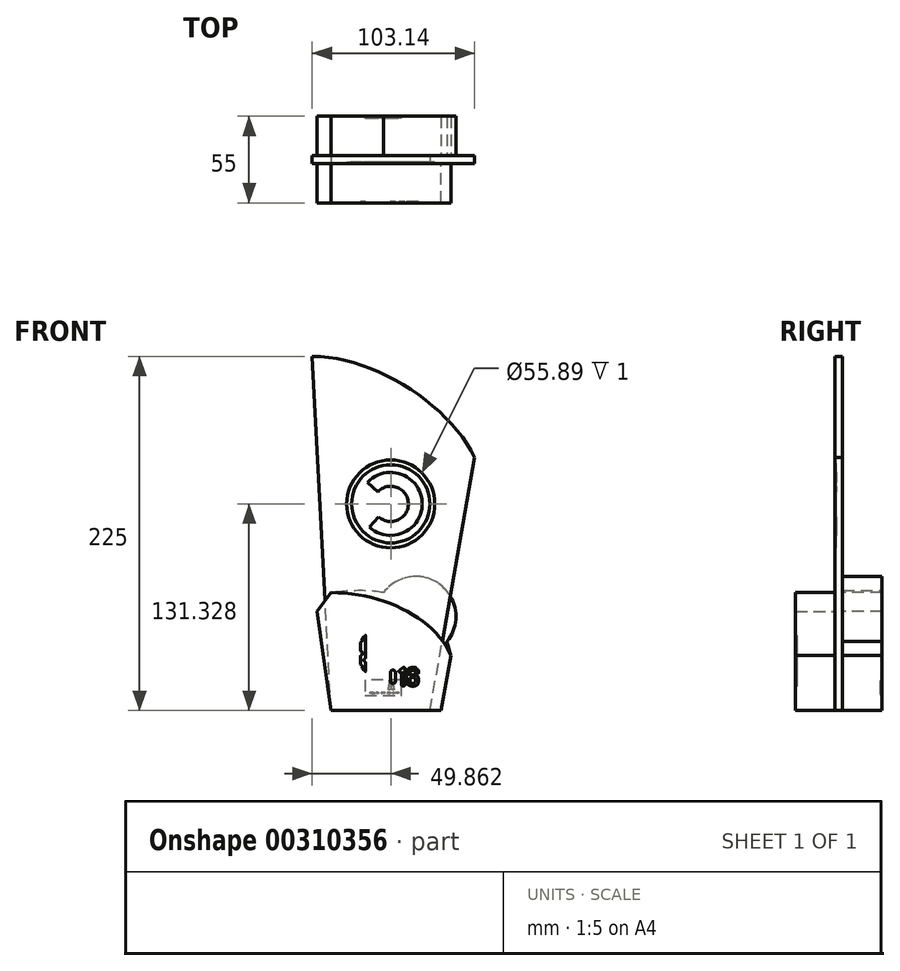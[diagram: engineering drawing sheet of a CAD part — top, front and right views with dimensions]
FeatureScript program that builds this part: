
annotation { "Feature Type Name" : "Feature", "Feature Type Description" : "" }
export const myFeature = defineFeature(function(context is Context, id is Id, definition is map)
    precondition{}
    {
        {
            var Q0;
            Q0=qCreatedBy(makeId("Front.planeOp"),FACE);
            var sketch = newSketch(context, id + "F0", { "sketchPlane" : qUnion([Q0])});
            skLineSegment(sketch, "E0", {"start": v(0, 0) * mm, "end": v(-8.85, 63) * mm});
            skLineSegment(sketch, "E1", {"start": v(-8.85, 63) * mm, "end": v(0, 75) * mm});
            skLineSegment(sketch, "E2", {"start": v(0, 0) * mm, "end": v(70, 0) * mm});
            skLineSegment(sketch, "E3", {"start": v(70, 0) * mm, "end": v(76.17, 35) * mm});
            skFitSpline(sketch, "E4", {"points": [v(0, 75) * mm, v(76.17, 35) * mm], "startDerivative": vector(102.47, -0.52) * mm, "endDerivative": vector(30.62, -70.87) * mm});
            skSolve(sketch);
        }
        {
            var Q0;
            Q0=makeQuery(id+"F0.imprint","IMPRINT",FACE,{"disambiguationData":[TD([[makeQuery(id+"F0.imprint","IMPRINT",EDGE,{"derivedFrom":sQuery(id+"F0.wireOp",EDGE,"E0")}),-1.0]])]});
            extrude(context, id + "F1", {"entities" : qUnion([Q0]), "depth" : 25 * mm});
        }
        {
            var Q0;
            Q0=makeQuery(id+"F1.opExtrude","CAP_FACE",FACE,{"disambiguationData":[OSD([sQuery(id+"F0.wireOp",EDGE,"E0"),sQuery(id+"F0.wireOp",EDGE,"E1"),sQuery(id+"F0.wireOp",EDGE,"E2"),sQuery(id+"F0.wireOp",EDGE,"E3"),sQuery(id+"F0.wireOp",EDGE,"E4")])],"isStart":true});
            var sketch = newSketch(context, id + "F2", { "sketchPlane" : qUnion([Q0])});
            skLineSegment(sketch, "E5", {"start": v(0, 0) * mm, "end": v(11.8, 225) * mm});
            skLineSegment(sketch, "E6", {"start": v(-63, 0) * mm, "end": v(-91.35, 160.77) * mm});
            skFitSpline(sketch, "E7", {"points": [v(11.8, 225) * mm, v(-91.35, 160.77) * mm], "startDerivative": vector(-117.23, 0.2) * mm, "endDerivative": vector(-48.13, -100.78) * mm});
            skLineSegment(sketch, "E8", {"start": v(0, 0) * mm, "end": v(-63, 0) * mm});
            skSolve(sketch);
        }
        {
            var Q0;
            {var subQ5=sQuery(id+"F2.wireOp",EDGE,"E7");Q0=makeQuery(id+"F2.imprint","IMPRINT",FACE,{"disambiguationData":[TD([[makeQuery(id+"F2.imprint","IMPRINT",EDGE,{"derivedFrom":subQ5}),1.0]])]});}
            var Q1;
            {var subQ0=sQuery(id+"F2.wireOp",EDGE,"E8");Q1=makeQuery(id+"F2.imprint","IMPRINT",FACE,{"disambiguationData":[TD([[makeQuery(id+"F2.imprint","IMPRINT",EDGE,{"derivedFrom":subQ0}),-1.0]])]});}
            extrude(context, id + "F3", {"entities" : qUnion([Q0, Q1]), "depth" : 5 * mm});
        }
        {
            var Q0;
            Q0=makeQuery(id+"F3.opExtrude","CAP_FACE",FACE,{"disambiguationData":[OSD([sQuery(id+"F2.wireOp",EDGE,"E5"),sQuery(id+"F2.wireOp",EDGE,"E6"),sQuery(id+"F2.wireOp",EDGE,"E7"),sQuery(id+"F2.wireOp",EDGE,"E8")])],"isStart":false});
            var sketch = newSketch(context, id + "F4", { "sketchPlane" : qUnion([Q0])});
            skFitSpline(sketch, "E9.0.0", {"points": [v(-76.17, 35) * mm, v(-65.97, 58.62) * mm, v(-34.16, 74.83) * mm, v(0, 75) * mm]});
            skLineSegment(sketch, "E9.0.1", {"start": v(0, 75) * mm, "end": v(8.85, 63) * mm});
            skLineSegment(sketch, "E9.0.2", {"start": v(8.85, 63) * mm, "end": v(0, 0) * mm});
            skLineSegment(sketch, "E9.0.3", {"start": v(0, 0) * mm, "end": v(-70, 0) * mm});
            skLineSegment(sketch, "E9.0.4", {"start": v(-70, 0) * mm, "end": v(-76.17, 35) * mm});
            skArc(sketch, "E10", {"start": v(-30.84, 70.38) * mm, "mid": v(-68.31, 80.8) * mm, "end": v(-72.31, 42.1) * mm});
            skFitSpline(sketch, "E11.trimOffspring", {"points": [v(-76.17, 35) * mm, v(-65.97, 58.62) * mm, v(-34.16, 74.83) * mm, v(0, 75) * mm]});
            skSolve(sketch);
        }
        {
            var Q0;
            Q0 = qSketchRegion(id + "F4", true);
            extrude(context, id + "F5", {"entities" : qUnion([Q0]), "depth" : 25 * mm});
        }
        {
            var Q0;
            Q0=makeQuery(id+"F1.opExtrude","CAP_FACE",FACE,{"disambiguationData":[OSD([sQuery(id+"F0.wireOp",EDGE,"E0"),sQuery(id+"F0.wireOp",EDGE,"E1"),sQuery(id+"F0.wireOp",EDGE,"E2"),sQuery(id+"F0.wireOp",EDGE,"E3"),sQuery(id+"F0.wireOp",EDGE,"E4")])],"isStart":false});
            var sketch = newSketch(context, id + "F6", { "sketchPlane" : qUnion([Q0])});
            skFitSpline(sketch, "E12", {"points": [v(15.05, 12.41) * mm, v(14.99, 12.45) * mm, v(14.9, 12.51) * mm, v(14.87, 12.56) * mm]});
            skFitSpline(sketch, "E13", {"points": [v(14.87, 12.56) * mm, v(14.79, 12.67) * mm, v(14.78, 12.9) * mm, v(14.86, 13.02) * mm]});
            skFitSpline(sketch, "E14", {"points": [v(14.86, 13.02) * mm, v(15.02, 13.26) * mm, v(16.64, 13.8) * mm, v(17.88, 14.02) * mm]});
            skFitSpline(sketch, "E15", {"points": [v(17.88, 14.02) * mm, v(18.82, 14.2) * mm, v(19.85, 14.28) * mm, v(20.87, 14.28) * mm]});
            skFitSpline(sketch, "E16", {"points": [v(20.87, 14.28) * mm, v(21.33, 14.28) * mm, v(21.37, 14.29) * mm, v(21.34, 14.34) * mm]});
            skFitSpline(sketch, "E17", {"points": [v(21.34, 14.34) * mm, v(21.1, 14.93) * mm, v(21.25, 15.6) * mm, v(21.7, 16.01) * mm]});
            skFitSpline(sketch, "E18", {"points": [v(21.71, 22.4) * mm, v(21.27, 22.8) * mm, v(21.1, 23.5) * mm, v(21.33, 24.03) * mm]});
            skLineSegment(sketch, "E19", {"start": v(21.7, 16.01) * mm, "end": v(21.88, 16.17) * mm});
            skLineSegment(sketch, "E20", {"start": v(21.88, 16.17) * mm, "end": v(21.88, 19.2) * mm});
            skLineSegment(sketch, "E21", {"start": v(21.88, 19.2) * mm, "end": v(21.88, 22.24) * mm});
            skLineSegment(sketch, "E22", {"start": v(21.88, 22.24) * mm, "end": v(21.71, 22.4) * mm});
            skFitSpline(sketch, "E23", {"points": [v(18.99, 26.4) * mm, v(18.86, 26.33) * mm, v(18.77, 26.32) * mm, v(18.43, 26.32) * mm]});
            skFitSpline(sketch, "E24", {"points": [v(18.43, 26.32) * mm, v(18.06, 26.32) * mm, v(18.02, 26.33) * mm, v(17.8, 26.43) * mm]});
            skFitSpline(sketch, "E25", {"points": [v(17.8, 26.43) * mm, v(17.5, 26.58) * mm, v(17.22, 26.85) * mm, v(17.08, 27.15) * mm]});
            skFitSpline(sketch, "E26", {"points": [v(17.08, 27.15) * mm, v(16.98, 27.37) * mm, v(16.97, 27.41) * mm, v(16.97, 27.77) * mm]});
            skFitSpline(sketch, "E27", {"points": [v(16.97, 27.77) * mm, v(16.97, 28.14) * mm, v(16.97, 28.16) * mm, v(17.1, 28.41) * mm]});
            skFitSpline(sketch, "E28", {"points": [v(17.1, 28.41) * mm, v(17.25, 28.72) * mm, v(17.5, 28.98) * mm, v(17.82, 29.12) * mm]});
            skLineSegment(sketch, "E29", {"start": v(21.33, 24.03) * mm, "end": v(21.4, 24.2) * mm});
            skLineSegment(sketch, "E30", {"start": v(21.4, 24.2) * mm, "end": v(20.28, 25.34) * mm});
            skLineSegment(sketch, "E31", {"start": v(20.28, 25.34) * mm, "end": v(19.15, 26.47) * mm});
            skLineSegment(sketch, "E32", {"start": v(19.15, 26.47) * mm, "end": v(18.99, 26.4) * mm});
            skFitSpline(sketch, "E33", {"points": [v(17.83, 34.98) * mm, v(17.62, 35.07) * mm, v(17.3, 35.34) * mm, v(17.17, 35.54) * mm]});
            skFitSpline(sketch, "E34", {"points": [v(17.17, 35.54) * mm, v(16.95, 35.9) * mm, v(16.9, 36.4) * mm, v(17.03, 36.82) * mm]});
            skLineSegment(sketch, "E35", {"start": v(17.82, 29.12) * mm, "end": v(18.02, 29.21) * mm});
            skLineSegment(sketch, "E36", {"start": v(18.02, 29.21) * mm, "end": v(18.02, 32.06) * mm});
            skLineSegment(sketch, "E37", {"start": v(18.02, 32.06) * mm, "end": v(18.02, 34.9) * mm});
            skLineSegment(sketch, "E38", {"start": v(18.02, 34.9) * mm, "end": v(17.83, 34.98) * mm});
            skFitSpline(sketch, "E39", {"points": [v(14.67, 39.23) * mm, v(14.4, 39.12) * mm, v(14.11, 39.1) * mm, v(13.84, 39.16) * mm]});
            skFitSpline(sketch, "E40", {"points": [v(13.84, 39.16) * mm, v(13.53, 39.23) * mm, v(13.36, 39.33) * mm, v(13.14, 39.54) * mm]});
            skFitSpline(sketch, "E41", {"points": [v(13.14, 39.54) * mm, v(12.81, 39.85) * mm, v(12.68, 40.16) * mm, v(12.68, 40.6) * mm]});
            skFitSpline(sketch, "E42", {"points": [v(12.68, 40.6) * mm, v(12.68, 41.2) * mm, v(12.99, 41.7) * mm, v(13.53, 41.95) * mm]});
            skLineSegment(sketch, "E43", {"start": v(17.03, 36.82) * mm, "end": v(17.11, 37.05) * mm});
            skLineSegment(sketch, "E44", {"start": v(17.11, 37.05) * mm, "end": v(15.99, 38.17) * mm});
            skLineSegment(sketch, "E45", {"start": v(15.99, 38.17) * mm, "end": v(14.86, 39.3) * mm});
            skLineSegment(sketch, "E46", {"start": v(14.86, 39.3) * mm, "end": v(14.67, 39.23) * mm});
            skFitSpline(sketch, "E47", {"points": [v(13.5, 52.12) * mm, v(12.4, 52.66) * mm, v(12.4, 54.26) * mm, v(13.54, 54.8) * mm]});
            skFitSpline(sketch, "E48", {"points": [v(13.54, 54.8) * mm, v(13.75, 54.9) * mm, v(13.8, 54.9) * mm, v(14.15, 54.9) * mm]});
            skFitSpline(sketch, "E49", {"points": [v(14.15, 54.9) * mm, v(14.5, 54.9) * mm, v(14.54, 54.9) * mm, v(14.75, 54.8) * mm]});
            skFitSpline(sketch, "E50", {"points": [v(14.75, 54.8) * mm, v(15.54, 54.43) * mm, v(15.85, 53.53) * mm, v(15.46, 52.75) * mm]});
            skFitSpline(sketch, "E51", {"points": [v(15.46, 52.75) * mm, v(15.33, 52.5) * mm, v(15.05, 52.25) * mm, v(14.8, 52.12) * mm]});
            skLineSegment(sketch, "E52", {"start": v(13.53, 41.95) * mm, "end": v(13.75, 42.05) * mm});
            skLineSegment(sketch, "E53", {"start": v(13.75, 42.05) * mm, "end": v(13.74, 47.03) * mm});
            skLineSegment(sketch, "E54", {"start": v(13.74, 47.03) * mm, "end": v(13.73, 52.01) * mm});
            skLineSegment(sketch, "E55", {"start": v(13.73, 52.01) * mm, "end": v(13.5, 52.12) * mm});
            skFitSpline(sketch, "E56", {"points": [v(14.7, 41.98) * mm, v(15, 41.87) * mm, v(15.34, 41.56) * mm, v(15.49, 41.24) * mm]});
            skFitSpline(sketch, "E57", {"points": [v(15.49, 41.24) * mm, v(15.66, 40.87) * mm, v(15.67, 40.47) * mm, v(15.52, 40.04) * mm]});
            skLineSegment(sketch, "E58", {"start": v(14.8, 52.12) * mm, "end": v(14.58, 52.02) * mm});
            skLineSegment(sketch, "E59", {"start": v(14.58, 52.02) * mm, "end": v(14.58, 47.02) * mm});
            skLineSegment(sketch, "E60", {"start": v(14.58, 47.02) * mm, "end": v(14.58, 42.02) * mm});
            skLineSegment(sketch, "E61", {"start": v(14.58, 42.02) * mm, "end": v(14.7, 41.98) * mm});
            skFitSpline(sketch, "E62", {"points": [v(17.8, 43.55) * mm, v(17.5, 43.7) * mm, v(17.23, 43.97) * mm, v(17.08, 44.27) * mm]});
            skFitSpline(sketch, "E63", {"points": [v(17.08, 44.27) * mm, v(16.98, 44.49) * mm, v(16.98, 44.53) * mm, v(16.97, 44.88) * mm]});
            skFitSpline(sketch, "E64", {"points": [v(16.97, 44.88) * mm, v(16.97, 45.24) * mm, v(16.98, 45.28) * mm, v(17.08, 45.5) * mm]});
            skFitSpline(sketch, "E65", {"points": [v(17.08, 45.5) * mm, v(17.29, 45.93) * mm, v(17.66, 46.23) * mm, v(18.12, 46.33) * mm]});
            skFitSpline(sketch, "E66", {"points": [v(18.12, 46.33) * mm, v(18.41, 46.4) * mm, v(18.62, 46.38) * mm, v(18.95, 46.27) * mm]});
            skLineSegment(sketch, "E67", {"start": v(15.52, 40.04) * mm, "end": v(15.46, 39.87) * mm});
            skLineSegment(sketch, "E68", {"start": v(15.46, 39.87) * mm, "end": v(16.58, 38.75) * mm});
            skLineSegment(sketch, "E69", {"start": v(16.58, 38.75) * mm, "end": v(17.7, 37.64) * mm});
            skLineSegment(sketch, "E70", {"start": v(17.7, 37.64) * mm, "end": v(17.86, 37.7) * mm});
            skLineSegment(sketch, "E71", {"start": v(17.86, 37.7) * mm, "end": v(18.02, 37.75) * mm});
            skLineSegment(sketch, "E72", {"start": v(18.02, 37.75) * mm, "end": v(18.02, 40.6) * mm});
            skLineSegment(sketch, "E73", {"start": v(18.02, 40.6) * mm, "end": v(18.02, 43.45) * mm});
            skLineSegment(sketch, "E74", {"start": v(18.02, 43.45) * mm, "end": v(17.8, 43.55) * mm});
            skFitSpline(sketch, "E75", {"points": [v(20.28, 47.31) * mm, v(21, 48.03) * mm, v(21.4, 48.45) * mm, v(21.39, 48.48) * mm]});
            skFitSpline(sketch, "E76", {"points": [v(21.39, 48.48) * mm, v(21.38, 48.5) * mm, v(21.34, 48.6) * mm, v(21.31, 48.69) * mm]});
            skFitSpline(sketch, "E77", {"points": [v(21.31, 48.69) * mm, v(21.18, 49.04) * mm, v(21.22, 49.5) * mm, v(21.4, 49.87) * mm]});
            skFitSpline(sketch, "E78", {"points": [v(21.4, 49.87) * mm, v(21.51, 50.08) * mm, v(21.8, 50.36) * mm, v(22, 50.47) * mm]});
            skLineSegment(sketch, "E79", {"start": v(18.95, 46.27) * mm, "end": v(19.16, 46.2) * mm});
            skLineSegment(sketch, "E80", {"start": v(19.16, 46.2) * mm, "end": v(20.28, 47.31) * mm});
            skFitSpline(sketch, "E81", {"points": [v(22.03, 56.42) * mm, v(21.42, 56.73) * mm, v(21.1, 57.43) * mm, v(21.28, 58.11) * mm]});
            skFitSpline(sketch, "E82", {"points": [v(21.28, 58.11) * mm, v(21.39, 58.52) * mm, v(21.69, 58.88) * mm, v(22.08, 59.07) * mm]});
            skFitSpline(sketch, "E83", {"points": [v(22.08, 59.07) * mm, v(22.3, 59.17) * mm, v(22.34, 59.18) * mm, v(22.71, 59.18) * mm]});
            skFitSpline(sketch, "E84", {"points": [v(22.71, 59.18) * mm, v(23.08, 59.18) * mm, v(23.12, 59.17) * mm, v(23.33, 59.07) * mm]});
            skFitSpline(sketch, "E85", {"points": [v(23.33, 59.07) * mm, v(24.45, 58.53) * mm, v(24.48, 56.96) * mm, v(23.37, 56.4) * mm]});
            skLineSegment(sketch, "E86", {"start": v(22, 50.47) * mm, "end": v(22.2, 50.56) * mm});
            skLineSegment(sketch, "E87", {"start": v(22.2, 50.56) * mm, "end": v(22.2, 53.45) * mm});
            skLineSegment(sketch, "E88", {"start": v(22.2, 53.45) * mm, "end": v(22.2, 56.33) * mm});
            skLineSegment(sketch, "E89", {"start": v(22.2, 56.33) * mm, "end": v(22.03, 56.42) * mm});
            skFitSpline(sketch, "E90", {"points": [v(23.42, 50.47) * mm, v(24.08, 50.12) * mm, v(24.38, 49.25) * mm, v(24.06, 48.57) * mm]});
            skFitSpline(sketch, "E91", {"points": [v(24.06, 48.57) * mm, v(23.93, 48.29) * mm, v(23.66, 48) * mm, v(23.42, 47.87) * mm]});
            skLineSegment(sketch, "E92", {"start": v(23.37, 56.4) * mm, "end": v(23.23, 56.33) * mm});
            skLineSegment(sketch, "E93", {"start": v(23.23, 56.33) * mm, "end": v(23.23, 53.45) * mm});
            skLineSegment(sketch, "E94", {"start": v(23.23, 53.45) * mm, "end": v(23.23, 50.56) * mm});
            skLineSegment(sketch, "E95", {"start": v(23.23, 50.56) * mm, "end": v(23.42, 50.47) * mm});
            skFitSpline(sketch, "E96", {"points": [v(25.6, 35.8) * mm, v(25.46, 36.22) * mm, v(25.48, 36.6) * mm, v(25.66, 36.98) * mm]});
            skFitSpline(sketch, "E97", {"points": [v(25.66, 36.98) * mm, v(25.78, 37.24) * mm, v(26.12, 37.56) * mm, v(26.37, 37.67) * mm]});
            skLineSegment(sketch, "E98", {"start": v(23.42, 47.87) * mm, "end": v(23.23, 47.78) * mm});
            skLineSegment(sketch, "E99", {"start": v(23.23, 47.78) * mm, "end": v(23.23, 40.6) * mm});
            skLineSegment(sketch, "E100", {"start": v(23.23, 40.6) * mm, "end": v(23.23, 33.43) * mm});
            skLineSegment(sketch, "E101", {"start": v(23.23, 33.43) * mm, "end": v(23.33, 33.4) * mm});
            skLineSegment(sketch, "E102", {"start": v(23.33, 33.4) * mm, "end": v(23.44, 33.35) * mm});
            skLineSegment(sketch, "E103", {"start": v(23.44, 33.35) * mm, "end": v(24.56, 34.47) * mm});
            skLineSegment(sketch, "E104", {"start": v(24.56, 34.47) * mm, "end": v(25.68, 35.6) * mm});
            skLineSegment(sketch, "E105", {"start": v(25.68, 35.6) * mm, "end": v(25.6, 35.8) * mm});
            skLineSegment(sketch, "E106", {"start": v(25.6, 35.8) * mm, "end": v(25.51, 36.34) * mm});
            skFitSpline(sketch, "E107", {"points": [v(26.37, 47.83) * mm, v(26.12, 47.93) * mm, v(25.79, 48.25) * mm, v(25.66, 48.52) * mm]});
            skFitSpline(sketch, "E108", {"points": [v(25.66, 48.52) * mm, v(25.14, 49.6) * mm, v(26.05, 50.83) * mm, v(27.22, 50.63) * mm]});
            skFitSpline(sketch, "E109", {"points": [v(27.22, 50.63) * mm, v(28.32, 50.44) * mm, v(28.83, 49.18) * mm, v(28.17, 48.29) * mm]});
            skFitSpline(sketch, "E110", {"points": [v(28.17, 48.29) * mm, v(28.01, 48.07) * mm, v(27.68, 47.82) * mm, v(27.5, 47.78) * mm]});
            skLineSegment(sketch, "E111", {"start": v(26.37, 37.67) * mm, "end": v(26.56, 37.75) * mm});
            skLineSegment(sketch, "E112", {"start": v(26.56, 37.75) * mm, "end": v(26.56, 42.75) * mm});
            skLineSegment(sketch, "E113", {"start": v(26.56, 42.75) * mm, "end": v(26.57, 47.75) * mm});
            skLineSegment(sketch, "E114", {"start": v(26.57, 47.75) * mm, "end": v(26.37, 47.83) * mm});
            skFitSpline(sketch, "E115", {"points": [v(27.5, 37.72) * mm, v(27.68, 37.68) * mm, v(28.01, 37.43) * mm, v(28.17, 37.21) * mm]});
            skFitSpline(sketch, "E116", {"points": [v(28.17, 37.21) * mm, v(28.44, 36.84) * mm, v(28.53, 36.32) * mm, v(28.4, 35.89) * mm]});
            skFitSpline(sketch, "E117", {"points": [v(28.4, 35.89) * mm, v(28.14, 35.08) * mm, v(27.25, 34.64) * mm, v(26.46, 34.95) * mm]});
            skLineSegment(sketch, "E118", {"start": v(27.5, 47.78) * mm, "end": v(27.4, 47.76) * mm});
            skLineSegment(sketch, "E119", {"start": v(27.4, 47.76) * mm, "end": v(27.4, 42.75) * mm});
            skLineSegment(sketch, "E120", {"start": v(27.4, 42.75) * mm, "end": v(27.4, 37.74) * mm});
            skLineSegment(sketch, "E121", {"start": v(27.4, 37.74) * mm, "end": v(27.5, 37.72) * mm});
            skFitSpline(sketch, "E122", {"points": [v(24.06, 32.65) * mm, v(24.23, 32.32) * mm, v(24.22, 31.82) * mm, v(24.05, 31.44) * mm]});
            skFitSpline(sketch, "E123", {"points": [v(24.05, 31.44) * mm, v(23.92, 31.16) * mm, v(23.61, 30.84) * mm, v(23.37, 30.73) * mm]});
            skLineSegment(sketch, "E124", {"start": v(26.46, 34.95) * mm, "end": v(26.27, 35.02) * mm});
            skLineSegment(sketch, "E125", {"start": v(26.27, 35.02) * mm, "end": v(25.14, 33.89) * mm});
            skLineSegment(sketch, "E126", {"start": v(25.14, 33.89) * mm, "end": v(24, 32.75) * mm});
            skLineSegment(sketch, "E127", {"start": v(24, 32.75) * mm, "end": v(24.06, 32.65) * mm});
            skFitSpline(sketch, "E128", {"points": [v(29.9, 31.5) * mm, v(29.68, 32) * mm, v(29.8, 32.67) * mm, v(30.21, 33.09) * mm]});
            skFitSpline(sketch, "E129", {"points": [v(30.21, 33.09) * mm, v(30.3, 33.18) * mm, v(30.48, 33.3) * mm, v(30.63, 33.38) * mm]});
            skLineSegment(sketch, "E130", {"start": v(23.37, 30.73) * mm, "end": v(23.23, 30.67) * mm});
            skLineSegment(sketch, "E131", {"start": v(23.23, 30.67) * mm, "end": v(23.23, 27.78) * mm});
            skLineSegment(sketch, "E132", {"start": v(23.23, 27.78) * mm, "end": v(23.23, 24.9) * mm});
            skLineSegment(sketch, "E133", {"start": v(23.23, 24.9) * mm, "end": v(23.32, 24.84) * mm});
            skLineSegment(sketch, "E134", {"start": v(23.32, 24.84) * mm, "end": v(23.42, 24.8) * mm});
            skLineSegment(sketch, "E135", {"start": v(23.42, 24.8) * mm, "end": v(26.7, 28.07) * mm});
            skLineSegment(sketch, "E136", {"start": v(26.7, 28.07) * mm, "end": v(29.97, 31.34) * mm});
            skLineSegment(sketch, "E137", {"start": v(29.97, 31.34) * mm, "end": v(29.9, 31.5) * mm});
            skFitSpline(sketch, "E138", {"points": [v(30.65, 43.56) * mm, v(30.04, 43.84) * mm, v(29.72, 44.45) * mm, v(29.8, 45.11) * mm]});
            skFitSpline(sketch, "E139", {"points": [v(29.8, 45.11) * mm, v(29.92, 45.9) * mm, v(30.72, 46.5) * mm, v(31.5, 46.36) * mm]});
            skFitSpline(sketch, "E140", {"points": [v(31.5, 46.36) * mm, v(32.47, 46.19) * mm, v(33.02, 45.15) * mm, v(32.6, 44.26) * mm]});
            skFitSpline(sketch, "E141", {"points": [v(32.6, 44.26) * mm, v(32.48, 44) * mm, v(32.15, 43.67) * mm, v(31.9, 43.56) * mm]});
            skLineSegment(sketch, "E142", {"start": v(30.63, 33.38) * mm, "end": v(30.87, 33.5) * mm});
            skLineSegment(sketch, "E143", {"start": v(30.87, 33.5) * mm, "end": v(30.87, 38.48) * mm});
            skLineSegment(sketch, "E144", {"start": v(30.87, 38.48) * mm, "end": v(30.87, 43.45) * mm});
            skLineSegment(sketch, "E145", {"start": v(30.87, 43.45) * mm, "end": v(30.65, 43.56) * mm});
            skFitSpline(sketch, "E146", {"points": [v(31.91, 33.38) * mm, v(32.47, 33.12) * mm, v(32.82, 32.47) * mm, v(32.73, 31.85) * mm]});
            skFitSpline(sketch, "E147", {"points": [v(32.73, 31.85) * mm, v(32.6, 30.93) * mm, v(31.67, 30.36) * mm, v(30.8, 30.66) * mm]});
            skLineSegment(sketch, "E148", {"start": v(31.9, 43.56) * mm, "end": v(31.7, 43.48) * mm});
            skLineSegment(sketch, "E149", {"start": v(31.7, 43.48) * mm, "end": v(31.7, 38.48) * mm});
            skLineSegment(sketch, "E150", {"start": v(31.7, 38.48) * mm, "end": v(31.7, 33.48) * mm});
            skLineSegment(sketch, "E151", {"start": v(31.7, 33.48) * mm, "end": v(31.91, 33.38) * mm});
            skFitSpline(sketch, "E152", {"points": [v(24.09, 24.03) * mm, v(24.3, 23.46) * mm, v(24.15, 22.81) * mm, v(23.69, 22.38) * mm]});
            skLineSegment(sketch, "E153", {"start": v(30.8, 30.66) * mm, "end": v(30.54, 30.74) * mm});
            skLineSegment(sketch, "E154", {"start": v(30.54, 30.74) * mm, "end": v(27.28, 27.48) * mm});
            skLineSegment(sketch, "E155", {"start": v(27.28, 27.48) * mm, "end": v(24.02, 24.22) * mm});
            skLineSegment(sketch, "E156", {"start": v(24.02, 24.22) * mm, "end": v(24.09, 24.03) * mm});
            skFitSpline(sketch, "E157", {"points": [v(23.7, 16.01) * mm, v(24.17, 15.58) * mm, v(24.31, 14.91) * mm, v(24.07, 14.34) * mm]});
            skFitSpline(sketch, "E158", {"points": [v(24.07, 14.34) * mm, v(24.05, 14.28) * mm, v(24.83, 14.28) * mm, v(40.2, 14.28) * mm]});
            skFitSpline(sketch, "E159", {"points": [v(40.2, 14.28) * mm, v(52.62, 14.27) * mm, v(56.38, 14.27) * mm, v(56.47, 14.23) * mm]});
            skFitSpline(sketch, "E160", {"points": [v(56.47, 14.23) * mm, v(56.62, 14.18) * mm, v(56.71, 14.05) * mm, v(56.72, 13.88) * mm]});
            skFitSpline(sketch, "E161", {"points": [v(56.72, 13.88) * mm, v(56.72, 13.7) * mm, v(56.63, 13.54) * mm, v(56.51, 13.5) * mm]});
            skFitSpline(sketch, "E162", {"points": [v(56.51, 13.5) * mm, v(56.44, 13.46) * mm, v(51.68, 13.45) * mm, v(38, 13.44) * mm]});
            skLineSegment(sketch, "E163", {"start": v(23.69, 22.38) * mm, "end": v(23.53, 22.24) * mm});
            skLineSegment(sketch, "E164", {"start": v(23.53, 22.24) * mm, "end": v(23.53, 19.2) * mm});
            skLineSegment(sketch, "E165", {"start": v(23.53, 19.2) * mm, "end": v(23.53, 16.18) * mm});
            skLineSegment(sketch, "E166", {"start": v(23.53, 16.18) * mm, "end": v(23.7, 16.01) * mm});
            skFitSpline(sketch, "E167", {"points": [v(19, 13.36) * mm, v(17.8, 13.2) * mm, v(16.68, 12.93) * mm, v(15.78, 12.58) * mm]});
            skFitSpline(sketch, "E168", {"points": [v(15.78, 12.58) * mm, v(15.18, 12.34) * mm, v(15.2, 12.34) * mm, v(15.06, 12.41) * mm]});
            skLineSegment(sketch, "E169", {"start": v(38, 13.44) * mm, "end": v(19.59, 13.43) * mm});
            skLineSegment(sketch, "E170", {"start": v(19.59, 13.43) * mm, "end": v(19, 13.36) * mm});
            skLineSegment(sketch, "E171", {"start": v(15.06, 12.41) * mm, "end": v(15.05, 12.41) * mm});
            skLineSegment(sketch, "E172", {"start": v(15.05, 12.41) * mm, "end": v(15.06, 12.41) * mm});
            skFitSpline(sketch, "E173", {"points": [v(22.01, 30.75) * mm, v(21.81, 30.84) * mm, v(21.5, 31.15) * mm, v(21.4, 31.37) * mm]});
            skFitSpline(sketch, "E174", {"points": [v(21.4, 31.37) * mm, v(21.15, 31.84) * mm, v(21.17, 32.37) * mm, v(21.44, 32.83) * mm]});
            skFitSpline(sketch, "E175", {"points": [v(21.44, 32.83) * mm, v(21.55, 33.01) * mm, v(21.81, 33.26) * mm, v(22.03, 33.37) * mm]});
            skLineSegment(sketch, "E176", {"start": v(22.18, 27.77) * mm, "end": v(22.18, 30.66) * mm});
            skLineSegment(sketch, "E177", {"start": v(22.18, 30.66) * mm, "end": v(22.01, 30.75) * mm});
            skFitSpline(sketch, "E178", {"points": [v(22.1, 47.84) * mm, v(22, 47.88) * mm, v(21.98, 47.86) * mm, v(20.86, 46.74) * mm]});
            skLineSegment(sketch, "E179", {"start": v(22.03, 33.37) * mm, "end": v(22.19, 33.45) * mm});
            skLineSegment(sketch, "E180", {"start": v(22.19, 33.45) * mm, "end": v(22.19, 40.62) * mm});
            skLineSegment(sketch, "E181", {"start": v(22.19, 40.62) * mm, "end": v(22.19, 47.8) * mm});
            skLineSegment(sketch, "E182", {"start": v(22.19, 47.8) * mm, "end": v(22.1, 47.84) * mm});
            skFitSpline(sketch, "E183", {"points": [v(19.78, 45.48) * mm, v(19.82, 45.4) * mm, v(19.86, 45.25) * mm, v(19.88, 45.12) * mm]});
            skFitSpline(sketch, "E184", {"points": [v(19.88, 45.12) * mm, v(19.99, 44.5) * mm, v(19.63, 43.84) * mm, v(19.06, 43.56) * mm]});
            skLineSegment(sketch, "E185", {"start": v(20.86, 46.74) * mm, "end": v(19.73, 45.6) * mm});
            skLineSegment(sketch, "E186", {"start": v(19.73, 45.6) * mm, "end": v(19.78, 45.48) * mm});
            skFitSpline(sketch, "E187", {"points": [v(19.04, 37.68) * mm, v(19.62, 37.42) * mm, v(19.99, 36.74) * mm, v(19.88, 36.1) * mm]});
            skFitSpline(sketch, "E188", {"points": [v(19.88, 36.1) * mm, v(19.8, 35.63) * mm, v(19.48, 35.2) * mm, v(19.06, 35) * mm]});
            skLineSegment(sketch, "E189", {"start": v(19.06, 43.56) * mm, "end": v(18.84, 43.46) * mm});
            skLineSegment(sketch, "E190", {"start": v(18.84, 43.46) * mm, "end": v(18.84, 40.61) * mm});
            skLineSegment(sketch, "E191", {"start": v(18.84, 40.61) * mm, "end": v(18.84, 37.76) * mm});
            skLineSegment(sketch, "E192", {"start": v(18.84, 37.76) * mm, "end": v(19.04, 37.68) * mm});
            skFitSpline(sketch, "E193", {"points": [v(19.07, 29.1) * mm, v(19.76, 28.76) * mm, v(20.07, 27.97) * mm, v(19.8, 27.25) * mm]});
            skLineSegment(sketch, "E194", {"start": v(19.06, 35) * mm, "end": v(18.84, 34.9) * mm});
            skLineSegment(sketch, "E195", {"start": v(18.84, 34.9) * mm, "end": v(18.84, 32.06) * mm});
            skLineSegment(sketch, "E196", {"start": v(18.84, 32.06) * mm, "end": v(18.84, 29.21) * mm});
            skLineSegment(sketch, "E197", {"start": v(18.84, 29.21) * mm, "end": v(19.07, 29.1) * mm});
            skFitSpline(sketch, "E198", {"points": [v(20.86, 25.93) * mm, v(21.97, 24.81) * mm, v(21.99, 24.8) * mm, v(22.09, 24.84) * mm]});
            skLineSegment(sketch, "E199", {"start": v(19.8, 27.25) * mm, "end": v(19.73, 27.06) * mm});
            skLineSegment(sketch, "E200", {"start": v(19.73, 27.06) * mm, "end": v(20.86, 25.93) * mm});
            skFitSpline(sketch, "E201", {"points": [v(38.84, 15.56) * mm, v(38.02, 15.65) * mm, v(37.4, 15.87) * mm, v(36.87, 16.28) * mm]});
            skFitSpline(sketch, "E202", {"points": [v(36.87, 16.28) * mm, v(36.4, 16.62) * mm, v(36.07, 17.1) * mm, v(35.88, 17.71) * mm]});
            skFitSpline(sketch, "E203", {"points": [v(35.88, 17.71) * mm, v(35.7, 18.29) * mm, v(35.7, 18.29) * mm, v(35.7, 21.47) * mm]});
            skLineSegment(sketch, "E204", {"start": v(22.09, 24.84) * mm, "end": v(22.19, 24.87) * mm});
            skLineSegment(sketch, "E205", {"start": v(22.19, 24.87) * mm, "end": v(22.19, 27.77) * mm});
            skLineSegment(sketch, "E206", {"start": v(22.19, 27.77) * mm, "end": v(22.18, 27.77) * mm});
            skLineSegment(sketch, "E207", {"start": v(22.18, 27.77) * mm, "end": v(22.09, 24.84) * mm});
            skFitSpline(sketch, "E208", {"points": [v(35.78, 24.79) * mm, v(35.98, 25.68) * mm, v(36.34, 26.25) * mm, v(37, 26.7) * mm]});
            skFitSpline(sketch, "E209", {"points": [v(37, 26.7) * mm, v(37.64, 27.13) * mm, v(38.42, 27.34) * mm, v(39.44, 27.34) * mm]});
            skFitSpline(sketch, "E210", {"points": [v(39.44, 27.34) * mm, v(40.26, 27.34) * mm, v(40.88, 27.21) * mm, v(41.46, 26.93) * mm]});
            skFitSpline(sketch, "E211", {"points": [v(41.46, 26.93) * mm, v(42.22, 26.55) * mm, v(42.72, 25.99) * mm, v(42.97, 25.23) * mm]});
            skFitSpline(sketch, "E212", {"points": [v(42.97, 25.23) * mm, v(43.17, 24.6) * mm, v(43.18, 24.59) * mm, v(43.19, 21.72) * mm]});
            skFitSpline(sketch, "E213", {"points": [v(43.19, 21.72) * mm, v(43.2, 18.89) * mm, v(43.19, 18.49) * mm, v(43.04, 17.9) * mm]});
            skFitSpline(sketch, "E214", {"points": [v(43.04, 17.9) * mm, v(42.72, 16.66) * mm, v(41.8, 15.86) * mm, v(40.4, 15.61) * mm]});
            skFitSpline(sketch, "E215", {"points": [v(40.4, 15.61) * mm, v(40, 15.55) * mm, v(39.2, 15.52) * mm, v(38.84, 15.56) * mm]});
            skLineSegment(sketch, "E216", {"start": v(35.7, 21.47) * mm, "end": v(35.7, 24.43) * mm});
            skLineSegment(sketch, "E217", {"start": v(35.7, 24.43) * mm, "end": v(35.78, 24.79) * mm});
            skFitSpline(sketch, "E218", {"points": [v(39.93, 17.39) * mm, v(40.38, 17.48) * mm, v(40.72, 17.73) * mm, v(40.9, 18.12) * mm]});
            skFitSpline(sketch, "E219", {"points": [v(40.9, 18.12) * mm, v(41.12, 18.56) * mm, v(41.13, 18.62) * mm, v(41.13, 21.43) * mm]});
            skFitSpline(sketch, "E220", {"points": [v(41.13, 21.43) * mm, v(41.13, 22.92) * mm, v(41.12, 24.03) * mm, v(41.1, 24.15) * mm]});
            skFitSpline(sketch, "E221", {"points": [v(41.1, 24.15) * mm, v(41.01, 24.66) * mm, v(40.83, 25) * mm, v(40.51, 25.24) * mm]});
            skFitSpline(sketch, "E222", {"points": [v(40.51, 25.24) * mm, v(39.94, 25.67) * mm, v(38.79, 25.64) * mm, v(38.26, 25.17) * mm]});
            skFitSpline(sketch, "E223", {"points": [v(38.26, 25.17) * mm, v(38.1, 25.03) * mm, v(37.95, 24.8) * mm, v(37.85, 24.51) * mm]});
            skLineSegment(sketch, "E224", {"start": v(38.84, 15.56) * mm, "end": v(38.84, 15.56) * mm});
            skFitSpline(sketch, "E225", {"points": [v(37.76, 21.56) * mm, v(37.76, 19.25) * mm, v(37.76, 18.8) * mm, v(37.8, 18.59) * mm]});
            skFitSpline(sketch, "E226", {"points": [v(37.8, 18.59) * mm, v(37.94, 17.95) * mm, v(38.3, 17.56) * mm, v(38.87, 17.4) * mm]});
            skFitSpline(sketch, "E227", {"points": [v(38.87, 17.4) * mm, v(39.09, 17.34) * mm, v(39.68, 17.34) * mm, v(39.93, 17.39) * mm]});
            skLineSegment(sketch, "E228", {"start": v(37.85, 24.51) * mm, "end": v(37.77, 24.29) * mm});
            skLineSegment(sketch, "E229", {"start": v(37.77, 24.29) * mm, "end": v(37.76, 21.56) * mm});
            skFitSpline(sketch, "E230", {"points": [v(39.2, 20.72) * mm, v(38.9, 20.82) * mm, v(38.72, 21.09) * mm, v(38.72, 21.44) * mm]});
            skFitSpline(sketch, "E231", {"points": [v(38.72, 21.44) * mm, v(38.72, 21.9) * mm, v(38.98, 22.15) * mm, v(39.44, 22.15) * mm]});
            skFitSpline(sketch, "E232", {"points": [v(39.44, 22.15) * mm, v(39.7, 22.15) * mm, v(39.83, 22.09) * mm, v(39.99, 21.92) * mm]});
            skFitSpline(sketch, "E233", {"points": [v(39.99, 21.92) * mm, v(40.28, 21.58) * mm, v(40.2, 21.02) * mm, v(39.84, 20.8) * mm]});
            skFitSpline(sketch, "E234", {"points": [v(39.84, 20.8) * mm, v(39.7, 20.7) * mm, v(39.36, 20.67) * mm, v(39.2, 20.72) * mm]});
            skLineSegment(sketch, "E235", {"start": v(39.93, 17.39) * mm, "end": v(39.93, 17.39) * mm});
            skFitSpline(sketch, "E236", {"points": [v(51.38, 15.56) * mm, v(50.8, 15.62) * mm, v(50.37, 15.74) * mm, v(49.93, 15.96) * mm]});
            skFitSpline(sketch, "E237", {"points": [v(49.93, 15.96) * mm, v(49.17, 16.33) * mm, v(48.63, 16.94) * mm, v(48.4, 17.72) * mm]});
            skFitSpline(sketch, "E238", {"points": [v(48.4, 17.72) * mm, v(48.22, 18.33) * mm, v(48.22, 18.36) * mm, v(48.2, 21.13) * mm]});
            skFitSpline(sketch, "E239", {"points": [v(48.2, 21.13) * mm, v(48.19, 24.27) * mm, v(48.21, 24.66) * mm, v(48.47, 25.34) * mm]});
            skFitSpline(sketch, "E240", {"points": [v(48.47, 25.34) * mm, v(48.78, 26.14) * mm, v(49.4, 26.72) * mm, v(50.25, 27.05) * mm]});
            skFitSpline(sketch, "E241", {"points": [v(50.25, 27.05) * mm, v(50.75, 27.24) * mm, v(51.16, 27.3) * mm, v(51.86, 27.33) * mm]});
            skFitSpline(sketch, "E242", {"points": [v(51.86, 27.33) * mm, v(53.26, 27.37) * mm, v(54.15, 27.08) * mm, v(54.88, 26.34) * mm]});
            skFitSpline(sketch, "E243", {"points": [v(54.88, 26.34) * mm, v(55.4, 25.82) * mm, v(55.67, 25.24) * mm, v(55.7, 24.58) * mm]});
            skFitSpline(sketch, "E244", {"points": [v(55.7, 24.58) * mm, v(55.72, 24.04) * mm, v(55.64, 23.83) * mm, v(55.35, 23.68) * mm]});
            skFitSpline(sketch, "E245", {"points": [v(55.35, 23.68) * mm, v(55.15, 23.57) * mm, v(54.53, 23.55) * mm, v(54.24, 23.64) * mm]});
            skFitSpline(sketch, "E246", {"points": [v(54.24, 23.64) * mm, v(53.85, 23.75) * mm, v(53.71, 23.92) * mm, v(53.67, 24.36) * mm]});
            skFitSpline(sketch, "E247", {"points": [v(53.67, 24.36) * mm, v(53.63, 24.73) * mm, v(53.52, 24.96) * mm, v(53.26, 25.15) * mm]});
            skFitSpline(sketch, "E248", {"points": [v(53.26, 25.15) * mm, v(52.9, 25.44) * mm, v(52.4, 25.58) * mm, v(51.85, 25.54) * mm]});
            skFitSpline(sketch, "E249", {"points": [v(51.85, 25.54) * mm, v(51.31, 25.5) * mm, v(50.97, 25.35) * mm, v(50.7, 25.07) * mm]});
            skFitSpline(sketch, "E250", {"points": [v(50.7, 25.07) * mm, v(50.5, 24.86) * mm, v(50.41, 24.68) * mm, v(50.33, 24.35) * mm]});
            skFitSpline(sketch, "E251", {"points": [v(50.33, 24.35) * mm, v(50.27, 24.12) * mm, v(50.26, 23.97) * mm, v(50.26, 23) * mm]});
            skLineSegment(sketch, "E252", {"start": v(39.2, 20.72) * mm, "end": v(39.2, 20.72) * mm});
            skFitSpline(sketch, "E253", {"points": [v(50.47, 22.11) * mm, v(50.73, 22.35) * mm, v(50.99, 22.49) * mm, v(51.38, 22.6) * mm]});
            skFitSpline(sketch, "E254", {"points": [v(51.38, 22.6) * mm, v(51.92, 22.77) * mm, v(52.93, 22.76) * mm, v(53.56, 22.6) * mm]});
            skFitSpline(sketch, "E255", {"points": [v(53.56, 22.6) * mm, v(54.49, 22.36) * mm, v(55.15, 21.8) * mm, v(55.46, 21.01) * mm]});
            skFitSpline(sketch, "E256", {"points": [v(55.46, 21.01) * mm, v(55.66, 20.5) * mm, v(55.69, 20.25) * mm, v(55.69, 19.3) * mm]});
            skFitSpline(sketch, "E257", {"points": [v(55.69, 19.3) * mm, v(55.69, 18.38) * mm, v(55.66, 18.15) * mm, v(55.48, 17.63) * mm]});
            skFitSpline(sketch, "E258", {"points": [v(55.48, 17.63) * mm, v(55.16, 16.7) * mm, v(54.43, 16.02) * mm, v(53.4, 15.72) * mm]});
            skFitSpline(sketch, "E259", {"points": [v(53.4, 15.72) * mm, v(52.88, 15.57) * mm, v(51.95, 15.5) * mm, v(51.38, 15.56) * mm]});
            skLineSegment(sketch, "E260", {"start": v(50.26, 23) * mm, "end": v(50.26, 21.93) * mm});
            skLineSegment(sketch, "E261", {"start": v(50.26, 21.93) * mm, "end": v(50.47, 22.11) * mm});
            skFitSpline(sketch, "E262", {"points": [v(52.38, 17.24) * mm, v(52.7, 17.3) * mm, v(52.94, 17.42) * mm, v(53.13, 17.59) * mm]});
            skFitSpline(sketch, "E263", {"points": [v(53.13, 17.59) * mm, v(53.5, 17.93) * mm, v(53.64, 18.34) * mm, v(53.64, 19.17) * mm]});
            skFitSpline(sketch, "E264", {"points": [v(53.64, 19.17) * mm, v(53.64, 19.96) * mm, v(53.52, 20.35) * mm, v(53.2, 20.68) * mm]});
            skFitSpline(sketch, "E265", {"points": [v(53.2, 20.68) * mm, v(52.9, 20.98) * mm, v(52.54, 21.1) * mm, v(51.97, 21.11) * mm]});
            skFitSpline(sketch, "E266", {"points": [v(51.97, 21.11) * mm, v(51.03, 21.12) * mm, v(50.5, 20.76) * mm, v(50.31, 20) * mm]});
            skFitSpline(sketch, "E267", {"points": [v(50.31, 20) * mm, v(50.25, 19.7) * mm, v(50.24, 18.76) * mm, v(50.3, 18.45) * mm]});
            skFitSpline(sketch, "E268", {"points": [v(50.3, 18.45) * mm, v(50.48, 17.64) * mm, v(51.03, 17.22) * mm, v(51.93, 17.21) * mm]});
            skFitSpline(sketch, "E269", {"points": [v(51.93, 17.21) * mm, v(52.09, 17.21) * mm, v(52.3, 17.22) * mm, v(52.38, 17.24) * mm]});
            skLineSegment(sketch, "E270", {"start": v(51.38, 15.56) * mm, "end": v(51.38, 15.56) * mm});
            skFitSpline(sketch, "E271", {"points": [v(28.35, 15.68) * mm, v(28.15, 15.75) * mm, v(27.95, 15.9) * mm, v(27.85, 16.02) * mm]});
            skFitSpline(sketch, "E272", {"points": [v(27.85, 16.02) * mm, v(27.78, 16.1) * mm, v(27.78, 16.16) * mm, v(27.77, 17.04) * mm]});
            skFitSpline(sketch, "E273", {"points": [v(27.77, 17.04) * mm, v(27.76, 18.08) * mm, v(27.79, 18.3) * mm, v(27.98, 18.7) * mm]});
            skFitSpline(sketch, "E274", {"points": [v(27.98, 18.7) * mm, v(28.2, 19.16) * mm, v(28.75, 19.8) * mm, v(29.32, 20.27) * mm]});
            skFitSpline(sketch, "E275", {"points": [v(29.32, 20.27) * mm, v(29.46, 20.38) * mm, v(29.94, 20.73) * mm, v(30.38, 21.05) * mm]});
            skFitSpline(sketch, "E276", {"points": [v(30.38, 21.05) * mm, v(31.36, 21.75) * mm, v(31.62, 21.96) * mm, v(32.02, 22.36) * mm]});
            skFitSpline(sketch, "E277", {"points": [v(32.02, 22.36) * mm, v(32.72, 23.06) * mm, v(32.95, 23.52) * mm, v(32.92, 24.14) * mm]});
            skFitSpline(sketch, "E278", {"points": [v(32.92, 24.14) * mm, v(32.91, 24.39) * mm, v(32.89, 24.47) * mm, v(32.8, 24.66) * mm]});
            skFitSpline(sketch, "E279", {"points": [v(32.8, 24.66) * mm, v(32.51, 25.25) * mm, v(32.01, 25.52) * mm, v(31.3, 25.47) * mm]});
            skFitSpline(sketch, "E280", {"points": [v(31.3, 25.47) * mm, v(30.82, 25.44) * mm, v(30.41, 25.23) * mm, v(30.2, 24.9) * mm]});
            skFitSpline(sketch, "E281", {"points": [v(30.2, 24.9) * mm, v(30.08, 24.7) * mm, v(30.04, 24.57) * mm, v(30, 24.2) * mm]});
            skFitSpline(sketch, "E282", {"points": [v(30, 24.2) * mm, v(29.95, 23.72) * mm, v(29.77, 23.48) * mm, v(29.36, 23.36) * mm]});
            skFitSpline(sketch, "E283", {"points": [v(29.36, 23.36) * mm, v(29.16, 23.3) * mm, v(28.73, 23.3) * mm, v(28.54, 23.35) * mm]});
            skFitSpline(sketch, "E284", {"points": [v(28.54, 23.35) * mm, v(28.35, 23.4) * mm, v(28.13, 23.63) * mm, v(28.05, 23.86) * mm]});
            skFitSpline(sketch, "E285", {"points": [v(28.05, 23.86) * mm, v(27.96, 24.13) * mm, v(27.97, 24.77) * mm, v(28.07, 25.14) * mm]});
            skFitSpline(sketch, "E286", {"points": [v(28.07, 25.14) * mm, v(28.2, 25.66) * mm, v(28.5, 26.11) * mm, v(28.95, 26.48) * mm]});
            skFitSpline(sketch, "E287", {"points": [v(28.95, 26.48) * mm, v(29.63, 27.05) * mm, v(30.45, 27.34) * mm, v(31.42, 27.34) * mm]});
            skFitSpline(sketch, "E288", {"points": [v(31.42, 27.34) * mm, v(32.56, 27.34) * mm, v(33.47, 26.96) * mm, v(34.23, 26.16) * mm]});
            skFitSpline(sketch, "E289", {"points": [v(34.23, 26.16) * mm, v(34.54, 25.82) * mm, v(34.74, 25.48) * mm, v(34.88, 25.01) * mm]});
            skFitSpline(sketch, "E290", {"points": [v(34.88, 25.01) * mm, v(34.97, 24.73) * mm, v(34.97, 24.65) * mm, v(34.98, 24.14) * mm]});
            skFitSpline(sketch, "E291", {"points": [v(34.98, 24.14) * mm, v(34.98, 23.46) * mm, v(34.92, 23.18) * mm, v(34.65, 22.64) * mm]});
            skFitSpline(sketch, "E292", {"points": [v(34.65, 22.64) * mm, v(34.18, 21.67) * mm, v(33.57, 21.07) * mm, v(31.86, 19.9) * mm]});
            skFitSpline(sketch, "E293", {"points": [v(31.86, 19.9) * mm, v(30.8, 19.17) * mm, v(30.23, 18.67) * mm, v(30.03, 18.28) * mm]});
            skFitSpline(sketch, "E294", {"points": [v(30.03, 18.28) * mm, v(29.93, 18.08) * mm, v(29.92, 18.02) * mm, v(29.92, 17.74) * mm]});
            skLineSegment(sketch, "E295", {"start": v(52.38, 17.24) * mm, "end": v(52.38, 17.24) * mm});
            skFitSpline(sketch, "E296", {"points": [v(32.24, 17.42) * mm, v(34.86, 17.4) * mm, v(34.65, 17.42) * mm, v(34.85, 17.12) * mm]});
            skFitSpline(sketch, "E297", {"points": [v(34.85, 17.12) * mm, v(35, 16.9) * mm, v(35.04, 16.73) * mm, v(35.02, 16.46) * mm]});
            skFitSpline(sketch, "E298", {"points": [v(35.02, 16.46) * mm, v(35, 16.21) * mm, v(34.91, 15.99) * mm, v(34.76, 15.82) * mm]});
            skFitSpline(sketch, "E299", {"points": [v(34.76, 15.82) * mm, v(34.57, 15.62) * mm, v(34.75, 15.63) * mm, v(31.5, 15.63) * mm]});
            skFitSpline(sketch, "E300", {"points": [v(31.5, 15.63) * mm, v(28.87, 15.63) * mm, v(28.48, 15.64) * mm, v(28.35, 15.69) * mm]});
            skLineSegment(sketch, "E301", {"start": v(29.92, 17.74) * mm, "end": v(29.91, 17.43) * mm});
            skLineSegment(sketch, "E302", {"start": v(29.91, 17.43) * mm, "end": v(32.24, 17.42) * mm});
            skFitSpline(sketch, "E303", {"points": [v(45.65, 15.68) * mm, v(45.4, 15.74) * mm, v(45.17, 15.9) * mm, v(45.09, 16.04) * mm]});
            skFitSpline(sketch, "E304", {"points": [v(45.09, 16.04) * mm, v(45.02, 16.16) * mm, v(45.02, 16.34) * mm, v(45.02, 20.52) * mm]});
            skLineSegment(sketch, "E305", {"start": v(28.35, 15.69) * mm, "end": v(28.35, 15.68) * mm});
            skLineSegment(sketch, "E306", {"start": v(28.35, 15.68) * mm, "end": v(28.35, 15.69) * mm});
            skFitSpline(sketch, "E307", {"points": [v(44.72, 24.58) * mm, v(44.28, 24.15) * mm, v(44.04, 24.1) * mm, v(43.74, 24.37) * mm]});
            skFitSpline(sketch, "E308", {"points": [v(43.74, 24.37) * mm, v(43.4, 24.67) * mm, v(43.35, 25.25) * mm, v(43.63, 25.58) * mm]});
            skFitSpline(sketch, "E309", {"points": [v(43.63, 25.58) * mm, v(43.74, 25.7) * mm, v(45.82, 27.3) * mm, v(45.94, 27.34) * mm]});
            skFitSpline(sketch, "E310", {"points": [v(45.94, 27.34) * mm, v(46.28, 27.47) * mm, v(46.87, 27.26) * mm, v(47.02, 26.94) * mm]});
            skFitSpline(sketch, "E311", {"points": [v(47.02, 26.94) * mm, v(47.09, 26.8) * mm, v(47.1, 26.71) * mm, v(47.1, 21.5) * mm]});
            skFitSpline(sketch, "E312", {"points": [v(47.1, 21.5) * mm, v(47.1, 17.1) * mm, v(47.09, 16.2) * mm, v(47.04, 16.1) * mm]});
            skFitSpline(sketch, "E313", {"points": [v(47.04, 16.1) * mm, v(46.99, 15.95) * mm, v(46.78, 15.78) * mm, v(46.58, 15.71) * mm]});
            skFitSpline(sketch, "E314", {"points": [v(46.58, 15.71) * mm, v(46.36, 15.64) * mm, v(45.88, 15.62) * mm, v(45.65, 15.68) * mm]});
            skLineSegment(sketch, "E315", {"start": v(45.02, 20.52) * mm, "end": v(45.02, 24.87) * mm});
            skLineSegment(sketch, "E316", {"start": v(45.02, 24.87) * mm, "end": v(44.72, 24.58) * mm});
            skLineSegment(sketch, "E317", {"start": v(45.65, 15.68) * mm, "end": v(45.65, 15.68) * mm});
            skSolve(sketch);
        }
        {
            var Q0;
            Q0 = qSketchRegion(id + "F6", true);
            var Q1;
            Q1=makeQuery(id+"F6.imprint","IMPRINT",FACE,{"disambiguationData":[TD([[makeQuery(id+"F6.imprint","IMPRINT",EDGE,{"derivedFrom":sQuery(id+"F6.wireOp",EDGE,"E230")}),-1.0]])]});
            extrude(context, id + "F7", {"entities" : qUnion([Q0, Q1]), "operationType" : NewBodyOperationType.REMOVE, "oppositeDirection" : true, "depth" : 1 * mm});
        }
        {
            var Q0;
            Q0=makeQuery(id+"F3.opExtrude","CAP_FACE",FACE,{"disambiguationData":[OSD([sQuery(id+"F2.wireOp",EDGE,"E5"),sQuery(id+"F2.wireOp",EDGE,"E6"),sQuery(id+"F2.wireOp",EDGE,"E7"),sQuery(id+"F2.wireOp",EDGE,"E8")])],"isStart":true});
            var sketch = newSketch(context, id + "F8", { "sketchPlane" : qUnion([Q0])});
            skCircle(sketch, "E318", {"center": v(38.07, 131.33) * mm, "radius": 27.94 * mm});
            skCircle(sketch, "E319", {"center": v(38.07, 131.33) * mm, "radius": 24.83 * mm});
            skArc(sketch, "E320", {"start": v(24.44, 116.7) * mm, "mid": v(58.05, 132.03) * mm, "end": v(23.44, 144.96) * mm});
            skArc(sketch, "E321", {"start": v(30.45, 123.15) * mm, "mid": v(49.25, 131.72) * mm, "end": v(29.9, 138.95) * mm});
            skLineSegment(sketch, "E322", {"start": v(29.9, 138.95) * mm, "end": v(23.44, 144.96) * mm});
            skLineSegment(sketch, "E323", {"start": v(30.45, 123.15) * mm, "end": v(24.44, 116.7) * mm});
            skSolve(sketch);
        }
        {
            var Q0;
            Q0=makeQuery(id+"F8.imprint","IMPRINT",FACE,{"disambiguationData":[TD([[makeQuery(id+"F8.imprint","IMPRINT",EDGE,{"derivedFrom":sQuery(id+"F8.wireOp",EDGE,"E318")}),1.0]])]});
            var Q1;
            Q1=makeQuery(id+"F8.imprint","IMPRINT",FACE,{"disambiguationData":[TD([[makeQuery(id+"F8.imprint","IMPRINT",EDGE,{"derivedFrom":sQuery(id+"F8.wireOp",EDGE,"E320")}),1.0]])]});
            extrude(context, id + "F9", {"entities" : qUnion([Q0, Q1]), "operationType" : NewBodyOperationType.REMOVE, "oppositeDirection" : true, "depth" : 1 * mm});
        }
        {
            var Q0;
            Q0=makeQuery(id+"F5.opExtrude","CAP_FACE",FACE,{"disambiguationData":[OSD([sQuery(id+"F4.wireOp",EDGE,"E9.0.0"),sQuery(id+"F4.wireOp",EDGE,"E9.0.1"),sQuery(id+"F4.wireOp",EDGE,"E9.0.2"),sQuery(id+"F4.wireOp",EDGE,"E9.0.3"),sQuery(id+"F4.wireOp",EDGE,"E9.0.4"),sQuery(id+"F4.wireOp",EDGE,"E10"),sQuery(id+"F4.wireOp",EDGE,"E11.trimOffspring")])],"isStart":false});
            var sketch = newSketch(context, id + "F10", { "sketchPlane" : qUnion([Q0])});
            skFitSpline(sketch, "E324", {"points": [v(-32.63, 11.88) * mm, v(-32.57, 11.81) * mm, v(-32.5, 11.76) * mm, v(-32.46, 11.7) * mm]});
            skFitSpline(sketch, "E325", {"points": [v(-32.46, 11.7) * mm, v(-32.42, 11.65) * mm, v(-32.37, 11.65) * mm, v(-32.3, 11.67) * mm]});
            skFitSpline(sketch, "E326", {"points": [v(-32.3, 11.67) * mm, v(-32.34, 11.7) * mm, v(-32.37, 11.75) * mm, v(-32.4, 11.78) * mm]});
            skFitSpline(sketch, "E327", {"points": [v(-32.4, 11.78) * mm, v(-32.47, 11.89) * mm, v(-32.47, 11.89) * mm, v(-32.6, 11.88) * mm]});
            skFitSpline(sketch, "E328", {"points": [v(-32.6, 11.88) * mm, v(-32.61, 11.88) * mm, v(-32.61, 11.88) * mm, v(-32.63, 11.88) * mm]});
            skFitSpline(sketch, "E329", {"points": [v(-25.03, 11.84) * mm, v(-25.05, 11.84) * mm, v(-25.07, 11.84) * mm, v(-25.1, 11.84) * mm]});
            skFitSpline(sketch, "E330", {"points": [v(-25.1, 11.84) * mm, v(-25.12, 11.84) * mm, v(-25.13, 11.83) * mm, v(-25.13, 11.8) * mm]});
            skFitSpline(sketch, "E331", {"points": [v(-25.13, 11.8) * mm, v(-25.13, 11.77) * mm, v(-25.13, 11.73) * mm, v(-25.13, 11.7) * mm]});
            skFitSpline(sketch, "E332", {"points": [v(-25.13, 11.7) * mm, v(-25.13, 11.67) * mm, v(-25.12, 11.66) * mm, v(-25.1, 11.66) * mm]});
            skFitSpline(sketch, "E333", {"points": [v(-25.1, 11.66) * mm, v(-25.06, 11.66) * mm, v(-25.02, 11.66) * mm, v(-24.99, 11.66) * mm]});
            skFitSpline(sketch, "E334", {"points": [v(-24.99, 11.66) * mm, v(-24.9, 11.66) * mm, v(-24.92, 11.66) * mm, v(-24.92, 11.73) * mm]});
            skFitSpline(sketch, "E335", {"points": [v(-24.92, 11.73) * mm, v(-24.92, 11.84) * mm, v(-24.92, 11.84) * mm, v(-25.03, 11.84) * mm]});
            skFitSpline(sketch, "E336", {"points": [v(-24.92, 11.24) * mm, v(-24.92, 11.34) * mm, v(-24.92, 11.43) * mm, v(-24.92, 11.53) * mm]});
            skFitSpline(sketch, "E337", {"points": [v(-24.92, 11.53) * mm, v(-24.92, 11.58) * mm, v(-24.92, 11.58) * mm, v(-24.97, 11.58) * mm]});
            skFitSpline(sketch, "E338", {"points": [v(-24.97, 11.58) * mm, v(-25, 11.58) * mm, v(-25.05, 11.58) * mm, v(-25.09, 11.58) * mm]});
            skFitSpline(sketch, "E339", {"points": [v(-25.09, 11.58) * mm, v(-25.12, 11.58) * mm, v(-25.13, 11.57) * mm, v(-25.13, 11.54) * mm]});
            skFitSpline(sketch, "E340", {"points": [v(-25.13, 11.54) * mm, v(-25.13, 11.34) * mm, v(-25.13, 11.14) * mm, v(-25.13, 10.95) * mm]});
            skFitSpline(sketch, "E341", {"points": [v(-25.13, 10.95) * mm, v(-25.13, 10.92) * mm, v(-25.12, 10.91) * mm, v(-25.1, 10.91) * mm]});
            skFitSpline(sketch, "E342", {"points": [v(-25.1, 10.91) * mm, v(-25.05, 10.91) * mm, v(-25, 10.91) * mm, v(-24.96, 10.91) * mm]});
            skFitSpline(sketch, "E343", {"points": [v(-24.96, 10.91) * mm, v(-24.93, 10.9) * mm, v(-24.92, 10.92) * mm, v(-24.92, 10.96) * mm]});
            skFitSpline(sketch, "E344", {"points": [v(-24.92, 10.96) * mm, v(-24.92, 11.05) * mm, v(-24.92, 11.15) * mm, v(-24.92, 11.24) * mm]});
            skFitSpline(sketch, "E345", {"points": [v(-25.81, 11.5) * mm, v(-25.81, 11.6) * mm, v(-25.81, 11.7) * mm, v(-25.81, 11.8) * mm]});
            skFitSpline(sketch, "E346", {"points": [v(-25.81, 11.8) * mm, v(-25.81, 11.83) * mm, v(-25.82, 11.84) * mm, v(-25.86, 11.84) * mm]});
            skFitSpline(sketch, "E347", {"points": [v(-25.86, 11.84) * mm, v(-25.9, 11.84) * mm, v(-25.95, 11.84) * mm, v(-26, 11.84) * mm]});
            skFitSpline(sketch, "E348", {"points": [v(-26, 11.84) * mm, v(-26.02, 11.84) * mm, v(-26.03, 11.83) * mm, v(-26.02, 11.8) * mm]});
            skFitSpline(sketch, "E349", {"points": [v(-26.02, 11.8) * mm, v(-26.02, 11.8) * mm, v(-26.02, 11.78) * mm, v(-26.02, 11.77) * mm]});
            skLineSegment(sketch, "E350", {"start": v(-25.81, 11.37) * mm, "end": v(-25.81, 11.5) * mm});
            skFitSpline(sketch, "E351", {"points": [v(-26.02, 10.98) * mm, v(-26.02, 10.97) * mm, v(-26.02, 10.96) * mm, v(-26.02, 10.94) * mm]});
            skFitSpline(sketch, "E352", {"points": [v(-26.02, 10.94) * mm, v(-26.03, 10.92) * mm, v(-26.02, 10.91) * mm, v(-26, 10.91) * mm]});
            skFitSpline(sketch, "E353", {"points": [v(-26, 10.91) * mm, v(-25.95, 10.91) * mm, v(-25.9, 10.91) * mm, v(-25.86, 10.91) * mm]});
            skFitSpline(sketch, "E354", {"points": [v(-25.86, 10.91) * mm, v(-25.82, 10.91) * mm, v(-25.81, 10.91) * mm, v(-25.81, 10.96) * mm]});
            skFitSpline(sketch, "E355", {"points": [v(-25.81, 10.96) * mm, v(-25.81, 11.1) * mm, v(-25.81, 11.23) * mm, v(-25.81, 11.37) * mm]});
            skFitSpline(sketch, "E356", {"points": [v(-23.33, 11.4) * mm, v(-23.33, 11.46) * mm, v(-23.33, 11.5) * mm, v(-23.33, 11.56) * mm]});
            skFitSpline(sketch, "E357", {"points": [v(-23.33, 11.56) * mm, v(-23.33, 11.58) * mm, v(-23.34, 11.6) * mm, v(-23.37, 11.6) * mm]});
            skFitSpline(sketch, "E358", {"points": [v(-23.37, 11.6) * mm, v(-23.45, 11.6) * mm, v(-23.52, 11.58) * mm, v(-23.58, 11.52) * mm]});
            skFitSpline(sketch, "E359", {"points": [v(-23.58, 11.52) * mm, v(-23.59, 11.5) * mm, v(-23.6, 11.49) * mm, v(-23.62, 11.5) * mm]});
            skFitSpline(sketch, "E360", {"points": [v(-23.62, 11.5) * mm, v(-23.62, 11.5) * mm, v(-23.62, 11.52) * mm, v(-23.62, 11.53) * mm]});
            skFitSpline(sketch, "E361", {"points": [v(-23.62, 11.53) * mm, v(-23.62, 11.58) * mm, v(-23.62, 11.58) * mm, v(-23.67, 11.58) * mm]});
            skFitSpline(sketch, "E362", {"points": [v(-23.67, 11.58) * mm, v(-23.7, 11.58) * mm, v(-23.74, 11.58) * mm, v(-23.78, 11.58) * mm]});
            skFitSpline(sketch, "E363", {"points": [v(-23.78, 11.58) * mm, v(-23.83, 11.58) * mm, v(-23.83, 11.58) * mm, v(-23.83, 11.52) * mm]});
            skFitSpline(sketch, "E364", {"points": [v(-23.83, 11.52) * mm, v(-23.83, 11.36) * mm, v(-23.83, 11.2) * mm, v(-23.83, 11.05) * mm]});
            skFitSpline(sketch, "E365", {"points": [v(-23.83, 11.05) * mm, v(-23.83, 11) * mm, v(-23.85, 10.95) * mm, v(-23.82, 10.92) * mm]});
            skFitSpline(sketch, "E366", {"points": [v(-23.82, 10.92) * mm, v(-23.8, 10.9) * mm, v(-23.74, 10.91) * mm, v(-23.7, 10.91) * mm]});
            skFitSpline(sketch, "E367", {"points": [v(-23.7, 10.91) * mm, v(-23.6, 10.9) * mm, v(-23.62, 10.9) * mm, v(-23.62, 10.99) * mm]});
            skFitSpline(sketch, "E368", {"points": [v(-23.62, 10.99) * mm, v(-23.62, 11.08) * mm, v(-23.62, 11.17) * mm, v(-23.61, 11.26) * mm]});
            skFitSpline(sketch, "E369", {"points": [v(-23.61, 11.26) * mm, v(-23.6, 11.38) * mm, v(-23.52, 11.44) * mm, v(-23.4, 11.42) * mm]});
            skFitSpline(sketch, "E370", {"points": [v(-23.4, 11.42) * mm, v(-23.38, 11.41) * mm, v(-23.36, 11.4) * mm, v(-23.33, 11.4) * mm]});
            skLineSegment(sketch, "E371", {"start": v(-26.02, 11.77) * mm, "end": v(-26.02, 10.98) * mm});
            skFitSpline(sketch, "E372", {"points": [v(-25.58, 11.3) * mm, v(-25.58, 11.19) * mm, v(-25.58, 11.07) * mm, v(-25.58, 10.95) * mm]});
            skFitSpline(sketch, "E373", {"points": [v(-25.58, 10.95) * mm, v(-25.58, 10.92) * mm, v(-25.57, 10.9) * mm, v(-25.54, 10.91) * mm]});
            skFitSpline(sketch, "E374", {"points": [v(-25.54, 10.91) * mm, v(-25.5, 10.91) * mm, v(-25.46, 10.91) * mm, v(-25.43, 10.91) * mm]});
            skFitSpline(sketch, "E375", {"points": [v(-25.43, 10.91) * mm, v(-25.36, 10.91) * mm, v(-25.36, 10.91) * mm, v(-25.36, 10.97) * mm]});
            skFitSpline(sketch, "E376", {"points": [v(-25.36, 10.97) * mm, v(-25.36, 11.23) * mm, v(-25.36, 11.49) * mm, v(-25.36, 11.74) * mm]});
            skFitSpline(sketch, "E377", {"points": [v(-25.36, 11.74) * mm, v(-25.36, 11.76) * mm, v(-25.36, 11.78) * mm, v(-25.36, 11.8) * mm]});
            skFitSpline(sketch, "E378", {"points": [v(-25.36, 11.8) * mm, v(-25.36, 11.83) * mm, v(-25.37, 11.84) * mm, v(-25.4, 11.84) * mm]});
            skFitSpline(sketch, "E379", {"points": [v(-25.4, 11.84) * mm, v(-25.44, 11.84) * mm, v(-25.49, 11.84) * mm, v(-25.53, 11.84) * mm]});
            skFitSpline(sketch, "E380", {"points": [v(-25.53, 11.84) * mm, v(-25.58, 11.84) * mm, v(-25.58, 11.84) * mm, v(-25.58, 11.79) * mm]});
            skFitSpline(sketch, "E381", {"points": [v(-25.58, 11.79) * mm, v(-25.58, 11.65) * mm, v(-25.58, 11.51) * mm, v(-25.58, 11.38) * mm]});
            skFitSpline(sketch, "E382", {"points": [v(-41.7, 10.91) * mm, v(-41.7, 10.93) * mm, v(-41.69, 10.94) * mm, v(-41.69, 10.95) * mm]});
            skFitSpline(sketch, "E383", {"points": [v(-41.69, 10.95) * mm, v(-41.69, 11.22) * mm, v(-41.69, 11.48) * mm, v(-41.69, 11.75) * mm]});
            skFitSpline(sketch, "E384", {"points": [v(-41.69, 11.75) * mm, v(-41.69, 11.76) * mm, v(-41.69, 11.77) * mm, v(-41.69, 11.78) * mm]});
            skFitSpline(sketch, "E385", {"points": [v(-41.69, 11.78) * mm, v(-41.69, 11.8) * mm, v(-41.7, 11.8) * mm, v(-41.7, 11.8) * mm]});
            skLineSegment(sketch, "E386", {"start": v(-25.58, 11.38) * mm, "end": v(-25.58, 11.3) * mm});
            skFitSpline(sketch, "E387", {"points": [v(-41.92, 10.97) * mm, v(-41.92, 10.96) * mm, v(-41.92, 10.95) * mm, v(-41.92, 10.94) * mm]});
            skFitSpline(sketch, "E388", {"points": [v(-41.92, 10.94) * mm, v(-41.92, 10.92) * mm, v(-41.9, 10.91) * mm, v(-41.89, 10.91) * mm]});
            skFitSpline(sketch, "E389", {"points": [v(-41.89, 10.91) * mm, v(-41.82, 10.91) * mm, v(-41.76, 10.91) * mm, v(-41.7, 10.91) * mm]});
            skLineSegment(sketch, "E390", {"start": v(-41.7, 11.8) * mm, "end": v(-41.92, 11.8) * mm});
            skLineSegment(sketch, "E391", {"start": v(-41.92, 11.8) * mm, "end": v(-41.92, 11.75) * mm});
            skLineSegment(sketch, "E392", {"start": v(-41.92, 11.75) * mm, "end": v(-41.92, 10.97) * mm});
            skFitSpline(sketch, "E393", {"points": [v(-28.37, 11.23) * mm, v(-28.37, 11.18) * mm, v(-28.37, 11.13) * mm, v(-28.37, 11.08) * mm]});
            skFitSpline(sketch, "E394", {"points": [v(-28.37, 11.08) * mm, v(-28.36, 10.98) * mm, v(-28.3, 10.92) * mm, v(-28.2, 10.91) * mm]});
            skFitSpline(sketch, "E395", {"points": [v(-28.2, 10.91) * mm, v(-28.16, 10.91) * mm, v(-28.1, 10.91) * mm, v(-28.06, 10.91) * mm]});
            skFitSpline(sketch, "E396", {"points": [v(-28.06, 10.91) * mm, v(-27.94, 10.91) * mm, v(-27.96, 10.89) * mm, v(-27.96, 11.02) * mm]});
            skFitSpline(sketch, "E397", {"points": [v(-27.96, 11.02) * mm, v(-27.96, 11.02) * mm, v(-27.96, 11.03) * mm, v(-27.96, 11.03) * mm]});
            skFitSpline(sketch, "E398", {"points": [v(-27.96, 11.03) * mm, v(-27.96, 11.05) * mm, v(-27.97, 11.06) * mm, v(-27.99, 11.06) * mm]});
            skFitSpline(sketch, "E399", {"points": [v(-27.99, 11.06) * mm, v(-28.02, 11.06) * mm, v(-28.06, 11.06) * mm, v(-28.1, 11.06) * mm]});
            skFitSpline(sketch, "E400", {"points": [v(-28.1, 11.06) * mm, v(-28.14, 11.07) * mm, v(-28.16, 11.08) * mm, v(-28.16, 11.13) * mm]});
            skFitSpline(sketch, "E401", {"points": [v(-28.16, 11.13) * mm, v(-28.16, 11.22) * mm, v(-28.16, 11.3) * mm, v(-28.16, 11.4) * mm]});
            skFitSpline(sketch, "E402", {"points": [v(-28.16, 11.4) * mm, v(-28.16, 11.41) * mm, v(-28.15, 11.42) * mm, v(-28.13, 11.42) * mm]});
            skFitSpline(sketch, "E403", {"points": [v(-28.13, 11.42) * mm, v(-28.1, 11.42) * mm, v(-28.07, 11.42) * mm, v(-28.05, 11.42) * mm]});
            skFitSpline(sketch, "E404", {"points": [v(-28.05, 11.42) * mm, v(-27.94, 11.42) * mm, v(-27.94, 11.42) * mm, v(-27.94, 11.53) * mm]});
            skFitSpline(sketch, "E405", {"points": [v(-27.94, 11.53) * mm, v(-27.94, 11.58) * mm, v(-27.94, 11.58) * mm, v(-27.99, 11.58) * mm]});
            skFitSpline(sketch, "E406", {"points": [v(-27.99, 11.58) * mm, v(-28.03, 11.58) * mm, v(-28.08, 11.58) * mm, v(-28.13, 11.58) * mm]});
            skFitSpline(sketch, "E407", {"points": [v(-28.13, 11.58) * mm, v(-28.15, 11.58) * mm, v(-28.16, 11.59) * mm, v(-28.16, 11.6) * mm]});
            skFitSpline(sketch, "E408", {"points": [v(-28.16, 11.6) * mm, v(-28.16, 11.65) * mm, v(-28.16, 11.69) * mm, v(-28.16, 11.73) * mm]});
            skFitSpline(sketch, "E409", {"points": [v(-28.16, 11.73) * mm, v(-28.16, 11.75) * mm, v(-28.17, 11.76) * mm, v(-28.2, 11.76) * mm]});
            skFitSpline(sketch, "E410", {"points": [v(-28.2, 11.76) * mm, v(-28.24, 11.76) * mm, v(-28.29, 11.76) * mm, v(-28.33, 11.76) * mm]});
            skFitSpline(sketch, "E411", {"points": [v(-28.33, 11.76) * mm, v(-28.36, 11.76) * mm, v(-28.37, 11.76) * mm, v(-28.37, 11.73) * mm]});
            skFitSpline(sketch, "E412", {"points": [v(-28.37, 11.73) * mm, v(-28.37, 11.7) * mm, v(-28.37, 11.66) * mm, v(-28.37, 11.62) * mm]});
            skFitSpline(sketch, "E413", {"points": [v(-28.37, 11.62) * mm, v(-28.37, 11.6) * mm, v(-28.38, 11.57) * mm, v(-28.41, 11.58) * mm]});
            skFitSpline(sketch, "E414", {"points": [v(-28.41, 11.58) * mm, v(-28.42, 11.58) * mm, v(-28.43, 11.58) * mm, v(-28.44, 11.58) * mm]});
            skFitSpline(sketch, "E415", {"points": [v(-28.44, 11.58) * mm, v(-28.47, 11.58) * mm, v(-28.48, 11.57) * mm, v(-28.48, 11.54) * mm]});
            skFitSpline(sketch, "E416", {"points": [v(-28.48, 11.54) * mm, v(-28.48, 11.51) * mm, v(-28.48, 11.48) * mm, v(-28.48, 11.46) * mm]});
            skFitSpline(sketch, "E417", {"points": [v(-28.48, 11.46) * mm, v(-28.48, 11.43) * mm, v(-28.47, 11.42) * mm, v(-28.45, 11.42) * mm]});
            skFitSpline(sketch, "E418", {"points": [v(-28.45, 11.42) * mm, v(-28.43, 11.42) * mm, v(-28.42, 11.42) * mm, v(-28.41, 11.42) * mm]});
            skFitSpline(sketch, "E419", {"points": [v(-28.41, 11.42) * mm, v(-28.38, 11.43) * mm, v(-28.37, 11.42) * mm, v(-28.37, 11.38) * mm]});
            skFitSpline(sketch, "E420", {"points": [v(-28.37, 11.38) * mm, v(-28.37, 11.33) * mm, v(-28.37, 11.28) * mm, v(-28.37, 11.23) * mm]});
            skFitSpline(sketch, "E421", {"points": [v(-35.88, 11.36) * mm, v(-35.88, 11.23) * mm, v(-35.88, 11.1) * mm, v(-35.88, 10.97) * mm]});
            skFitSpline(sketch, "E422", {"points": [v(-35.88, 10.97) * mm, v(-35.88, 10.9) * mm, v(-35.89, 10.91) * mm, v(-35.82, 10.91) * mm]});
            skFitSpline(sketch, "E423", {"points": [v(-35.82, 10.91) * mm, v(-35.67, 10.91) * mm, v(-35.51, 10.91) * mm, v(-35.36, 10.91) * mm]});
            skFitSpline(sketch, "E424", {"points": [v(-35.36, 10.91) * mm, v(-35.33, 10.91) * mm, v(-35.28, 10.9) * mm, v(-35.26, 10.92) * mm]});
            skFitSpline(sketch, "E425", {"points": [v(-35.26, 10.92) * mm, v(-35.23, 10.94) * mm, v(-35.25, 11) * mm, v(-35.25, 11.03) * mm]});
            skFitSpline(sketch, "E426", {"points": [v(-35.25, 11.03) * mm, v(-35.24, 11.08) * mm, v(-35.25, 11.08) * mm, v(-35.3, 11.08) * mm]});
            skFitSpline(sketch, "E427", {"points": [v(-35.3, 11.08) * mm, v(-35.4, 11.08) * mm, v(-35.5, 11.08) * mm, v(-35.6, 11.08) * mm]});
            skFitSpline(sketch, "E428", {"points": [v(-35.6, 11.08) * mm, v(-35.66, 11.08) * mm, v(-35.65, 11.08) * mm, v(-35.65, 11.14) * mm]});
            skFitSpline(sketch, "E429", {"points": [v(-35.65, 11.14) * mm, v(-35.65, 11.16) * mm, v(-35.65, 11.17) * mm, v(-35.65, 11.18) * mm]});
            skFitSpline(sketch, "E430", {"points": [v(-35.65, 11.18) * mm, v(-35.65, 11.37) * mm, v(-35.65, 11.57) * mm, v(-35.65, 11.76) * mm]});
            skFitSpline(sketch, "E431", {"points": [v(-35.65, 11.76) * mm, v(-35.65, 11.79) * mm, v(-35.66, 11.8) * mm, v(-35.7, 11.8) * mm]});
            skFitSpline(sketch, "E432", {"points": [v(-35.7, 11.8) * mm, v(-35.73, 11.8) * mm, v(-35.77, 11.8) * mm, v(-35.81, 11.8) * mm]});
            skFitSpline(sketch, "E433", {"points": [v(-35.81, 11.8) * mm, v(-35.89, 11.8) * mm, v(-35.88, 11.8) * mm, v(-35.88, 11.74) * mm]});
            skFitSpline(sketch, "E434", {"points": [v(-35.88, 11.74) * mm, v(-35.88, 11.61) * mm, v(-35.88, 11.48) * mm, v(-35.88, 11.36) * mm]});
            skFitSpline(sketch, "E435", {"points": [v(-41.1, 11.49) * mm, v(-41.12, 11.5) * mm, v(-41.13, 11.53) * mm, v(-41.14, 11.54) * mm]});
            skFitSpline(sketch, "E436", {"points": [v(-41.14, 11.54) * mm, v(-41.2, 11.62) * mm, v(-41.24, 11.7) * mm, v(-41.29, 11.77) * mm]});
            skFitSpline(sketch, "E437", {"points": [v(-41.29, 11.77) * mm, v(-41.3, 11.78) * mm, v(-41.3, 11.8) * mm, v(-41.33, 11.8) * mm]});
            skFitSpline(sketch, "E438", {"points": [v(-41.33, 11.8) * mm, v(-41.4, 11.8) * mm, v(-41.48, 11.8) * mm, v(-41.55, 11.8) * mm]});
            skFitSpline(sketch, "E439", {"points": [v(-41.55, 11.8) * mm, v(-41.55, 11.78) * mm, v(-41.54, 11.78) * mm, v(-41.54, 11.77) * mm]});
            skFitSpline(sketch, "E440", {"points": [v(-41.54, 11.77) * mm, v(-41.44, 11.62) * mm, v(-41.34, 11.47) * mm, v(-41.25, 11.33) * mm]});
            skFitSpline(sketch, "E441", {"points": [v(-41.25, 11.33) * mm, v(-41.23, 11.3) * mm, v(-41.22, 11.27) * mm, v(-41.22, 11.24) * mm]});
            skFitSpline(sketch, "E442", {"points": [v(-41.22, 11.24) * mm, v(-41.22, 11.14) * mm, v(-41.22, 11.04) * mm, v(-41.22, 10.95) * mm]});
            skFitSpline(sketch, "E443", {"points": [v(-41.22, 10.95) * mm, v(-41.22, 10.92) * mm, v(-41.2, 10.91) * mm, v(-41.18, 10.91) * mm]});
            skFitSpline(sketch, "E444", {"points": [v(-41.18, 10.91) * mm, v(-41.13, 10.91) * mm, v(-41.08, 10.91) * mm, v(-41.03, 10.91) * mm]});
            skFitSpline(sketch, "E445", {"points": [v(-41.03, 10.91) * mm, v(-41, 10.9) * mm, v(-40.99, 10.92) * mm, v(-40.99, 10.96) * mm]});
            skFitSpline(sketch, "E446", {"points": [v(-40.99, 10.96) * mm, v(-41, 11.05) * mm, v(-40.99, 11.14) * mm, v(-41, 11.24) * mm]});
            skFitSpline(sketch, "E447", {"points": [v(-41, 11.24) * mm, v(-41, 11.27) * mm, v(-40.98, 11.3) * mm, v(-40.96, 11.33) * mm]});
            skFitSpline(sketch, "E448", {"points": [v(-40.96, 11.33) * mm, v(-40.87, 11.46) * mm, v(-40.78, 11.6) * mm, v(-40.7, 11.74) * mm]});
            skFitSpline(sketch, "E449", {"points": [v(-40.7, 11.74) * mm, v(-40.68, 11.76) * mm, v(-40.66, 11.77) * mm, v(-40.66, 11.8) * mm]});
            skFitSpline(sketch, "E450", {"points": [v(-40.66, 11.8) * mm, v(-40.74, 11.8) * mm, v(-40.8, 11.8) * mm, v(-40.88, 11.8) * mm]});
            skFitSpline(sketch, "E451", {"points": [v(-40.88, 11.8) * mm, v(-40.9, 11.8) * mm, v(-40.9, 11.79) * mm, v(-40.92, 11.78) * mm]});
            skFitSpline(sketch, "E452", {"points": [v(-40.92, 11.78) * mm, v(-40.95, 11.73) * mm, v(-40.98, 11.68) * mm, v(-41, 11.63) * mm]});
            skFitSpline(sketch, "E453", {"points": [v(-41, 11.63) * mm, v(-41.04, 11.59) * mm, v(-41.07, 11.53) * mm, v(-41.1, 11.49) * mm]});
            skFitSpline(sketch, "E454", {"points": [v(-38.22, 11.8) * mm, v(-38.3, 11.8) * mm, v(-38.4, 11.8) * mm, v(-38.48, 11.8) * mm]});
            skFitSpline(sketch, "E455", {"points": [v(-38.48, 11.8) * mm, v(-38.51, 11.8) * mm, v(-38.53, 11.8) * mm, v(-38.53, 11.76) * mm]});
            skFitSpline(sketch, "E456", {"points": [v(-38.53, 11.76) * mm, v(-38.52, 11.5) * mm, v(-38.52, 11.22) * mm, v(-38.53, 10.95) * mm]});
            skFitSpline(sketch, "E457", {"points": [v(-38.53, 10.95) * mm, v(-38.53, 10.92) * mm, v(-38.52, 10.91) * mm, v(-38.49, 10.91) * mm]});
            skFitSpline(sketch, "E458", {"points": [v(-38.49, 10.91) * mm, v(-38.44, 10.91) * mm, v(-38.39, 10.92) * mm, v(-38.34, 10.91) * mm]});
            skFitSpline(sketch, "E459", {"points": [v(-38.34, 10.91) * mm, v(-38.3, 10.9) * mm, v(-38.3, 10.93) * mm, v(-38.3, 10.96) * mm]});
            skFitSpline(sketch, "E460", {"points": [v(-38.3, 10.96) * mm, v(-38.3, 11.05) * mm, v(-38.3, 11.15) * mm, v(-38.3, 11.24) * mm]});
            skFitSpline(sketch, "E461", {"points": [v(-38.3, 11.24) * mm, v(-38.3, 11.29) * mm, v(-38.3, 11.29) * mm, v(-38.25, 11.29) * mm]});
            skFitSpline(sketch, "E462", {"points": [v(-38.25, 11.29) * mm, v(-38.19, 11.3) * mm, v(-38.12, 11.29) * mm, v(-38.06, 11.3) * mm]});
            skFitSpline(sketch, "E463", {"points": [v(-38.06, 11.3) * mm, v(-38.02, 11.3) * mm, v(-37.97, 11.27) * mm, v(-37.94, 11.3) * mm]});
            skFitSpline(sketch, "E464", {"points": [v(-37.94, 11.3) * mm, v(-37.91, 11.32) * mm, v(-37.93, 11.38) * mm, v(-37.93, 11.42) * mm]});
            skFitSpline(sketch, "E465", {"points": [v(-37.93, 11.42) * mm, v(-37.93, 11.46) * mm, v(-37.93, 11.46) * mm, v(-37.98, 11.46) * mm]});
            skFitSpline(sketch, "E466", {"points": [v(-37.98, 11.46) * mm, v(-38.06, 11.46) * mm, v(-38.15, 11.46) * mm, v(-38.23, 11.46) * mm]});
            skFitSpline(sketch, "E467", {"points": [v(-38.23, 11.46) * mm, v(-38.31, 11.46) * mm, v(-38.3, 11.45) * mm, v(-38.3, 11.54) * mm]});
            skFitSpline(sketch, "E468", {"points": [v(-38.3, 11.54) * mm, v(-38.3, 11.64) * mm, v(-38.31, 11.63) * mm, v(-38.2, 11.63) * mm]});
            skFitSpline(sketch, "E469", {"points": [v(-38.2, 11.63) * mm, v(-38.12, 11.63) * mm, v(-38.03, 11.63) * mm, v(-37.95, 11.63) * mm]});
            skFitSpline(sketch, "E470", {"points": [v(-37.95, 11.63) * mm, v(-37.92, 11.63) * mm, v(-37.9, 11.64) * mm, v(-37.9, 11.67) * mm]});
            skFitSpline(sketch, "E471", {"points": [v(-37.9, 11.67) * mm, v(-37.91, 11.7) * mm, v(-37.91, 11.73) * mm, v(-37.9, 11.76) * mm]});
            skFitSpline(sketch, "E472", {"points": [v(-37.9, 11.76) * mm, v(-37.9, 11.8) * mm, v(-37.92, 11.8) * mm, v(-37.95, 11.8) * mm]});
            skFitSpline(sketch, "E473", {"points": [v(-37.95, 11.8) * mm, v(-38.04, 11.8) * mm, v(-38.13, 11.8) * mm, v(-38.22, 11.8) * mm]});
            skFitSpline(sketch, "E474", {"points": [v(-29.07, 11.49) * mm, v(-29.07, 11.51) * mm, v(-29.08, 11.52) * mm, v(-29.08, 11.53) * mm]});
            skFitSpline(sketch, "E475", {"points": [v(-29.08, 11.53) * mm, v(-29.08, 11.58) * mm, v(-29.08, 11.58) * mm, v(-29.12, 11.58) * mm]});
            skFitSpline(sketch, "E476", {"points": [v(-29.12, 11.58) * mm, v(-29.16, 11.58) * mm, v(-29.2, 11.58) * mm, v(-29.23, 11.58) * mm]});
            skFitSpline(sketch, "E477", {"points": [v(-29.23, 11.58) * mm, v(-29.29, 11.58) * mm, v(-29.29, 11.58) * mm, v(-29.3, 11.52) * mm]});
            skFitSpline(sketch, "E478", {"points": [v(-29.3, 11.52) * mm, v(-29.3, 11.34) * mm, v(-29.3, 11.15) * mm, v(-29.3, 10.97) * mm]});
            skFitSpline(sketch, "E479", {"points": [v(-29.3, 10.97) * mm, v(-29.3, 10.96) * mm, v(-29.29, 10.95) * mm, v(-29.3, 10.94) * mm]});
            skFitSpline(sketch, "E480", {"points": [v(-29.3, 10.94) * mm, v(-29.3, 10.92) * mm, v(-29.28, 10.91) * mm, v(-29.26, 10.91) * mm]});
            skFitSpline(sketch, "E481", {"points": [v(-29.26, 10.91) * mm, v(-29.21, 10.91) * mm, v(-29.16, 10.91) * mm, v(-29.1, 10.91) * mm]});
            skFitSpline(sketch, "E482", {"points": [v(-29.1, 10.91) * mm, v(-29.09, 10.91) * mm, v(-29.08, 10.92) * mm, v(-29.08, 10.94) * mm]});
            skFitSpline(sketch, "E483", {"points": [v(-29.08, 10.94) * mm, v(-29.08, 10.96) * mm, v(-29.08, 10.98) * mm, v(-29.08, 11) * mm]});
            skFitSpline(sketch, "E484", {"points": [v(-29.08, 11) * mm, v(-29.08, 11.09) * mm, v(-29.08, 11.17) * mm, v(-29.08, 11.25) * mm]});
            skFitSpline(sketch, "E485", {"points": [v(-29.08, 11.25) * mm, v(-29.08, 11.3) * mm, v(-29.07, 11.34) * mm, v(-29.04, 11.38) * mm]});
            skFitSpline(sketch, "E486", {"points": [v(-29.04, 11.38) * mm, v(-29.01, 11.42) * mm, v(-28.96, 11.44) * mm, v(-28.91, 11.43) * mm]});
            skFitSpline(sketch, "E487", {"points": [v(-28.91, 11.43) * mm, v(-28.86, 11.42) * mm, v(-28.84, 11.39) * mm, v(-28.84, 11.32) * mm]});
            skFitSpline(sketch, "E488", {"points": [v(-28.84, 11.32) * mm, v(-28.83, 11.3) * mm, v(-28.83, 11.27) * mm, v(-28.83, 11.24) * mm]});
            skFitSpline(sketch, "E489", {"points": [v(-28.83, 11.24) * mm, v(-28.83, 11.14) * mm, v(-28.83, 11.05) * mm, v(-28.83, 10.96) * mm]});
            skFitSpline(sketch, "E490", {"points": [v(-28.83, 10.96) * mm, v(-28.83, 10.91) * mm, v(-28.83, 10.91) * mm, v(-28.79, 10.91) * mm]});
            skFitSpline(sketch, "E491", {"points": [v(-28.79, 10.91) * mm, v(-28.75, 10.9) * mm, v(-28.7, 10.91) * mm, v(-28.66, 10.91) * mm]});
            skFitSpline(sketch, "E492", {"points": [v(-28.66, 10.91) * mm, v(-28.63, 10.9) * mm, v(-28.62, 10.92) * mm, v(-28.62, 10.96) * mm]});
            skFitSpline(sketch, "E493", {"points": [v(-28.62, 10.96) * mm, v(-28.62, 11.08) * mm, v(-28.62, 11.21) * mm, v(-28.62, 11.34) * mm]});
            skFitSpline(sketch, "E494", {"points": [v(-28.62, 11.34) * mm, v(-28.62, 11.37) * mm, v(-28.62, 11.4) * mm, v(-28.63, 11.42) * mm]});
            skFitSpline(sketch, "E495", {"points": [v(-28.63, 11.42) * mm, v(-28.65, 11.5) * mm, v(-28.69, 11.55) * mm, v(-28.76, 11.58) * mm]});
            skFitSpline(sketch, "E496", {"points": [v(-28.76, 11.58) * mm, v(-28.85, 11.6) * mm, v(-28.94, 11.6) * mm, v(-29.02, 11.53) * mm]});
            skFitSpline(sketch, "E497", {"points": [v(-29.02, 11.53) * mm, v(-29.04, 11.52) * mm, v(-29.05, 11.5) * mm, v(-29.07, 11.49) * mm]});
            skFitSpline(sketch, "E498", {"points": [v(-29.84, 11.6) * mm, v(-29.85, 11.6) * mm, v(-29.87, 11.6) * mm, v(-29.88, 11.6) * mm]});
            skFitSpline(sketch, "E499", {"points": [v(-29.88, 11.6) * mm, v(-30.06, 11.58) * mm, v(-30.17, 11.48) * mm, v(-30.2, 11.32) * mm]});
            skFitSpline(sketch, "E500", {"points": [v(-30.2, 11.32) * mm, v(-30.21, 11.26) * mm, v(-30.2, 11.19) * mm, v(-30.2, 11.13) * mm]});
            skFitSpline(sketch, "E501", {"points": [v(-30.2, 11.13) * mm, v(-30.16, 11.03) * mm, v(-30.1, 10.96) * mm, v(-30, 10.92) * mm]});
            skFitSpline(sketch, "E502", {"points": [v(-30, 10.92) * mm, v(-29.94, 10.9) * mm, v(-29.88, 10.89) * mm, v(-29.8, 10.9) * mm]});
            skFitSpline(sketch, "E503", {"points": [v(-29.8, 10.9) * mm, v(-29.62, 10.9) * mm, v(-29.5, 11) * mm, v(-29.48, 11.16) * mm]});
            skFitSpline(sketch, "E504", {"points": [v(-29.48, 11.16) * mm, v(-29.47, 11.22) * mm, v(-29.47, 11.29) * mm, v(-29.49, 11.35) * mm]});
            skFitSpline(sketch, "E505", {"points": [v(-29.49, 11.35) * mm, v(-29.52, 11.47) * mm, v(-29.6, 11.54) * mm, v(-29.71, 11.58) * mm]});
            skFitSpline(sketch, "E506", {"points": [v(-29.71, 11.58) * mm, v(-29.75, 11.59) * mm, v(-29.8, 11.6) * mm, v(-29.84, 11.6) * mm]});
            skFitSpline(sketch, "E507", {"points": [v(-26.24, 11.11) * mm, v(-26.28, 11.1) * mm, v(-26.3, 11.09) * mm, v(-26.32, 11.08) * mm]});
            skFitSpline(sketch, "E508", {"points": [v(-26.32, 11.08) * mm, v(-26.4, 11.05) * mm, v(-26.47, 11.03) * mm, v(-26.55, 11.03) * mm]});
            skFitSpline(sketch, "E509", {"points": [v(-26.55, 11.03) * mm, v(-26.6, 11.04) * mm, v(-26.65, 11.06) * mm, v(-26.69, 11.1) * mm]});
            skFitSpline(sketch, "E510", {"points": [v(-26.69, 11.1) * mm, v(-26.7, 11.13) * mm, v(-26.72, 11.15) * mm, v(-26.7, 11.18) * mm]});
            skFitSpline(sketch, "E511", {"points": [v(-26.7, 11.18) * mm, v(-26.7, 11.2) * mm, v(-26.67, 11.18) * mm, v(-26.65, 11.19) * mm]});
            skFitSpline(sketch, "E512", {"points": [v(-26.65, 11.19) * mm, v(-26.63, 11.19) * mm, v(-26.61, 11.19) * mm, v(-26.6, 11.19) * mm]});
            skLineSegment(sketch, "E513", {"start": v(-28.37, 11.23) * mm, "end": v(-28.37, 11.23) * mm});
            skFitSpline(sketch, "E514", {"points": [v(-26.26, 11.19) * mm, v(-26.24, 11.19) * mm, v(-26.22, 11.18) * mm, v(-26.22, 11.21) * mm]});
            skFitSpline(sketch, "E515", {"points": [v(-26.22, 11.21) * mm, v(-26.21, 11.33) * mm, v(-26.23, 11.43) * mm, v(-26.33, 11.51) * mm]});
            skFitSpline(sketch, "E516", {"points": [v(-26.33, 11.51) * mm, v(-26.47, 11.64) * mm, v(-26.74, 11.61) * mm, v(-26.86, 11.47) * mm]});
            skFitSpline(sketch, "E517", {"points": [v(-26.86, 11.47) * mm, v(-26.9, 11.4) * mm, v(-26.93, 11.34) * mm, v(-26.93, 11.26) * mm]});
            skFitSpline(sketch, "E518", {"points": [v(-26.93, 11.26) * mm, v(-26.94, 11.05) * mm, v(-26.83, 10.93) * mm, v(-26.64, 10.9) * mm]});
            skFitSpline(sketch, "E519", {"points": [v(-26.64, 10.9) * mm, v(-26.54, 10.88) * mm, v(-26.44, 10.9) * mm, v(-26.35, 10.92) * mm]});
            skFitSpline(sketch, "E520", {"points": [v(-26.35, 10.92) * mm, v(-26.24, 10.94) * mm, v(-26.24, 10.94) * mm, v(-26.24, 11.04) * mm]});
            skFitSpline(sketch, "E521", {"points": [v(-26.24, 11.04) * mm, v(-26.24, 11.06) * mm, v(-26.24, 11.08) * mm, v(-26.24, 11.11) * mm]});
            skFitSpline(sketch, "E522", {"points": [v(-32.3, 11) * mm, v(-32.3, 10.98) * mm, v(-32.3, 10.97) * mm, v(-32.3, 10.96) * mm]});
            skFitSpline(sketch, "E523", {"points": [v(-32.3, 10.96) * mm, v(-32.29, 10.91) * mm, v(-32.29, 10.91) * mm, v(-32.24, 10.91) * mm]});
            skFitSpline(sketch, "E524", {"points": [v(-32.24, 10.91) * mm, v(-32.2, 10.91) * mm, v(-32.15, 10.91) * mm, v(-32.1, 10.91) * mm]});
            skFitSpline(sketch, "E525", {"points": [v(-32.1, 10.91) * mm, v(-32.09, 10.91) * mm, v(-32.08, 10.92) * mm, v(-32.08, 10.94) * mm]});
            skFitSpline(sketch, "E526", {"points": [v(-32.08, 10.94) * mm, v(-32.08, 11.08) * mm, v(-32.07, 11.21) * mm, v(-32.08, 11.35) * mm]});
            skFitSpline(sketch, "E527", {"points": [v(-32.08, 11.35) * mm, v(-32.09, 11.48) * mm, v(-32.16, 11.55) * mm, v(-32.27, 11.58) * mm]});
            skFitSpline(sketch, "E528", {"points": [v(-32.27, 11.58) * mm, v(-32.4, 11.6) * mm, v(-32.54, 11.59) * mm, v(-32.67, 11.57) * mm]});
            skFitSpline(sketch, "E529", {"points": [v(-32.67, 11.57) * mm, v(-32.68, 11.56) * mm, v(-32.7, 11.55) * mm, v(-32.7, 11.53) * mm]});
            skFitSpline(sketch, "E530", {"points": [v(-32.7, 11.53) * mm, v(-32.7, 11.5) * mm, v(-32.7, 11.45) * mm, v(-32.7, 11.4) * mm]});
            skFitSpline(sketch, "E531", {"points": [v(-32.7, 11.4) * mm, v(-32.66, 11.4) * mm, v(-32.65, 11.42) * mm, v(-32.63, 11.42) * mm]});
            skFitSpline(sketch, "E532", {"points": [v(-32.63, 11.42) * mm, v(-32.56, 11.45) * mm, v(-32.48, 11.45) * mm, v(-32.4, 11.45) * mm]});
            skFitSpline(sketch, "E533", {"points": [v(-32.4, 11.45) * mm, v(-32.36, 11.44) * mm, v(-32.32, 11.43) * mm, v(-32.3, 11.39) * mm]});
            skFitSpline(sketch, "E534", {"points": [v(-32.3, 11.39) * mm, v(-32.29, 11.35) * mm, v(-32.3, 11.34) * mm, v(-32.34, 11.33) * mm]});
            skFitSpline(sketch, "E535", {"points": [v(-32.34, 11.33) * mm, v(-32.39, 11.33) * mm, v(-32.43, 11.33) * mm, v(-32.48, 11.33) * mm]});
            skFitSpline(sketch, "E536", {"points": [v(-32.48, 11.33) * mm, v(-32.53, 11.33) * mm, v(-32.58, 11.32) * mm, v(-32.62, 11.3) * mm]});
            skFitSpline(sketch, "E537", {"points": [v(-32.62, 11.3) * mm, v(-32.7, 11.27) * mm, v(-32.75, 11.2) * mm, v(-32.75, 11.1) * mm]});
            skFitSpline(sketch, "E538", {"points": [v(-32.75, 11.1) * mm, v(-32.75, 11.01) * mm, v(-32.7, 10.93) * mm, v(-32.6, 10.9) * mm]});
            skFitSpline(sketch, "E539", {"points": [v(-32.6, 10.9) * mm, v(-32.56, 10.9) * mm, v(-32.52, 10.89) * mm, v(-32.47, 10.9) * mm]});
            skFitSpline(sketch, "E540", {"points": [v(-32.47, 10.9) * mm, v(-32.4, 10.9) * mm, v(-32.35, 10.94) * mm, v(-32.3, 11) * mm]});
            skFitSpline(sketch, "E541", {"points": [v(-24.05, 11.1) * mm, v(-24.08, 11.1) * mm, v(-24.1, 11.09) * mm, v(-24.12, 11.08) * mm]});
            skFitSpline(sketch, "E542", {"points": [v(-24.12, 11.08) * mm, v(-24.2, 11.05) * mm, v(-24.28, 11.03) * mm, v(-24.36, 11.03) * mm]});
            skFitSpline(sketch, "E543", {"points": [v(-24.36, 11.03) * mm, v(-24.42, 11.04) * mm, v(-24.47, 11.06) * mm, v(-24.5, 11.13) * mm]});
            skFitSpline(sketch, "E544", {"points": [v(-24.5, 11.13) * mm, v(-24.52, 11.18) * mm, v(-24.52, 11.19) * mm, v(-24.46, 11.19) * mm]});
            skFitSpline(sketch, "E545", {"points": [v(-24.46, 11.19) * mm, v(-24.34, 11.19) * mm, v(-24.23, 11.19) * mm, v(-24.1, 11.19) * mm]});
            skFitSpline(sketch, "E546", {"points": [v(-24.1, 11.19) * mm, v(-24.01, 11.19) * mm, v(-24.01, 11.19) * mm, v(-24.02, 11.28) * mm]});
            skFitSpline(sketch, "E547", {"points": [v(-24.02, 11.28) * mm, v(-24.03, 11.44) * mm, v(-24.13, 11.55) * mm, v(-24.28, 11.58) * mm]});
            skFitSpline(sketch, "E548", {"points": [v(-24.28, 11.58) * mm, v(-24.36, 11.6) * mm, v(-24.44, 11.6) * mm, v(-24.5, 11.57) * mm]});
            skFitSpline(sketch, "E549", {"points": [v(-24.5, 11.57) * mm, v(-24.63, 11.53) * mm, v(-24.7, 11.45) * mm, v(-24.73, 11.33) * mm]});
            skFitSpline(sketch, "E550", {"points": [v(-24.73, 11.33) * mm, v(-24.73, 11.28) * mm, v(-24.74, 11.24) * mm, v(-24.73, 11.2) * mm]});
            skFitSpline(sketch, "E551", {"points": [v(-24.73, 11.2) * mm, v(-24.72, 11.04) * mm, v(-24.63, 10.94) * mm, v(-24.49, 10.9) * mm]});
            skFitSpline(sketch, "E552", {"points": [v(-24.49, 10.9) * mm, v(-24.35, 10.87) * mm, v(-24.21, 10.9) * mm, v(-24.08, 10.94) * mm]});
            skFitSpline(sketch, "E553", {"points": [v(-24.08, 10.94) * mm, v(-24.06, 10.95) * mm, v(-24.05, 10.96) * mm, v(-24.05, 10.98) * mm]});
            skFitSpline(sketch, "E554", {"points": [v(-24.05, 10.98) * mm, v(-24.05, 11.02) * mm, v(-24.05, 11.06) * mm, v(-24.05, 11.1) * mm]});
            skFitSpline(sketch, "E555", {"points": [v(-27.56, 11.5) * mm, v(-27.57, 11.51) * mm, v(-27.57, 11.52) * mm, v(-27.57, 11.53) * mm]});
            skFitSpline(sketch, "E556", {"points": [v(-27.57, 11.53) * mm, v(-27.57, 11.57) * mm, v(-27.58, 11.58) * mm, v(-27.61, 11.58) * mm]});
            skFitSpline(sketch, "E557", {"points": [v(-27.61, 11.58) * mm, v(-27.66, 11.58) * mm, v(-27.7, 11.58) * mm, v(-27.75, 11.58) * mm]});
            skFitSpline(sketch, "E558", {"points": [v(-27.75, 11.58) * mm, v(-27.77, 11.58) * mm, v(-27.78, 11.57) * mm, v(-27.78, 11.55) * mm]});
            skFitSpline(sketch, "E559", {"points": [v(-27.78, 11.55) * mm, v(-27.78, 11.53) * mm, v(-27.78, 11.52) * mm, v(-27.78, 11.5) * mm]});
            skFitSpline(sketch, "E560", {"points": [v(-27.78, 11.5) * mm, v(-27.78, 11.26) * mm, v(-27.78, 11.02) * mm, v(-27.78, 10.78) * mm]});
            skFitSpline(sketch, "E561", {"points": [v(-27.78, 10.78) * mm, v(-27.78, 10.74) * mm, v(-27.8, 10.7) * mm, v(-27.77, 10.67) * mm]});
            skFitSpline(sketch, "E562", {"points": [v(-27.77, 10.67) * mm, v(-27.75, 10.64) * mm, v(-27.7, 10.66) * mm, v(-27.66, 10.66) * mm]});
            skFitSpline(sketch, "E563", {"points": [v(-27.66, 10.66) * mm, v(-27.57, 10.65) * mm, v(-27.57, 10.66) * mm, v(-27.57, 10.74) * mm]});
            skLineSegment(sketch, "E564", {"start": v(-26.6, 11.19) * mm, "end": v(-26.26, 11.19) * mm});
            skFitSpline(sketch, "E565", {"points": [v(-27.57, 10.99) * mm, v(-27.55, 10.99) * mm, v(-27.54, 10.97) * mm, v(-27.53, 10.97) * mm]});
            skFitSpline(sketch, "E566", {"points": [v(-27.53, 10.97) * mm, v(-27.43, 10.86) * mm, v(-27.21, 10.86) * mm, v(-27.12, 11.03) * mm]});
            skFitSpline(sketch, "E567", {"points": [v(-27.12, 11.03) * mm, v(-27.04, 11.18) * mm, v(-27.04, 11.33) * mm, v(-27.13, 11.47) * mm]});
            skFitSpline(sketch, "E568", {"points": [v(-27.13, 11.47) * mm, v(-27.2, 11.58) * mm, v(-27.33, 11.62) * mm, v(-27.44, 11.58) * mm]});
            skFitSpline(sketch, "E569", {"points": [v(-27.44, 11.58) * mm, v(-27.49, 11.56) * mm, v(-27.52, 11.53) * mm, v(-27.56, 11.5) * mm]});
            skFitSpline(sketch, "E570", {"points": [v(-35.18, 10.91) * mm, v(-35.1, 10.91) * mm, v(-35.04, 10.91) * mm, v(-34.98, 10.91) * mm]});
            skFitSpline(sketch, "E571", {"points": [v(-34.98, 10.91) * mm, v(-34.96, 10.91) * mm, v(-34.95, 10.92) * mm, v(-34.94, 10.94) * mm]});
            skFitSpline(sketch, "E572", {"points": [v(-34.94, 10.94) * mm, v(-34.93, 10.97) * mm, v(-34.91, 11) * mm, v(-34.9, 11.04) * mm]});
            skFitSpline(sketch, "E573", {"points": [v(-34.9, 11.04) * mm, v(-34.9, 11.06) * mm, v(-34.89, 11.07) * mm, v(-34.86, 11.07) * mm]});
            skFitSpline(sketch, "E574", {"points": [v(-34.86, 11.07) * mm, v(-34.76, 11.07) * mm, v(-34.66, 11.07) * mm, v(-34.56, 11.07) * mm]});
            skFitSpline(sketch, "E575", {"points": [v(-34.56, 11.07) * mm, v(-34.54, 11.07) * mm, v(-34.53, 11.07) * mm, v(-34.52, 11.05) * mm]});
            skFitSpline(sketch, "E576", {"points": [v(-34.52, 11.05) * mm, v(-34.51, 11.01) * mm, v(-34.5, 10.98) * mm, v(-34.49, 10.94) * mm]});
            skFitSpline(sketch, "E577", {"points": [v(-34.49, 10.94) * mm, v(-34.48, 10.93) * mm, v(-34.48, 10.91) * mm, v(-34.46, 10.91) * mm]});
            skFitSpline(sketch, "E578", {"points": [v(-34.46, 10.91) * mm, v(-34.4, 10.91) * mm, v(-34.32, 10.9) * mm, v(-34.25, 10.92) * mm]});
            skFitSpline(sketch, "E579", {"points": [v(-34.25, 10.92) * mm, v(-34.27, 10.97) * mm, v(-34.29, 11.02) * mm, v(-34.3, 11.06) * mm]});
            skFitSpline(sketch, "E580", {"points": [v(-34.3, 11.06) * mm, v(-34.39, 11.3) * mm, v(-34.47, 11.52) * mm, v(-34.56, 11.75) * mm]});
            skFitSpline(sketch, "E581", {"points": [v(-34.56, 11.75) * mm, v(-34.58, 11.81) * mm, v(-34.57, 11.8) * mm, v(-34.63, 11.8) * mm]});
            skFitSpline(sketch, "E582", {"points": [v(-34.63, 11.8) * mm, v(-34.69, 11.8) * mm, v(-34.74, 11.8) * mm, v(-34.8, 11.8) * mm]});
            skFitSpline(sketch, "E583", {"points": [v(-34.8, 11.8) * mm, v(-34.84, 11.8) * mm, v(-34.85, 11.8) * mm, v(-34.87, 11.76) * mm]});
            skFitSpline(sketch, "E584", {"points": [v(-34.87, 11.76) * mm, v(-34.94, 11.56) * mm, v(-35, 11.37) * mm, v(-35.08, 11.17) * mm]});
            skFitSpline(sketch, "E585", {"points": [v(-35.08, 11.17) * mm, v(-35.11, 11.09) * mm, v(-35.14, 11) * mm, v(-35.18, 10.91) * mm]});
            skFitSpline(sketch, "E586", {"points": [v(-37.91, 10.91) * mm, v(-37.87, 10.91) * mm, v(-37.84, 10.91) * mm, v(-37.8, 10.91) * mm]});
            skFitSpline(sketch, "E587", {"points": [v(-37.8, 10.91) * mm, v(-37.77, 10.91) * mm, v(-37.72, 10.9) * mm, v(-37.69, 10.92) * mm]});
            skFitSpline(sketch, "E588", {"points": [v(-37.69, 10.92) * mm, v(-37.65, 10.94) * mm, v(-37.66, 11) * mm, v(-37.64, 11.03) * mm]});
            skFitSpline(sketch, "E589", {"points": [v(-37.64, 11.03) * mm, v(-37.64, 11.03) * mm, v(-37.64, 11.04) * mm, v(-37.64, 11.04) * mm]});
            skFitSpline(sketch, "E590", {"points": [v(-37.64, 11.04) * mm, v(-37.63, 11.07) * mm, v(-37.61, 11.07) * mm, v(-37.59, 11.07) * mm]});
            skFitSpline(sketch, "E591", {"points": [v(-37.59, 11.07) * mm, v(-37.5, 11.07) * mm, v(-37.4, 11.07) * mm, v(-37.3, 11.07) * mm]});
            skFitSpline(sketch, "E592", {"points": [v(-37.3, 11.07) * mm, v(-37.27, 11.07) * mm, v(-37.26, 11.07) * mm, v(-37.26, 11.04) * mm]});
            skFitSpline(sketch, "E593", {"points": [v(-37.26, 11.04) * mm, v(-37.25, 11) * mm, v(-37.23, 10.97) * mm, v(-37.22, 10.94) * mm]});
            skFitSpline(sketch, "E594", {"points": [v(-37.22, 10.94) * mm, v(-37.21, 10.92) * mm, v(-37.2, 10.91) * mm, v(-37.19, 10.91) * mm]});
            skFitSpline(sketch, "E595", {"points": [v(-37.19, 10.91) * mm, v(-37.12, 10.91) * mm, v(-37.06, 10.91) * mm, v(-36.98, 10.91) * mm]});
            skFitSpline(sketch, "E596", {"points": [v(-36.98, 10.91) * mm, v(-37.02, 11.02) * mm, v(-37.06, 11.11) * mm, v(-37.1, 11.2) * mm]});
            skFitSpline(sketch, "E597", {"points": [v(-37.1, 11.2) * mm, v(-37.16, 11.39) * mm, v(-37.23, 11.57) * mm, v(-37.3, 11.76) * mm]});
            skFitSpline(sketch, "E598", {"points": [v(-37.3, 11.76) * mm, v(-37.3, 11.8) * mm, v(-37.32, 11.8) * mm, v(-37.35, 11.8) * mm]});
            skFitSpline(sketch, "E599", {"points": [v(-37.35, 11.8) * mm, v(-37.41, 11.8) * mm, v(-37.48, 11.8) * mm, v(-37.54, 11.8) * mm]});
            skFitSpline(sketch, "E600", {"points": [v(-37.54, 11.8) * mm, v(-37.58, 11.8) * mm, v(-37.59, 11.79) * mm, v(-37.6, 11.75) * mm]});
            skFitSpline(sketch, "E601", {"points": [v(-37.6, 11.75) * mm, v(-37.66, 11.58) * mm, v(-37.72, 11.41) * mm, v(-37.79, 11.24) * mm]});
            skFitSpline(sketch, "E602", {"points": [v(-37.79, 11.24) * mm, v(-37.83, 11.14) * mm, v(-37.87, 11.03) * mm, v(-37.91, 10.91) * mm]});
            skFitSpline(sketch, "E603", {"points": [v(-39.93, 11.47) * mm, v(-39.96, 11.45) * mm, v(-40, 11.43) * mm, v(-40.02, 11.4) * mm]});
            skFitSpline(sketch, "E604", {"points": [v(-40.02, 11.4) * mm, v(-40.18, 11.24) * mm, v(-40.12, 10.99) * mm, v(-39.9, 10.92) * mm]});
            skFitSpline(sketch, "E605", {"points": [v(-39.9, 10.92) * mm, v(-39.77, 10.87) * mm, v(-39.64, 10.89) * mm, v(-39.52, 10.95) * mm]});
            skFitSpline(sketch, "E606", {"points": [v(-39.52, 10.95) * mm, v(-39.5, 10.97) * mm, v(-39.47, 10.97) * mm, v(-39.45, 10.94) * mm]});
            skFitSpline(sketch, "E607", {"points": [v(-39.45, 10.94) * mm, v(-39.44, 10.91) * mm, v(-39.4, 10.91) * mm, v(-39.38, 10.91) * mm]});
            skFitSpline(sketch, "E608", {"points": [v(-39.38, 10.91) * mm, v(-39.33, 10.91) * mm, v(-39.28, 10.91) * mm, v(-39.23, 10.91) * mm]});
            skFitSpline(sketch, "E609", {"points": [v(-39.23, 10.91) * mm, v(-39.21, 10.91) * mm, v(-39.2, 10.9) * mm, v(-39.18, 10.92) * mm]});
            skFitSpline(sketch, "E610", {"points": [v(-39.18, 10.92) * mm, v(-39.23, 10.97) * mm, v(-39.27, 11.01) * mm, v(-39.3, 11.06) * mm]});
            skFitSpline(sketch, "E611", {"points": [v(-39.3, 11.06) * mm, v(-39.34, 11.1) * mm, v(-39.34, 11.1) * mm, v(-39.31, 11.14) * mm]});
            skFitSpline(sketch, "E612", {"points": [v(-39.31, 11.14) * mm, v(-39.25, 11.23) * mm, v(-39.22, 11.33) * mm, v(-39.21, 11.44) * mm]});
            skFitSpline(sketch, "E613", {"points": [v(-39.21, 11.44) * mm, v(-39.26, 11.44) * mm, v(-39.3, 11.44) * mm, v(-39.35, 11.44) * mm]});
            skFitSpline(sketch, "E614", {"points": [v(-39.35, 11.44) * mm, v(-39.38, 11.44) * mm, v(-39.4, 11.44) * mm, v(-39.4, 11.4) * mm]});
            skFitSpline(sketch, "E615", {"points": [v(-39.4, 11.4) * mm, v(-39.4, 11.35) * mm, v(-39.42, 11.29) * mm, v(-39.47, 11.23) * mm]});
            skFitSpline(sketch, "E616", {"points": [v(-39.47, 11.23) * mm, v(-39.56, 11.34) * mm, v(-39.65, 11.44) * mm, v(-39.74, 11.54) * mm]});
            skFitSpline(sketch, "E617", {"points": [v(-39.74, 11.54) * mm, v(-39.74, 11.55) * mm, v(-39.75, 11.55) * mm, v(-39.75, 11.56) * mm]});
            skFitSpline(sketch, "E618", {"points": [v(-39.75, 11.56) * mm, v(-39.78, 11.62) * mm, v(-39.76, 11.66) * mm, v(-39.7, 11.67) * mm]});
            skFitSpline(sketch, "E619", {"points": [v(-39.7, 11.67) * mm, v(-39.66, 11.67) * mm, v(-39.63, 11.67) * mm, v(-39.6, 11.66) * mm]});
            skFitSpline(sketch, "E620", {"points": [v(-39.6, 11.66) * mm, v(-39.55, 11.65) * mm, v(-39.51, 11.64) * mm, v(-39.46, 11.62) * mm]});
            skFitSpline(sketch, "E621", {"points": [v(-39.46, 11.62) * mm, v(-39.46, 11.67) * mm, v(-39.46, 11.7) * mm, v(-39.46, 11.75) * mm]});
            skFitSpline(sketch, "E622", {"points": [v(-39.46, 11.75) * mm, v(-39.46, 11.78) * mm, v(-39.47, 11.79) * mm, v(-39.5, 11.79) * mm]});
            skFitSpline(sketch, "E623", {"points": [v(-39.5, 11.79) * mm, v(-39.54, 11.8) * mm, v(-39.58, 11.8) * mm, v(-39.63, 11.81) * mm]});
            skFitSpline(sketch, "E624", {"points": [v(-39.63, 11.81) * mm, v(-39.7, 11.82) * mm, v(-39.78, 11.82) * mm, v(-39.85, 11.79) * mm]});
            skFitSpline(sketch, "E625", {"points": [v(-39.85, 11.79) * mm, v(-39.95, 11.74) * mm, v(-40, 11.65) * mm, v(-39.97, 11.55) * mm]});
            skFitSpline(sketch, "E626", {"points": [v(-39.97, 11.55) * mm, v(-39.96, 11.52) * mm, v(-39.94, 11.5) * mm, v(-39.93, 11.47) * mm]});
            skFitSpline(sketch, "E627", {"points": [v(-42.96, 11.35) * mm, v(-42.96, 11.25) * mm, v(-42.96, 11.14) * mm, v(-42.96, 11.04) * mm]});
            skFitSpline(sketch, "E628", {"points": [v(-42.96, 11.04) * mm, v(-42.96, 11) * mm, v(-42.97, 10.95) * mm, v(-42.95, 10.92) * mm]});
            skFitSpline(sketch, "E629", {"points": [v(-42.95, 10.92) * mm, v(-42.92, 10.9) * mm, v(-42.87, 10.91) * mm, v(-42.83, 10.91) * mm]});
            skFitSpline(sketch, "E630", {"points": [v(-42.83, 10.91) * mm, v(-42.71, 10.91) * mm, v(-42.6, 10.9) * mm, v(-42.48, 10.93) * mm]});
            skFitSpline(sketch, "E631", {"points": [v(-42.48, 10.93) * mm, v(-42.27, 10.96) * mm, v(-42.14, 11.1) * mm, v(-42.12, 11.3) * mm]});
            skFitSpline(sketch, "E632", {"points": [v(-42.12, 11.3) * mm, v(-42.1, 11.57) * mm, v(-42.25, 11.76) * mm, v(-42.5, 11.79) * mm]});
            skFitSpline(sketch, "E633", {"points": [v(-42.5, 11.79) * mm, v(-42.64, 11.8) * mm, v(-42.78, 11.8) * mm, v(-42.91, 11.8) * mm]});
            skFitSpline(sketch, "E634", {"points": [v(-42.91, 11.8) * mm, v(-42.95, 11.8) * mm, v(-42.96, 11.8) * mm, v(-42.96, 11.76) * mm]});
            skFitSpline(sketch, "E635", {"points": [v(-42.96, 11.76) * mm, v(-42.95, 11.62) * mm, v(-42.96, 11.49) * mm, v(-42.96, 11.35) * mm]});
            skFitSpline(sketch, "E636", {"points": [v(-36.25, 11.39) * mm, v(-36.15, 11.44) * mm, v(-36.13, 11.52) * mm, v(-36.15, 11.61) * mm]});
            skFitSpline(sketch, "E637", {"points": [v(-36.15, 11.61) * mm, v(-36.16, 11.7) * mm, v(-36.22, 11.75) * mm, v(-36.3, 11.77) * mm]});
            skFitSpline(sketch, "E638", {"points": [v(-36.3, 11.77) * mm, v(-36.35, 11.79) * mm, v(-36.4, 11.8) * mm, v(-36.46, 11.8) * mm]});
            skFitSpline(sketch, "E639", {"points": [v(-36.46, 11.8) * mm, v(-36.57, 11.8) * mm, v(-36.68, 11.8) * mm, v(-36.8, 11.8) * mm]});
            skFitSpline(sketch, "E640", {"points": [v(-36.8, 11.8) * mm, v(-36.83, 11.8) * mm, v(-36.84, 11.79) * mm, v(-36.84, 11.76) * mm]});
            skFitSpline(sketch, "E641", {"points": [v(-36.84, 11.76) * mm, v(-36.83, 11.61) * mm, v(-36.84, 11.47) * mm, v(-36.84, 11.33) * mm]});
            skFitSpline(sketch, "E642", {"points": [v(-36.84, 11.33) * mm, v(-36.84, 11.2) * mm, v(-36.83, 11.08) * mm, v(-36.84, 10.95) * mm]});
            skFitSpline(sketch, "E643", {"points": [v(-36.84, 10.95) * mm, v(-36.84, 10.92) * mm, v(-36.83, 10.9) * mm, v(-36.8, 10.9) * mm]});
            skFitSpline(sketch, "E644", {"points": [v(-36.8, 10.9) * mm, v(-36.66, 10.91) * mm, v(-36.52, 10.91) * mm, v(-36.39, 10.91) * mm]});
            skFitSpline(sketch, "E645", {"points": [v(-36.39, 10.91) * mm, v(-36.34, 10.91) * mm, v(-36.29, 10.92) * mm, v(-36.24, 10.94) * mm]});
            skFitSpline(sketch, "E646", {"points": [v(-36.24, 10.94) * mm, v(-36.19, 10.96) * mm, v(-36.15, 11) * mm, v(-36.12, 11.06) * mm]});
            skFitSpline(sketch, "E647", {"points": [v(-36.12, 11.06) * mm, v(-36.07, 11.18) * mm, v(-36.12, 11.34) * mm, v(-36.23, 11.37) * mm]});
            skFitSpline(sketch, "E648", {"points": [v(-36.23, 11.37) * mm, v(-36.24, 11.38) * mm, v(-36.24, 11.38) * mm, v(-36.25, 11.39) * mm]});
            skFitSpline(sketch, "E649", {"points": [v(-34.1, 11.8) * mm, v(-34.1, 11.51) * mm, v(-34.1, 11.23) * mm, v(-34.1, 10.95) * mm]});
            skFitSpline(sketch, "E650", {"points": [v(-34.1, 10.95) * mm, v(-34.1, 10.92) * mm, v(-34.1, 10.91) * mm, v(-34.06, 10.91) * mm]});
            skFitSpline(sketch, "E651", {"points": [v(-34.06, 10.91) * mm, v(-33.92, 10.91) * mm, v(-33.78, 10.91) * mm, v(-33.64, 10.91) * mm]});
            skFitSpline(sketch, "E652", {"points": [v(-33.64, 10.91) * mm, v(-33.6, 10.91) * mm, v(-33.56, 10.93) * mm, v(-33.52, 10.94) * mm]});
            skFitSpline(sketch, "E653", {"points": [v(-33.52, 10.94) * mm, v(-33.43, 10.97) * mm, v(-33.38, 11.04) * mm, v(-33.37, 11.14) * mm]});
            skFitSpline(sketch, "E654", {"points": [v(-33.37, 11.14) * mm, v(-33.36, 11.24) * mm, v(-33.4, 11.32) * mm, v(-33.49, 11.37) * mm]});
            skFitSpline(sketch, "E655", {"points": [v(-33.49, 11.37) * mm, v(-33.5, 11.38) * mm, v(-33.5, 11.38) * mm, v(-33.5, 11.4) * mm]});
            skFitSpline(sketch, "E656", {"points": [v(-33.5, 11.4) * mm, v(-33.44, 11.43) * mm, v(-33.4, 11.48) * mm, v(-33.4, 11.55) * mm]});
            skFitSpline(sketch, "E657", {"points": [v(-33.4, 11.55) * mm, v(-33.4, 11.69) * mm, v(-33.47, 11.77) * mm, v(-33.61, 11.79) * mm]});
            skFitSpline(sketch, "E658", {"points": [v(-33.61, 11.79) * mm, v(-33.77, 11.81) * mm, v(-33.93, 11.8) * mm, v(-34.1, 11.8) * mm]});
            skFitSpline(sketch, "E659", {"points": [v(-30.9, 11.34) * mm, v(-30.91, 11.36) * mm, v(-30.92, 11.4) * mm, v(-30.94, 11.42) * mm]});
            skFitSpline(sketch, "E660", {"points": [v(-30.94, 11.42) * mm, v(-30.99, 11.53) * mm, v(-31.03, 11.65) * mm, v(-31.08, 11.76) * mm]});
            skFitSpline(sketch, "E661", {"points": [v(-31.08, 11.76) * mm, v(-31.1, 11.78) * mm, v(-31.1, 11.8) * mm, v(-31.12, 11.8) * mm]});
            skFitSpline(sketch, "E662", {"points": [v(-31.12, 11.8) * mm, v(-31.2, 11.8) * mm, v(-31.28, 11.8) * mm, v(-31.36, 11.8) * mm]});
            skFitSpline(sketch, "E663", {"points": [v(-31.36, 11.8) * mm, v(-31.38, 11.8) * mm, v(-31.4, 11.79) * mm, v(-31.39, 11.77) * mm]});
            skFitSpline(sketch, "E664", {"points": [v(-31.39, 11.77) * mm, v(-31.39, 11.76) * mm, v(-31.39, 11.75) * mm, v(-31.39, 11.74) * mm]});
            skFitSpline(sketch, "E665", {"points": [v(-31.39, 11.74) * mm, v(-31.39, 11.48) * mm, v(-31.39, 11.23) * mm, v(-31.39, 10.97) * mm]});
            skFitSpline(sketch, "E666", {"points": [v(-31.39, 10.97) * mm, v(-31.39, 10.95) * mm, v(-31.4, 10.93) * mm, v(-31.38, 10.92) * mm]});
            skFitSpline(sketch, "E667", {"points": [v(-31.38, 10.92) * mm, v(-31.34, 10.9) * mm, v(-31.3, 10.91) * mm, v(-31.25, 10.91) * mm]});
            skFitSpline(sketch, "E668", {"points": [v(-31.25, 10.91) * mm, v(-31.17, 10.9) * mm, v(-31.17, 10.9) * mm, v(-31.17, 10.98) * mm]});
            skFitSpline(sketch, "E669", {"points": [v(-31.17, 10.98) * mm, v(-31.17, 11.15) * mm, v(-31.17, 11.31) * mm, v(-31.17, 11.48) * mm]});
            skFitSpline(sketch, "E670", {"points": [v(-31.17, 11.48) * mm, v(-31.17, 11.5) * mm, v(-31.18, 11.5) * mm, v(-31.16, 11.53) * mm]});
            skFitSpline(sketch, "E671", {"points": [v(-31.16, 11.53) * mm, v(-31.1, 11.4) * mm, v(-31.06, 11.29) * mm, v(-31, 11.17) * mm]});
            skFitSpline(sketch, "E672", {"points": [v(-31, 11.17) * mm, v(-30.97, 11.08) * mm, v(-30.97, 11.08) * mm, v(-30.87, 11.08) * mm]});
            skFitSpline(sketch, "E673", {"points": [v(-30.87, 11.08) * mm, v(-30.83, 11.08) * mm, v(-30.82, 11.1) * mm, v(-30.8, 11.12) * mm]});
            skFitSpline(sketch, "E674", {"points": [v(-30.8, 11.12) * mm, v(-30.77, 11.2) * mm, v(-30.73, 11.29) * mm, v(-30.7, 11.37) * mm]});
            skFitSpline(sketch, "E675", {"points": [v(-30.7, 11.37) * mm, v(-30.67, 11.43) * mm, v(-30.65, 11.48) * mm, v(-30.63, 11.53) * mm]});
            skFitSpline(sketch, "E676", {"points": [v(-30.63, 11.53) * mm, v(-30.61, 11.52) * mm, v(-30.62, 11.5) * mm, v(-30.62, 11.5) * mm]});
            skFitSpline(sketch, "E677", {"points": [v(-30.62, 11.5) * mm, v(-30.62, 11.33) * mm, v(-30.62, 11.16) * mm, v(-30.62, 11) * mm]});
            skFitSpline(sketch, "E678", {"points": [v(-30.62, 11) * mm, v(-30.62, 10.9) * mm, v(-30.63, 10.9) * mm, v(-30.54, 10.91) * mm]});
            skFitSpline(sketch, "E679", {"points": [v(-30.54, 10.91) * mm, v(-30.5, 10.91) * mm, v(-30.44, 10.9) * mm, v(-30.41, 10.92) * mm]});
            skFitSpline(sketch, "E680", {"points": [v(-30.41, 10.92) * mm, v(-30.38, 10.95) * mm, v(-30.4, 11) * mm, v(-30.4, 11.05) * mm]});
            skFitSpline(sketch, "E681", {"points": [v(-30.4, 11.05) * mm, v(-30.4, 11.28) * mm, v(-30.4, 11.51) * mm, v(-30.4, 11.75) * mm]});
            skFitSpline(sketch, "E682", {"points": [v(-30.4, 11.75) * mm, v(-30.4, 11.8) * mm, v(-30.4, 11.8) * mm, v(-30.45, 11.8) * mm]});
            skFitSpline(sketch, "E683", {"points": [v(-30.45, 11.8) * mm, v(-30.52, 11.8) * mm, v(-30.58, 11.8) * mm, v(-30.64, 11.8) * mm]});
            skFitSpline(sketch, "E684", {"points": [v(-30.64, 11.8) * mm, v(-30.68, 11.8) * mm, v(-30.7, 11.79) * mm, v(-30.71, 11.76) * mm]});
            skFitSpline(sketch, "E685", {"points": [v(-30.71, 11.76) * mm, v(-30.76, 11.63) * mm, v(-30.81, 11.5) * mm, v(-30.87, 11.39) * mm]});
            skFitSpline(sketch, "E686", {"points": [v(-30.87, 11.39) * mm, v(-30.88, 11.37) * mm, v(-30.88, 11.35) * mm, v(-30.9, 11.34) * mm]});
            skLineSegment(sketch, "E687", {"start": v(-27.57, 10.74) * mm, "end": v(-27.57, 10.99) * mm});
            skFitSpline(sketch, "E688", {"points": [v(-41.8, 18.46) * mm, v(-41.8, 18.48) * mm, v(-41.8, 18.5) * mm, v(-41.8, 18.51) * mm]});
            skFitSpline(sketch, "E689", {"points": [v(-41.8, 18.51) * mm, v(-41.8, 18.53) * mm, v(-41.8, 18.55) * mm, v(-41.83, 18.54) * mm]});
            skFitSpline(sketch, "E690", {"points": [v(-41.83, 18.54) * mm, v(-41.84, 18.54) * mm, v(-41.86, 18.54) * mm, v(-41.87, 18.54) * mm]});
            skFitSpline(sketch, "E691", {"points": [v(-41.87, 18.54) * mm, v(-42.2, 18.54) * mm, v(-42.54, 18.54) * mm, v(-42.87, 18.54) * mm]});
            skFitSpline(sketch, "E692", {"points": [v(-42.87, 18.54) * mm, v(-42.97, 18.54) * mm, v(-42.96, 18.56) * mm, v(-42.96, 18.46) * mm]});
            skFitSpline(sketch, "E693", {"points": [v(-42.96, 18.46) * mm, v(-42.96, 17.4) * mm, v(-42.96, 16.33) * mm, v(-42.96, 15.26) * mm]});
            skFitSpline(sketch, "E694", {"points": [v(-42.96, 15.26) * mm, v(-42.96, 14.58) * mm, v(-42.96, 13.9) * mm, v(-42.96, 13.2) * mm]});
            skFitSpline(sketch, "E695", {"points": [v(-42.96, 13.2) * mm, v(-42.96, 13.13) * mm, v(-42.97, 13.14) * mm, v(-42.89, 13.14) * mm]});
            skFitSpline(sketch, "E696", {"points": [v(-42.89, 13.14) * mm, v(-42.6, 13.14) * mm, v(-42.32, 13.14) * mm, v(-42.03, 13.14) * mm]});
            skLineSegment(sketch, "E697", {"start": v(-41.8, 14.12) * mm, "end": v(-41.8, 14.2) * mm});
            skLineSegment(sketch, "E698", {"start": v(-41.8, 14.2) * mm, "end": v(-41.8, 18.46) * mm});
            skFitSpline(sketch, "E699", {"points": [v(-40.3, 13.14) * mm, v(-40.22, 13.14) * mm, v(-40.22, 13.14) * mm, v(-40.22, 13.21) * mm]});
            skLineSegment(sketch, "E700", {"start": v(-42.03, 13.14) * mm, "end": v(-40.3, 13.14) * mm});
            skFitSpline(sketch, "E701", {"points": [v(-40.22, 14.05) * mm, v(-40.22, 14.06) * mm, v(-40.22, 14.08) * mm, v(-40.22, 14.09) * mm]});
            skFitSpline(sketch, "E702", {"points": [v(-40.22, 14.09) * mm, v(-40.21, 14.11) * mm, v(-40.23, 14.12) * mm, v(-40.25, 14.12) * mm]});
            skFitSpline(sketch, "E703", {"points": [v(-40.25, 14.12) * mm, v(-40.26, 14.12) * mm, v(-40.28, 14.12) * mm, v(-40.3, 14.12) * mm]});
            skLineSegment(sketch, "E704", {"start": v(-40.22, 13.21) * mm, "end": v(-40.22, 14.05) * mm});
            skLineSegment(sketch, "E705", {"start": v(-40.3, 14.12) * mm, "end": v(-41.73, 14.12) * mm});
            skLineSegment(sketch, "E706", {"start": v(-41.73, 14.12) * mm, "end": v(-41.8, 14.12) * mm});
            skLineSegment(sketch, "E707", {"start": v(-41.8, 14.12) * mm, "end": v(-41.8, 14.12) * mm});
            skFitSpline(sketch, "E708", {"points": [v(-30.2, 17.54) * mm, v(-30.12, 17.54) * mm, v(-30.13, 17.54) * mm, v(-30.13, 17.6) * mm]});
            skFitSpline(sketch, "E709", {"points": [v(-30.13, 17.6) * mm, v(-30.13, 17.8) * mm, v(-30.13, 18.01) * mm, v(-30.13, 18.22) * mm]});
            skFitSpline(sketch, "E710", {"points": [v(-30.13, 18.22) * mm, v(-30.13, 18.31) * mm, v(-30.13, 18.4) * mm, v(-30.12, 18.5) * mm]});
            skFitSpline(sketch, "E711", {"points": [v(-30.12, 18.5) * mm, v(-30.12, 18.53) * mm, v(-30.13, 18.55) * mm, v(-30.17, 18.54) * mm]});
            skFitSpline(sketch, "E712", {"points": [v(-30.17, 18.54) * mm, v(-30.17, 18.54) * mm, v(-30.18, 18.54) * mm, v(-30.2, 18.54) * mm]});
            skFitSpline(sketch, "E713", {"points": [v(-30.2, 18.54) * mm, v(-30.76, 18.55) * mm, v(-31.32, 18.55) * mm, v(-31.9, 18.55) * mm]});
            skFitSpline(sketch, "E714", {"points": [v(-31.9, 18.55) * mm, v(-31.98, 18.55) * mm, v(-32.06, 18.53) * mm, v(-32.15, 18.5) * mm]});
            skFitSpline(sketch, "E715", {"points": [v(-32.15, 18.5) * mm, v(-32.4, 18.38) * mm, v(-32.55, 18.19) * mm, v(-32.65, 17.94) * mm]});
            skFitSpline(sketch, "E716", {"points": [v(-32.65, 17.94) * mm, v(-32.75, 17.67) * mm, v(-32.76, 17.4) * mm, v(-32.68, 17.12) * mm]});
            skFitSpline(sketch, "E717", {"points": [v(-32.68, 17.12) * mm, v(-32.63, 16.93) * mm, v(-32.54, 16.75) * mm, v(-32.45, 16.57) * mm]});
            skFitSpline(sketch, "E718", {"points": [v(-32.45, 16.57) * mm, v(-32.3, 16.3) * mm, v(-32.16, 16.05) * mm, v(-32.02, 15.79) * mm]});
            skFitSpline(sketch, "E719", {"points": [v(-32.02, 15.79) * mm, v(-31.71, 15.24) * mm, v(-31.4, 14.7) * mm, v(-31.1, 14.16) * mm]});
            skFitSpline(sketch, "E720", {"points": [v(-31.1, 14.16) * mm, v(-31.1, 14.14) * mm, v(-31.07, 14.12) * mm, v(-31.08, 14.1) * mm]});
            skLineSegment(sketch, "E721", {"start": v(-31.62, 17.54) * mm, "end": v(-31.54, 17.54) * mm});
            skLineSegment(sketch, "E722", {"start": v(-31.54, 17.54) * mm, "end": v(-30.2, 17.54) * mm});
            skFitSpline(sketch, "E723", {"points": [v(-31.45, 14.1) * mm, v(-31.83, 14.1) * mm, v(-32.2, 14.1) * mm, v(-32.6, 14.1) * mm]});
            skFitSpline(sketch, "E724", {"points": [v(-32.6, 14.1) * mm, v(-32.65, 14.1) * mm, v(-32.65, 14.1) * mm, v(-32.65, 14.03) * mm]});
            skFitSpline(sketch, "E725", {"points": [v(-32.65, 14.03) * mm, v(-32.65, 13.75) * mm, v(-32.65, 13.48) * mm, v(-32.65, 13.2) * mm]});
            skFitSpline(sketch, "E726", {"points": [v(-32.65, 13.2) * mm, v(-32.65, 13.15) * mm, v(-32.65, 13.15) * mm, v(-32.6, 13.15) * mm]});
            skFitSpline(sketch, "E727", {"points": [v(-32.6, 13.15) * mm, v(-32.59, 13.15) * mm, v(-32.57, 13.15) * mm, v(-32.56, 13.15) * mm]});
            skLineSegment(sketch, "E728", {"start": v(-31.08, 14.1) * mm, "end": v(-31.45, 14.1) * mm});
            skFitSpline(sketch, "E729", {"points": [v(-30.96, 13.15) * mm, v(-30.85, 13.15) * mm, v(-30.74, 13.15) * mm, v(-30.64, 13.15) * mm]});
            skFitSpline(sketch, "E730", {"points": [v(-30.64, 13.15) * mm, v(-30.61, 13.15) * mm, v(-30.59, 13.14) * mm, v(-30.57, 13.16) * mm]});
            skFitSpline(sketch, "E731", {"points": [v(-30.57, 13.16) * mm, v(-30.43, 13.26) * mm, v(-30.3, 13.36) * mm, v(-30.22, 13.5) * mm]});
            skFitSpline(sketch, "E732", {"points": [v(-30.22, 13.5) * mm, v(-30.07, 13.78) * mm, v(-29.99, 14.07) * mm, v(-30.04, 14.38) * mm]});
            skFitSpline(sketch, "E733", {"points": [v(-30.04, 14.38) * mm, v(-30.05, 14.5) * mm, v(-30.06, 14.6) * mm, v(-30.1, 14.71) * mm]});
            skFitSpline(sketch, "E734", {"points": [v(-30.1, 14.71) * mm, v(-30.16, 14.85) * mm, v(-30.22, 15) * mm, v(-30.29, 15.13) * mm]});
            skFitSpline(sketch, "E735", {"points": [v(-30.29, 15.13) * mm, v(-30.72, 15.9) * mm, v(-31.15, 16.68) * mm, v(-31.58, 17.45) * mm]});
            skFitSpline(sketch, "E736", {"points": [v(-31.58, 17.45) * mm, v(-31.6, 17.48) * mm, v(-31.6, 17.5) * mm, v(-31.62, 17.54) * mm]});
            skFitSpline(sketch, "E737", {"points": [v(-27.72, 13.45) * mm, v(-27.7, 13.37) * mm, v(-27.67, 13.3) * mm, v(-27.64, 13.22) * mm]});
            skFitSpline(sketch, "E738", {"points": [v(-27.64, 13.22) * mm, v(-27.61, 13.16) * mm, v(-27.63, 13.16) * mm, v(-27.55, 13.16) * mm]});
            skFitSpline(sketch, "E739", {"points": [v(-27.55, 13.16) * mm, v(-27.3, 13.16) * mm, v(-27.06, 13.16) * mm, v(-26.81, 13.16) * mm]});
            skFitSpline(sketch, "E740", {"points": [v(-26.81, 13.16) * mm, v(-26.73, 13.16) * mm, v(-26.74, 13.15) * mm, v(-26.74, 13.23) * mm]});
            skFitSpline(sketch, "E741", {"points": [v(-26.74, 13.23) * mm, v(-26.74, 14.5) * mm, v(-26.74, 15.77) * mm, v(-26.74, 17.04) * mm]});
            skFitSpline(sketch, "E742", {"points": [v(-26.74, 17.04) * mm, v(-26.74, 17.06) * mm, v(-26.74, 17.07) * mm, v(-26.74, 17.09) * mm]});
            skFitSpline(sketch, "E743", {"points": [v(-26.74, 17.09) * mm, v(-26.74, 17.1) * mm, v(-26.75, 17.12) * mm, v(-26.77, 17.12) * mm]});
            skFitSpline(sketch, "E744", {"points": [v(-26.77, 17.12) * mm, v(-26.79, 17.12) * mm, v(-26.8, 17.12) * mm, v(-26.82, 17.12) * mm]});
            skLineSegment(sketch, "E745", {"start": v(-32.56, 13.15) * mm, "end": v(-30.96, 13.15) * mm});
            skFitSpline(sketch, "E746", {"points": [v(-27.78, 17.12) * mm, v(-27.86, 17.12) * mm, v(-27.86, 17.12) * mm, v(-27.86, 17.04) * mm]});
            skFitSpline(sketch, "E747", {"points": [v(-27.86, 17.04) * mm, v(-27.86, 16.08) * mm, v(-27.86, 15.13) * mm, v(-27.86, 14.17) * mm]});
            skFitSpline(sketch, "E748", {"points": [v(-27.86, 14.17) * mm, v(-27.86, 14.14) * mm, v(-27.86, 14.1) * mm, v(-27.86, 14.08) * mm]});
            skFitSpline(sketch, "E749", {"points": [v(-27.86, 14.08) * mm, v(-27.86, 14.03) * mm, v(-27.86, 14.03) * mm, v(-27.9, 14.03) * mm]});
            skFitSpline(sketch, "E750", {"points": [v(-27.9, 14.03) * mm, v(-28.08, 14.03) * mm, v(-28.25, 14.03) * mm, v(-28.41, 14.03) * mm]});
            skFitSpline(sketch, "E751", {"points": [v(-28.41, 14.03) * mm, v(-28.46, 14.02) * mm, v(-28.48, 14.04) * mm, v(-28.5, 14.07) * mm]});
            skFitSpline(sketch, "E752", {"points": [v(-28.5, 14.07) * mm, v(-28.64, 14.28) * mm, v(-28.72, 14.5) * mm, v(-28.72, 14.75) * mm]});
            skFitSpline(sketch, "E753", {"points": [v(-28.72, 14.75) * mm, v(-28.72, 15.5) * mm, v(-28.72, 16.27) * mm, v(-28.72, 17.03) * mm]});
            skFitSpline(sketch, "E754", {"points": [v(-28.72, 17.03) * mm, v(-28.72, 17.05) * mm, v(-28.72, 17.07) * mm, v(-28.72, 17.08) * mm]});
            skFitSpline(sketch, "E755", {"points": [v(-28.72, 17.08) * mm, v(-28.72, 17.1) * mm, v(-28.73, 17.12) * mm, v(-28.75, 17.12) * mm]});
            skFitSpline(sketch, "E756", {"points": [v(-28.75, 17.12) * mm, v(-28.77, 17.12) * mm, v(-28.78, 17.12) * mm, v(-28.79, 17.12) * mm]});
            skFitSpline(sketch, "E757", {"points": [v(-28.79, 17.12) * mm, v(-29.11, 17.12) * mm, v(-29.44, 17.12) * mm, v(-29.77, 17.12) * mm]});
            skFitSpline(sketch, "E758", {"points": [v(-29.77, 17.12) * mm, v(-29.85, 17.12) * mm, v(-29.84, 17.12) * mm, v(-29.84, 17.05) * mm]});
            skFitSpline(sketch, "E759", {"points": [v(-29.84, 17.05) * mm, v(-29.84, 16.58) * mm, v(-29.84, 16.1) * mm, v(-29.84, 15.64) * mm]});
            skFitSpline(sketch, "E760", {"points": [v(-29.84, 15.64) * mm, v(-29.83, 15.29) * mm, v(-29.85, 14.93) * mm, v(-29.81, 14.57) * mm]});
            skFitSpline(sketch, "E761", {"points": [v(-29.81, 14.57) * mm, v(-29.8, 14.44) * mm, v(-29.8, 14.3) * mm, v(-29.76, 14.16) * mm]});
            skFitSpline(sketch, "E762", {"points": [v(-29.76, 14.16) * mm, v(-29.71, 13.95) * mm, v(-29.65, 13.74) * mm, v(-29.52, 13.55) * mm]});
            skFitSpline(sketch, "E763", {"points": [v(-29.52, 13.55) * mm, v(-29.44, 13.43) * mm, v(-29.36, 13.31) * mm, v(-29.27, 13.2) * mm]});
            skFitSpline(sketch, "E764", {"points": [v(-29.27, 13.2) * mm, v(-29.25, 13.17) * mm, v(-29.23, 13.15) * mm, v(-29.2, 13.15) * mm]});
            skFitSpline(sketch, "E765", {"points": [v(-29.2, 13.15) * mm, v(-28.9, 13.16) * mm, v(-28.6, 13.16) * mm, v(-28.32, 13.16) * mm]});
            skFitSpline(sketch, "E766", {"points": [v(-28.32, 13.16) * mm, v(-28.1, 13.17) * mm, v(-27.93, 13.23) * mm, v(-27.8, 13.39) * mm]});
            skFitSpline(sketch, "E767", {"points": [v(-27.8, 13.39) * mm, v(-27.79, 13.4) * mm, v(-27.79, 13.4) * mm, v(-27.78, 13.4) * mm]});
            skFitSpline(sketch, "E768", {"points": [v(-27.78, 13.4) * mm, v(-27.76, 13.42) * mm, v(-27.75, 13.44) * mm, v(-27.72, 13.45) * mm]});
            skFitSpline(sketch, "E769", {"points": [v(-24.19, 13.46) * mm, v(-24.15, 13.37) * mm, v(-24.11, 13.3) * mm, v(-24.08, 13.21) * mm]});
            skFitSpline(sketch, "E770", {"points": [v(-24.08, 13.21) * mm, v(-24.07, 13.17) * mm, v(-24.04, 13.15) * mm, v(-24, 13.15) * mm]});
            skFitSpline(sketch, "E771", {"points": [v(-24, 13.15) * mm, v(-23.76, 13.16) * mm, v(-23.52, 13.15) * mm, v(-23.28, 13.15) * mm]});
            skFitSpline(sketch, "E772", {"points": [v(-23.28, 13.15) * mm, v(-23.2, 13.16) * mm, v(-23.2, 13.14) * mm, v(-23.2, 13.23) * mm]});
            skFitSpline(sketch, "E773", {"points": [v(-23.2, 13.23) * mm, v(-23.2, 14.98) * mm, v(-23.2, 16.73) * mm, v(-23.2, 18.49) * mm]});
            skFitSpline(sketch, "E774", {"points": [v(-23.2, 18.49) * mm, v(-23.2, 18.5) * mm, v(-23.2, 18.52) * mm, v(-23.2, 18.53) * mm]});
            skFitSpline(sketch, "E775", {"points": [v(-23.2, 18.53) * mm, v(-23.2, 18.55) * mm, v(-23.21, 18.56) * mm, v(-23.23, 18.56) * mm]});
            skFitSpline(sketch, "E776", {"points": [v(-23.23, 18.56) * mm, v(-23.25, 18.56) * mm, v(-23.26, 18.56) * mm, v(-23.27, 18.56) * mm]});
            skFitSpline(sketch, "E777", {"points": [v(-23.27, 18.56) * mm, v(-23.52, 18.56) * mm, v(-23.76, 18.56) * mm, v(-24, 18.56) * mm]});
            skFitSpline(sketch, "E778", {"points": [v(-24, 18.56) * mm, v(-24.1, 18.56) * mm, v(-24.2, 18.56) * mm, v(-24.28, 18.55) * mm]});
            skFitSpline(sketch, "E779", {"points": [v(-24.28, 18.55) * mm, v(-24.33, 18.55) * mm, v(-24.33, 18.55) * mm, v(-24.33, 18.5) * mm]});
            skFitSpline(sketch, "E780", {"points": [v(-24.33, 18.5) * mm, v(-24.33, 18.5) * mm, v(-24.33, 18.47) * mm, v(-24.33, 18.46) * mm]});
            skFitSpline(sketch, "E781", {"points": [v(-24.33, 18.46) * mm, v(-24.33, 17.98) * mm, v(-24.33, 17.5) * mm, v(-24.33, 17.03) * mm]});
            skFitSpline(sketch, "E782", {"points": [v(-24.33, 17.03) * mm, v(-24.33, 17.02) * mm, v(-24.33, 17) * mm, v(-24.33, 16.98) * mm]});
            skFitSpline(sketch, "E783", {"points": [v(-24.33, 16.98) * mm, v(-24.33, 16.96) * mm, v(-24.34, 16.95) * mm, v(-24.36, 16.95) * mm]});
            skFitSpline(sketch, "E784", {"points": [v(-24.36, 16.95) * mm, v(-24.38, 16.95) * mm, v(-24.4, 16.95) * mm, v(-24.41, 16.98) * mm]});
            skFitSpline(sketch, "E785", {"points": [v(-24.41, 16.98) * mm, v(-24.42, 17) * mm, v(-24.45, 17.02) * mm, v(-24.47, 17.04) * mm]});
            skFitSpline(sketch, "E786", {"points": [v(-24.47, 17.04) * mm, v(-24.56, 17.1) * mm, v(-24.66, 17.12) * mm, v(-24.77, 17.12) * mm]});
            skFitSpline(sketch, "E787", {"points": [v(-24.77, 17.12) * mm, v(-25, 17.12) * mm, v(-25.23, 17.12) * mm, v(-25.46, 17.12) * mm]});
            skFitSpline(sketch, "E788", {"points": [v(-25.46, 17.12) * mm, v(-25.62, 17.12) * mm, v(-25.57, 17.14) * mm, v(-25.68, 17.03) * mm]});
            skFitSpline(sketch, "E789", {"points": [v(-25.68, 17.03) * mm, v(-25.7, 17.01) * mm, v(-25.72, 17) * mm, v(-25.73, 16.98) * mm]});
            skFitSpline(sketch, "E790", {"points": [v(-25.73, 16.98) * mm, v(-25.93, 16.76) * mm, v(-26.07, 16.51) * mm, v(-26.2, 16.25) * mm]});
            skFitSpline(sketch, "E791", {"points": [v(-26.2, 16.25) * mm, v(-26.23, 16.18) * mm, v(-26.25, 16.1) * mm, v(-26.27, 16.02) * mm]});
            skFitSpline(sketch, "E792", {"points": [v(-26.27, 16.02) * mm, v(-26.32, 15.83) * mm, v(-26.35, 15.64) * mm, v(-26.35, 15.45) * mm]});
            skFitSpline(sketch, "E793", {"points": [v(-26.35, 15.45) * mm, v(-26.36, 15.12) * mm, v(-26.37, 14.8) * mm, v(-26.31, 14.47) * mm]});
            skFitSpline(sketch, "E794", {"points": [v(-26.31, 14.47) * mm, v(-26.26, 14.2) * mm, v(-26.17, 13.92) * mm, v(-26.03, 13.68) * mm]});
            skFitSpline(sketch, "E795", {"points": [v(-26.03, 13.68) * mm, v(-25.92, 13.5) * mm, v(-25.8, 13.34) * mm, v(-25.64, 13.2) * mm]});
            skFitSpline(sketch, "E796", {"points": [v(-25.64, 13.2) * mm, v(-25.62, 13.17) * mm, v(-25.6, 13.16) * mm, v(-25.57, 13.16) * mm]});
            skFitSpline(sketch, "E797", {"points": [v(-25.57, 13.16) * mm, v(-25.25, 13.16) * mm, v(-24.93, 13.14) * mm, v(-24.62, 13.17) * mm]});
            skFitSpline(sketch, "E798", {"points": [v(-24.62, 13.17) * mm, v(-24.5, 13.18) * mm, v(-24.38, 13.21) * mm, v(-24.3, 13.3) * mm]});
            skFitSpline(sketch, "E799", {"points": [v(-24.3, 13.3) * mm, v(-24.25, 13.35) * mm, v(-24.22, 13.4) * mm, v(-24.19, 13.46) * mm]});
            skFitSpline(sketch, "E800", {"points": [v(-40.16, 13.15) * mm, v(-40.15, 13.14) * mm, v(-40.14, 13.14) * mm, v(-40.13, 13.14) * mm]});
            skFitSpline(sketch, "E801", {"points": [v(-40.13, 13.14) * mm, v(-39.77, 13.14) * mm, v(-39.42, 13.14) * mm, v(-39.06, 13.14) * mm]});
            skFitSpline(sketch, "E802", {"points": [v(-39.06, 13.14) * mm, v(-39.01, 13.14) * mm, v(-39.01, 13.16) * mm, v(-39, 13.19) * mm]});
            skFitSpline(sketch, "E803", {"points": [v(-39, 13.19) * mm, v(-38.98, 13.35) * mm, v(-38.95, 13.5) * mm, v(-38.93, 13.67) * mm]});
            skFitSpline(sketch, "E804", {"points": [v(-38.93, 13.67) * mm, v(-38.9, 13.77) * mm, v(-38.9, 13.87) * mm, v(-38.87, 13.98) * mm]});
            skFitSpline(sketch, "E805", {"points": [v(-38.87, 13.98) * mm, v(-38.76, 13.98) * mm, v(-38.65, 13.98) * mm, v(-38.54, 13.98) * mm]});
            skFitSpline(sketch, "E806", {"points": [v(-38.54, 13.98) * mm, v(-38.3, 13.98) * mm, v(-38.07, 13.98) * mm, v(-37.83, 13.98) * mm]});
            skFitSpline(sketch, "E807", {"points": [v(-37.83, 13.98) * mm, v(-37.78, 13.98) * mm, v(-37.78, 13.98) * mm, v(-37.77, 13.93) * mm]});
            skFitSpline(sketch, "E808", {"points": [v(-37.77, 13.93) * mm, v(-37.76, 13.85) * mm, v(-37.74, 13.78) * mm, v(-37.73, 13.7) * mm]});
            skFitSpline(sketch, "E809", {"points": [v(-37.73, 13.7) * mm, v(-37.7, 13.53) * mm, v(-37.67, 13.35) * mm, v(-37.64, 13.18) * mm]});
            skFitSpline(sketch, "E810", {"points": [v(-37.64, 13.18) * mm, v(-37.63, 13.15) * mm, v(-37.62, 13.14) * mm, v(-37.6, 13.14) * mm]});
            skFitSpline(sketch, "E811", {"points": [v(-37.6, 13.14) * mm, v(-37.59, 13.14) * mm, v(-37.58, 13.14) * mm, v(-37.57, 13.14) * mm]});
            skFitSpline(sketch, "E812", {"points": [v(-37.57, 13.14) * mm, v(-37.24, 13.14) * mm, v(-36.9, 13.14) * mm, v(-36.57, 13.14) * mm]});
            skFitSpline(sketch, "E813", {"points": [v(-36.57, 13.14) * mm, v(-36.55, 13.14) * mm, v(-36.53, 13.14) * mm, v(-36.51, 13.15) * mm]});
            skFitSpline(sketch, "E814", {"points": [v(-36.51, 13.15) * mm, v(-36.51, 13.15) * mm, v(-36.5, 13.15) * mm, v(-36.5, 13.15) * mm]});
            skFitSpline(sketch, "E815", {"points": [v(-36.5, 13.15) * mm, v(-36.56, 13.45) * mm, v(-36.61, 13.74) * mm, v(-36.67, 14.04) * mm]});
            skFitSpline(sketch, "E816", {"points": [v(-36.67, 14.04) * mm, v(-36.74, 14.41) * mm, v(-36.8, 14.79) * mm, v(-36.87, 15.16) * mm]});
            skFitSpline(sketch, "E817", {"points": [v(-36.87, 15.16) * mm, v(-36.93, 15.51) * mm, v(-37, 15.87) * mm, v(-37.06, 16.22) * mm]});
            skFitSpline(sketch, "E818", {"points": [v(-37.06, 16.22) * mm, v(-37.13, 16.6) * mm, v(-37.2, 16.96) * mm, v(-37.26, 17.33) * mm]});
            skFitSpline(sketch, "E819", {"points": [v(-37.26, 17.33) * mm, v(-37.33, 17.72) * mm, v(-37.4, 18.1) * mm, v(-37.47, 18.5) * mm]});
            skFitSpline(sketch, "E820", {"points": [v(-37.47, 18.5) * mm, v(-37.47, 18.53) * mm, v(-37.49, 18.54) * mm, v(-37.52, 18.54) * mm]});
            skFitSpline(sketch, "E821", {"points": [v(-37.52, 18.54) * mm, v(-37.63, 18.54) * mm, v(-37.74, 18.54) * mm, v(-37.85, 18.54) * mm]});
            skFitSpline(sketch, "E822", {"points": [v(-37.85, 18.54) * mm, v(-38.27, 18.54) * mm, v(-38.68, 18.54) * mm, v(-39.1, 18.55) * mm]});
            skFitSpline(sketch, "E823", {"points": [v(-39.1, 18.55) * mm, v(-39.14, 18.55) * mm, v(-39.14, 18.54) * mm, v(-39.15, 18.5) * mm]});
            skFitSpline(sketch, "E824", {"points": [v(-39.15, 18.5) * mm, v(-39.17, 18.4) * mm, v(-39.19, 18.3) * mm, v(-39.2, 18.2) * mm]});
            skFitSpline(sketch, "E825", {"points": [v(-39.2, 18.2) * mm, v(-39.28, 17.82) * mm, v(-39.35, 17.44) * mm, v(-39.42, 17.06) * mm]});
            skFitSpline(sketch, "E826", {"points": [v(-39.42, 17.06) * mm, v(-39.5, 16.68) * mm, v(-39.56, 16.3) * mm, v(-39.64, 15.92) * mm]});
            skFitSpline(sketch, "E827", {"points": [v(-39.64, 15.92) * mm, v(-39.7, 15.54) * mm, v(-39.78, 15.16) * mm, v(-39.85, 14.77) * mm]});
            skFitSpline(sketch, "E828", {"points": [v(-39.85, 14.77) * mm, v(-39.92, 14.4) * mm, v(-40, 14.02) * mm, v(-40.07, 13.64) * mm]});
            skFitSpline(sketch, "E829", {"points": [v(-40.07, 13.64) * mm, v(-40.1, 13.48) * mm, v(-40.13, 13.31) * mm, v(-40.16, 13.15) * mm]});
            skFitSpline(sketch, "E830", {"points": [v(-33.54, 15.97) * mm, v(-33.46, 16.04) * mm, v(-33.39, 16.1) * mm, v(-33.32, 16.16) * mm]});
            skFitSpline(sketch, "E831", {"points": [v(-33.32, 16.16) * mm, v(-33.24, 16.23) * mm, v(-33.17, 16.31) * mm, v(-33.12, 16.4) * mm]});
            skFitSpline(sketch, "E832", {"points": [v(-33.12, 16.4) * mm, v(-33.05, 16.57) * mm, v(-33.01, 16.74) * mm, v(-33, 16.9) * mm]});
            skFitSpline(sketch, "E833", {"points": [v(-33, 16.9) * mm, v(-32.97, 17.06) * mm, v(-32.98, 17.2) * mm, v(-33, 17.36) * mm]});
            skFitSpline(sketch, "E834", {"points": [v(-33, 17.36) * mm, v(-33.01, 17.62) * mm, v(-33.1, 17.85) * mm, v(-33.27, 18.05) * mm]});
            skFitSpline(sketch, "E835", {"points": [v(-33.27, 18.05) * mm, v(-33.4, 18.2) * mm, v(-33.55, 18.32) * mm, v(-33.72, 18.42) * mm]});
            skFitSpline(sketch, "E836", {"points": [v(-33.72, 18.42) * mm, v(-33.85, 18.5) * mm, v(-33.98, 18.56) * mm, v(-34.14, 18.54) * mm]});
            skFitSpline(sketch, "E837", {"points": [v(-34.14, 18.54) * mm, v(-34.16, 18.53) * mm, v(-34.18, 18.53) * mm, v(-34.2, 18.53) * mm]});
            skFitSpline(sketch, "E838", {"points": [v(-34.2, 18.53) * mm, v(-34.85, 18.54) * mm, v(-35.5, 18.53) * mm, v(-36.16, 18.54) * mm]});
            skFitSpline(sketch, "E839", {"points": [v(-36.16, 18.54) * mm, v(-36.24, 18.54) * mm, v(-36.23, 18.54) * mm, v(-36.23, 18.47) * mm]});
            skFitSpline(sketch, "E840", {"points": [v(-36.23, 18.47) * mm, v(-36.23, 17.01) * mm, v(-36.23, 15.55) * mm, v(-36.23, 14.1) * mm]});
            skFitSpline(sketch, "E841", {"points": [v(-36.23, 14.1) * mm, v(-36.23, 13.8) * mm, v(-36.23, 13.5) * mm, v(-36.22, 13.2) * mm]});
            skFitSpline(sketch, "E842", {"points": [v(-36.22, 13.2) * mm, v(-36.22, 13.18) * mm, v(-36.23, 13.16) * mm, v(-36.22, 13.14) * mm]});
            skFitSpline(sketch, "E843", {"points": [v(-36.22, 13.14) * mm, v(-36.2, 13.14) * mm, v(-36.2, 13.14) * mm, v(-36.2, 13.14) * mm]});
            skFitSpline(sketch, "E844", {"points": [v(-36.2, 13.14) * mm, v(-35.43, 13.14) * mm, v(-34.67, 13.14) * mm, v(-33.9, 13.14) * mm]});
            skFitSpline(sketch, "E845", {"points": [v(-33.9, 13.14) * mm, v(-33.87, 13.14) * mm, v(-33.85, 13.15) * mm, v(-33.82, 13.16) * mm]});
            skFitSpline(sketch, "E846", {"points": [v(-33.82, 13.16) * mm, v(-33.69, 13.22) * mm, v(-33.57, 13.31) * mm, v(-33.46, 13.41) * mm]});
            skFitSpline(sketch, "E847", {"points": [v(-33.46, 13.41) * mm, v(-33.23, 13.63) * mm, v(-33.05, 13.87) * mm, v(-32.94, 14.17) * mm]});
            skFitSpline(sketch, "E848", {"points": [v(-32.94, 14.17) * mm, v(-32.82, 14.5) * mm, v(-32.79, 14.84) * mm, v(-32.89, 15.19) * mm]});
            skFitSpline(sketch, "E849", {"points": [v(-32.89, 15.19) * mm, v(-32.96, 15.44) * mm, v(-33.08, 15.67) * mm, v(-33.3, 15.83) * mm]});
            skFitSpline(sketch, "E850", {"points": [v(-33.3, 15.83) * mm, v(-33.37, 15.88) * mm, v(-33.45, 15.93) * mm, v(-33.54, 15.97) * mm]});
            skLineSegment(sketch, "E851", {"start": v(-26.82, 17.12) * mm, "end": v(-27.78, 17.12) * mm});
            skFitSpline(sketch, "E852", {"points": [v(-44.74, 9.6) * mm, v(-44.74, 9.63) * mm, v(-44.74, 9.65) * mm, v(-44.74, 9.68) * mm]});
            skFitSpline(sketch, "E853", {"points": [v(-44.74, 9.68) * mm, v(-44.74, 10.24) * mm, v(-44.74, 10.8) * mm, v(-44.74, 11.37) * mm]});
            skFitSpline(sketch, "E854", {"points": [v(-35.07, 14.76) * mm, v(-35.07, 14.95) * mm, v(-35.07, 15.15) * mm, v(-35.07, 15.34) * mm]});
            skFitSpline(sketch, "E855", {"points": [v(-35.07, 15.34) * mm, v(-35.07, 15.4) * mm, v(-35.06, 15.4) * mm, v(-35.01, 15.4) * mm]});
            skFitSpline(sketch, "E856", {"points": [v(-35.01, 15.4) * mm, v(-34.8, 15.4) * mm, v(-34.6, 15.4) * mm, v(-34.38, 15.4) * mm]});
            skFitSpline(sketch, "E857", {"points": [v(-34.38, 15.4) * mm, v(-34.35, 15.4) * mm, v(-34.33, 15.38) * mm, v(-34.3, 15.36) * mm]});
            skFitSpline(sketch, "E858", {"points": [v(-34.3, 15.36) * mm, v(-34.3, 15.34) * mm, v(-34.27, 15.32) * mm, v(-34.25, 15.3) * mm]});
            skFitSpline(sketch, "E859", {"points": [v(-34.25, 15.3) * mm, v(-34.14, 15.18) * mm, v(-34.09, 15.04) * mm, v(-34.08, 14.88) * mm]});
            skFitSpline(sketch, "E860", {"points": [v(-34.08, 14.88) * mm, v(-34.06, 14.6) * mm, v(-34.14, 14.35) * mm, v(-34.35, 14.15) * mm]});
            skFitSpline(sketch, "E861", {"points": [v(-34.35, 14.15) * mm, v(-34.37, 14.13) * mm, v(-34.4, 14.12) * mm, v(-34.42, 14.12) * mm]});
            skFitSpline(sketch, "E862", {"points": [v(-34.42, 14.12) * mm, v(-34.62, 14.12) * mm, v(-34.81, 14.12) * mm, v(-35, 14.12) * mm]});
            skFitSpline(sketch, "E863", {"points": [v(-35, 14.12) * mm, v(-35.07, 14.12) * mm, v(-35.07, 14.11) * mm, v(-35.07, 14.17) * mm]});
            skFitSpline(sketch, "E864", {"points": [v(-35.07, 14.17) * mm, v(-35.07, 14.37) * mm, v(-35.07, 14.56) * mm, v(-35.07, 14.76) * mm]});
            skFitSpline(sketch, "E865", {"points": [v(-35.06, 16.38) * mm, v(-35.06, 16.75) * mm, v(-35.06, 17.12) * mm, v(-35.06, 17.5) * mm]});
            skFitSpline(sketch, "E866", {"points": [v(-35.06, 17.5) * mm, v(-35.06, 17.53) * mm, v(-35.05, 17.54) * mm, v(-35.02, 17.54) * mm]});
            skFitSpline(sketch, "E867", {"points": [v(-35.02, 17.54) * mm, v(-34.81, 17.53) * mm, v(-34.6, 17.53) * mm, v(-34.4, 17.53) * mm]});
            skFitSpline(sketch, "E868", {"points": [v(-34.4, 17.53) * mm, v(-34.37, 17.53) * mm, v(-34.35, 17.52) * mm, v(-34.33, 17.5) * mm]});
            skFitSpline(sketch, "E869", {"points": [v(-34.33, 17.5) * mm, v(-34.22, 17.36) * mm, v(-34.16, 17.2) * mm, v(-34.13, 17.03) * mm]});
            skFitSpline(sketch, "E870", {"points": [v(-34.13, 17.03) * mm, v(-34.1, 16.88) * mm, v(-34.13, 16.73) * mm, v(-34.2, 16.6) * mm]});
            skFitSpline(sketch, "E871", {"points": [v(-34.2, 16.6) * mm, v(-34.24, 16.52) * mm, v(-34.3, 16.45) * mm, v(-34.34, 16.39) * mm]});
            skFitSpline(sketch, "E872", {"points": [v(-34.34, 16.39) * mm, v(-34.36, 16.36) * mm, v(-34.38, 16.37) * mm, v(-34.4, 16.37) * mm]});
            skFitSpline(sketch, "E873", {"points": [v(-34.4, 16.37) * mm, v(-34.61, 16.37) * mm, v(-34.82, 16.37) * mm, v(-35.02, 16.37) * mm]});
            skFitSpline(sketch, "E874", {"points": [v(-35.02, 16.37) * mm, v(-35.04, 16.37) * mm, v(-35.05, 16.37) * mm, v(-35.06, 16.38) * mm]});
            skLineSegment(sketch, "E875", {"start": v(-44.75, 19.6) * mm, "end": v(-21.65, 19.6) * mm});
            skLineSegment(sketch, "E876", {"start": v(-21.65, 19.6) * mm, "end": v(-21.65, 9.6) * mm});
            skLineSegment(sketch, "E877", {"start": v(-21.65, 9.6) * mm, "end": v(-44.74, 9.6) * mm});
            skFitSpline(sketch, "E878", {"points": [v(-38.05, 14.9) * mm, v(-38.25, 14.9) * mm, v(-38.46, 14.9) * mm, v(-38.67, 14.9) * mm]});
            skFitSpline(sketch, "E879", {"points": [v(-38.67, 14.9) * mm, v(-38.73, 14.9) * mm, v(-38.73, 14.9) * mm, v(-38.72, 14.95) * mm]});
            skFitSpline(sketch, "E880", {"points": [v(-38.72, 14.95) * mm, v(-38.68, 15.16) * mm, v(-38.64, 15.37) * mm, v(-38.6, 15.57) * mm]});
            skFitSpline(sketch, "E881", {"points": [v(-38.6, 15.57) * mm, v(-38.55, 15.89) * mm, v(-38.5, 16.2) * mm, v(-38.45, 16.52) * mm]});
            skFitSpline(sketch, "E882", {"points": [v(-38.45, 16.52) * mm, v(-38.42, 16.67) * mm, v(-38.4, 16.83) * mm, v(-38.36, 16.99) * mm]});
            skFitSpline(sketch, "E883", {"points": [v(-38.36, 16.99) * mm, v(-38.36, 17) * mm, v(-38.36, 17) * mm, v(-38.36, 17.01) * mm]});
            skFitSpline(sketch, "E884", {"points": [v(-38.36, 17.01) * mm, v(-38.35, 17.03) * mm, v(-38.36, 17.06) * mm, v(-38.34, 17.06) * mm]});
            skFitSpline(sketch, "E885", {"points": [v(-38.34, 17.06) * mm, v(-38.31, 17.06) * mm, v(-38.32, 17.03) * mm, v(-38.32, 17.02) * mm]});
            skFitSpline(sketch, "E886", {"points": [v(-38.32, 17.02) * mm, v(-38.3, 16.98) * mm, v(-38.3, 16.94) * mm, v(-38.3, 16.9) * mm]});
            skFitSpline(sketch, "E887", {"points": [v(-38.3, 16.9) * mm, v(-38.21, 16.43) * mm, v(-38.13, 15.97) * mm, v(-38.05, 15.5) * mm]});
            skFitSpline(sketch, "E888", {"points": [v(-38.05, 15.5) * mm, v(-38.01, 15.3) * mm, v(-37.98, 15.1) * mm, v(-37.94, 14.9) * mm]});
            skFitSpline(sketch, "E889", {"points": [v(-24.32, 15.13) * mm, v(-24.32, 14.96) * mm, v(-24.32, 14.78) * mm, v(-24.32, 14.6) * mm]});
            skFitSpline(sketch, "E890", {"points": [v(-24.32, 14.6) * mm, v(-24.32, 14.43) * mm, v(-24.32, 14.25) * mm, v(-24.32, 14.08) * mm]});
            skFitSpline(sketch, "E891", {"points": [v(-24.32, 14.08) * mm, v(-24.33, 14.03) * mm, v(-24.33, 14.03) * mm, v(-24.38, 14.03) * mm]});
            skFitSpline(sketch, "E892", {"points": [v(-24.38, 14.03) * mm, v(-24.56, 14.03) * mm, v(-24.74, 14.03) * mm, v(-24.92, 14.03) * mm]});
            skFitSpline(sketch, "E893", {"points": [v(-24.92, 14.03) * mm, v(-24.95, 14.03) * mm, v(-24.97, 14.03) * mm, v(-24.98, 14.06) * mm]});
            skFitSpline(sketch, "E894", {"points": [v(-24.98, 14.06) * mm, v(-25.07, 14.25) * mm, v(-25.15, 14.44) * mm, v(-25.19, 14.66) * mm]});
            skFitSpline(sketch, "E895", {"points": [v(-25.19, 14.66) * mm, v(-25.22, 14.85) * mm, v(-25.22, 15.05) * mm, v(-25.22, 15.25) * mm]});
            skFitSpline(sketch, "E896", {"points": [v(-25.22, 15.25) * mm, v(-25.2, 15.59) * mm, v(-25.13, 15.9) * mm, v(-24.99, 16.21) * mm]});
            skFitSpline(sketch, "E897", {"points": [v(-24.99, 16.21) * mm, v(-24.97, 16.24) * mm, v(-24.96, 16.25) * mm, v(-24.93, 16.25) * mm]});
            skFitSpline(sketch, "E898", {"points": [v(-24.93, 16.25) * mm, v(-24.74, 16.25) * mm, v(-24.55, 16.25) * mm, v(-24.36, 16.25) * mm]});
            skFitSpline(sketch, "E899", {"points": [v(-24.36, 16.25) * mm, v(-24.32, 16.24) * mm, v(-24.32, 16.24) * mm, v(-24.32, 16.2) * mm]});
            skFitSpline(sketch, "E900", {"points": [v(-24.32, 16.2) * mm, v(-24.32, 15.95) * mm, v(-24.32, 15.7) * mm, v(-24.32, 15.46) * mm]});
            skFitSpline(sketch, "E901", {"points": [v(-24.32, 15.46) * mm, v(-24.32, 15.35) * mm, v(-24.32, 15.24) * mm, v(-24.32, 15.14) * mm]});
            skLineSegment(sketch, "E902", {"start": v(-37.94, 14.9) * mm, "end": v(-38.05, 14.9) * mm});
            skFitSpline(sketch, "E903", {"points": [v(-33.88, 11.19) * mm, v(-33.87, 11.22) * mm, v(-33.9, 11.26) * mm, v(-33.87, 11.29) * mm]});
            skFitSpline(sketch, "E904", {"points": [v(-33.87, 11.29) * mm, v(-33.84, 11.31) * mm, v(-33.8, 11.3) * mm, v(-33.76, 11.3) * mm]});
            skFitSpline(sketch, "E905", {"points": [v(-33.76, 11.3) * mm, v(-33.74, 11.3) * mm, v(-33.72, 11.3) * mm, v(-33.7, 11.3) * mm]});
            skFitSpline(sketch, "E906", {"points": [v(-33.7, 11.3) * mm, v(-33.61, 11.28) * mm, v(-33.57, 11.2) * mm, v(-33.61, 11.12) * mm]});
            skFitSpline(sketch, "E907", {"points": [v(-33.61, 11.12) * mm, v(-33.63, 11.1) * mm, v(-33.66, 11.08) * mm, v(-33.7, 11.07) * mm]});
            skFitSpline(sketch, "E908", {"points": [v(-33.7, 11.07) * mm, v(-33.74, 11.06) * mm, v(-33.8, 11.07) * mm, v(-33.85, 11.06) * mm]});
            skFitSpline(sketch, "E909", {"points": [v(-33.85, 11.06) * mm, v(-33.87, 11.06) * mm, v(-33.88, 11.07) * mm, v(-33.88, 11.1) * mm]});
            skFitSpline(sketch, "E910", {"points": [v(-33.88, 11.1) * mm, v(-33.87, 11.12) * mm, v(-33.88, 11.15) * mm, v(-33.88, 11.19) * mm]});
            skFitSpline(sketch, "E911", {"points": [v(-33.79, 11.64) * mm, v(-33.76, 11.64) * mm, v(-33.74, 11.64) * mm, v(-33.72, 11.64) * mm]});
            skFitSpline(sketch, "E912", {"points": [v(-33.72, 11.64) * mm, v(-33.67, 11.63) * mm, v(-33.64, 11.6) * mm, v(-33.64, 11.55) * mm]});
            skFitSpline(sketch, "E913", {"points": [v(-33.64, 11.55) * mm, v(-33.63, 11.5) * mm, v(-33.66, 11.47) * mm, v(-33.71, 11.46) * mm]});
            skFitSpline(sketch, "E914", {"points": [v(-33.71, 11.46) * mm, v(-33.76, 11.45) * mm, v(-33.8, 11.45) * mm, v(-33.85, 11.45) * mm]});
            skFitSpline(sketch, "E915", {"points": [v(-33.85, 11.45) * mm, v(-33.87, 11.45) * mm, v(-33.88, 11.46) * mm, v(-33.88, 11.48) * mm]});
            skFitSpline(sketch, "E916", {"points": [v(-33.88, 11.48) * mm, v(-33.88, 11.52) * mm, v(-33.88, 11.57) * mm, v(-33.88, 11.62) * mm]});
            skFitSpline(sketch, "E917", {"points": [v(-33.88, 11.62) * mm, v(-33.88, 11.64) * mm, v(-33.87, 11.64) * mm, v(-33.85, 11.64) * mm]});
            skFitSpline(sketch, "E918", {"points": [v(-33.85, 11.64) * mm, v(-33.83, 11.64) * mm, v(-33.8, 11.64) * mm, v(-33.79, 11.64) * mm]});
            skLineSegment(sketch, "E919", {"start": v(-24.32, 15.14) * mm, "end": v(-24.32, 15.14) * mm});
            skLineSegment(sketch, "E920", {"start": v(-24.32, 15.14) * mm, "end": v(-24.32, 15.13) * mm});
            skLineSegment(sketch, "E921", {"start": v(-24.32, 15.13) * mm, "end": v(-24.32, 15.14) * mm});
            skFitSpline(sketch, "E922", {"points": [v(-36.51, 11.3) * mm, v(-36.48, 11.3) * mm, v(-36.45, 11.3) * mm, v(-36.42, 11.3) * mm]});
            skFitSpline(sketch, "E923", {"points": [v(-36.42, 11.3) * mm, v(-36.36, 11.28) * mm, v(-36.33, 11.25) * mm, v(-36.33, 11.19) * mm]});
            skFitSpline(sketch, "E924", {"points": [v(-36.33, 11.19) * mm, v(-36.33, 11.13) * mm, v(-36.36, 11.08) * mm, v(-36.41, 11.07) * mm]});
            skFitSpline(sketch, "E925", {"points": [v(-36.41, 11.07) * mm, v(-36.47, 11.06) * mm, v(-36.53, 11.06) * mm, v(-36.58, 11.06) * mm]});
            skFitSpline(sketch, "E926", {"points": [v(-36.58, 11.06) * mm, v(-36.6, 11.06) * mm, v(-36.6, 11.08) * mm, v(-36.6, 11.1) * mm]});
            skFitSpline(sketch, "E927", {"points": [v(-36.6, 11.1) * mm, v(-36.6, 11.15) * mm, v(-36.6, 11.2) * mm, v(-36.6, 11.26) * mm]});
            skFitSpline(sketch, "E928", {"points": [v(-36.6, 11.26) * mm, v(-36.6, 11.29) * mm, v(-36.6, 11.3) * mm, v(-36.58, 11.3) * mm]});
            skFitSpline(sketch, "E929", {"points": [v(-36.58, 11.3) * mm, v(-36.55, 11.3) * mm, v(-36.53, 11.3) * mm, v(-36.51, 11.3) * mm]});
            skFitSpline(sketch, "E930", {"points": [v(-36.51, 11.3) * mm, v(-36.51, 11.3) * mm, v(-36.51, 11.3) * mm, v(-36.51, 11.3) * mm]});
            skFitSpline(sketch, "E931", {"points": [v(-36.6, 11.55) * mm, v(-36.6, 11.64) * mm, v(-36.6, 11.64) * mm, v(-36.51, 11.64) * mm]});
            skFitSpline(sketch, "E932", {"points": [v(-36.51, 11.64) * mm, v(-36.49, 11.64) * mm, v(-36.46, 11.65) * mm, v(-36.44, 11.64) * mm]});
            skFitSpline(sketch, "E933", {"points": [v(-36.44, 11.64) * mm, v(-36.4, 11.63) * mm, v(-36.37, 11.6) * mm, v(-36.37, 11.55) * mm]});
            skFitSpline(sketch, "E934", {"points": [v(-36.37, 11.55) * mm, v(-36.37, 11.5) * mm, v(-36.39, 11.47) * mm, v(-36.44, 11.46) * mm]});
            skFitSpline(sketch, "E935", {"points": [v(-36.44, 11.46) * mm, v(-36.49, 11.45) * mm, v(-36.54, 11.45) * mm, v(-36.58, 11.45) * mm]});
            skFitSpline(sketch, "E936", {"points": [v(-36.58, 11.45) * mm, v(-36.6, 11.45) * mm, v(-36.6, 11.46) * mm, v(-36.6, 11.48) * mm]});
            skFitSpline(sketch, "E937", {"points": [v(-36.6, 11.48) * mm, v(-36.6, 11.5) * mm, v(-36.6, 11.52) * mm, v(-36.6, 11.55) * mm]});
            skFitSpline(sketch, "E938", {"points": [v(-42.73, 11.35) * mm, v(-42.73, 11.43) * mm, v(-42.73, 11.5) * mm, v(-42.73, 11.59) * mm]});
            skFitSpline(sketch, "E939", {"points": [v(-42.73, 11.59) * mm, v(-42.73, 11.62) * mm, v(-42.72, 11.63) * mm, v(-42.69, 11.63) * mm]});
            skFitSpline(sketch, "E940", {"points": [v(-42.69, 11.63) * mm, v(-42.63, 11.63) * mm, v(-42.57, 11.62) * mm, v(-42.52, 11.6) * mm]});
            skFitSpline(sketch, "E941", {"points": [v(-42.52, 11.6) * mm, v(-42.43, 11.58) * mm, v(-42.38, 11.52) * mm, v(-42.36, 11.43) * mm]});
            skFitSpline(sketch, "E942", {"points": [v(-42.36, 11.43) * mm, v(-42.36, 11.38) * mm, v(-42.35, 11.34) * mm, v(-42.36, 11.3) * mm]});
            skFitSpline(sketch, "E943", {"points": [v(-42.36, 11.3) * mm, v(-42.38, 11.18) * mm, v(-42.46, 11.1) * mm, v(-42.6, 11.09) * mm]});
            skFitSpline(sketch, "E944", {"points": [v(-42.6, 11.09) * mm, v(-42.63, 11.08) * mm, v(-42.66, 11.09) * mm, v(-42.7, 11.08) * mm]});
            skFitSpline(sketch, "E945", {"points": [v(-42.7, 11.08) * mm, v(-42.72, 11.08) * mm, v(-42.73, 11.1) * mm, v(-42.73, 11.12) * mm]});
            skFitSpline(sketch, "E946", {"points": [v(-42.73, 11.12) * mm, v(-42.73, 11.2) * mm, v(-42.73, 11.28) * mm, v(-42.73, 11.35) * mm]});
            skFitSpline(sketch, "E947", {"points": [v(-39.6, 11.1) * mm, v(-39.65, 11.04) * mm, v(-39.77, 11.03) * mm, v(-39.83, 11.07) * mm]});
            skFitSpline(sketch, "E948", {"points": [v(-39.83, 11.07) * mm, v(-39.92, 11.13) * mm, v(-39.93, 11.26) * mm, v(-39.85, 11.33) * mm]});
            skFitSpline(sketch, "E949", {"points": [v(-39.85, 11.33) * mm, v(-39.84, 11.34) * mm, v(-39.83, 11.35) * mm, v(-39.81, 11.34) * mm]});
            skFitSpline(sketch, "E950", {"points": [v(-39.81, 11.34) * mm, v(-39.74, 11.26) * mm, v(-39.67, 11.18) * mm, v(-39.6, 11.1) * mm]});
            skLineSegment(sketch, "E951", {"start": v(-33.79, 11.64) * mm, "end": v(-33.79, 11.64) * mm});
            skFitSpline(sketch, "E952", {"points": [v(-37.57, 11.24) * mm, v(-37.53, 11.35) * mm, v(-37.5, 11.46) * mm, v(-37.45, 11.58) * mm]});
            skFitSpline(sketch, "E953", {"points": [v(-37.45, 11.58) * mm, v(-37.4, 11.47) * mm, v(-37.37, 11.36) * mm, v(-37.32, 11.24) * mm]});
            skLineSegment(sketch, "E954", {"start": v(-37.32, 11.24) * mm, "end": v(-37.57, 11.24) * mm});
            skFitSpline(sketch, "E955", {"points": [v(-34.83, 11.24) * mm, v(-34.82, 11.3) * mm, v(-34.8, 11.35) * mm, v(-34.78, 11.41) * mm]});
            skFitSpline(sketch, "E956", {"points": [v(-34.78, 11.41) * mm, v(-34.76, 11.47) * mm, v(-34.74, 11.52) * mm, v(-34.71, 11.59) * mm]});
            skFitSpline(sketch, "E957", {"points": [v(-34.71, 11.59) * mm, v(-34.67, 11.47) * mm, v(-34.63, 11.36) * mm, v(-34.6, 11.24) * mm]});
            skFitSpline(sketch, "E958", {"points": [v(-27.29, 11.24) * mm, v(-27.28, 11.2) * mm, v(-27.29, 11.16) * mm, v(-27.3, 11.13) * mm]});
            skFitSpline(sketch, "E959", {"points": [v(-27.3, 11.13) * mm, v(-27.33, 11.07) * mm, v(-27.37, 11.05) * mm, v(-27.43, 11.05) * mm]});
            skFitSpline(sketch, "E960", {"points": [v(-27.43, 11.05) * mm, v(-27.48, 11.05) * mm, v(-27.53, 11.07) * mm, v(-27.55, 11.13) * mm]});
            skFitSpline(sketch, "E961", {"points": [v(-27.55, 11.13) * mm, v(-27.58, 11.2) * mm, v(-27.58, 11.28) * mm, v(-27.55, 11.35) * mm]});
            skFitSpline(sketch, "E962", {"points": [v(-27.55, 11.35) * mm, v(-27.53, 11.41) * mm, v(-27.48, 11.44) * mm, v(-27.42, 11.44) * mm]});
            skFitSpline(sketch, "E963", {"points": [v(-27.42, 11.44) * mm, v(-27.36, 11.44) * mm, v(-27.32, 11.4) * mm, v(-27.3, 11.35) * mm]});
            skFitSpline(sketch, "E964", {"points": [v(-27.3, 11.35) * mm, v(-27.29, 11.31) * mm, v(-27.29, 11.28) * mm, v(-27.29, 11.24) * mm]});
            skFitSpline(sketch, "E965", {"points": [v(-24.51, 11.32) * mm, v(-24.49, 11.42) * mm, v(-24.44, 11.46) * mm, v(-24.35, 11.45) * mm]});
            skFitSpline(sketch, "E966", {"points": [v(-24.35, 11.45) * mm, v(-24.29, 11.44) * mm, v(-24.25, 11.4) * mm, v(-24.24, 11.32) * mm]});
            skLineSegment(sketch, "E967", {"start": v(-34.6, 11.24) * mm, "end": v(-34.83, 11.24) * mm});
            skFitSpline(sketch, "E968", {"points": [v(-32.44, 11.03) * mm, v(-32.47, 11.03) * mm, v(-32.5, 11.04) * mm, v(-32.52, 11.06) * mm]});
            skFitSpline(sketch, "E969", {"points": [v(-32.52, 11.06) * mm, v(-32.56, 11.1) * mm, v(-32.54, 11.17) * mm, v(-32.49, 11.2) * mm]});
            skFitSpline(sketch, "E970", {"points": [v(-32.49, 11.2) * mm, v(-32.43, 11.22) * mm, v(-32.37, 11.21) * mm, v(-32.31, 11.21) * mm]});
            skFitSpline(sketch, "E971", {"points": [v(-32.31, 11.21) * mm, v(-32.3, 11.2) * mm, v(-32.3, 11.2) * mm, v(-32.3, 11.18) * mm]});
            skFitSpline(sketch, "E972", {"points": [v(-32.3, 11.18) * mm, v(-32.3, 11.1) * mm, v(-32.36, 11.03) * mm, v(-32.44, 11.03) * mm]});
            skFitSpline(sketch, "E973", {"points": [v(-26.7, 11.32) * mm, v(-26.7, 11.4) * mm, v(-26.65, 11.45) * mm, v(-26.57, 11.45) * mm]});
            skFitSpline(sketch, "E974", {"points": [v(-26.57, 11.45) * mm, v(-26.49, 11.45) * mm, v(-26.45, 11.41) * mm, v(-26.44, 11.33) * mm]});
            skFitSpline(sketch, "E975", {"points": [v(-26.44, 11.33) * mm, v(-26.48, 11.31) * mm, v(-26.64, 11.31) * mm, v(-26.7, 11.32) * mm]});
            skFitSpline(sketch, "E976", {"points": [v(-29.7, 11.24) * mm, v(-29.7, 11.2) * mm, v(-29.7, 11.17) * mm, v(-29.71, 11.13) * mm]});
            skFitSpline(sketch, "E977", {"points": [v(-29.71, 11.13) * mm, v(-29.73, 11.08) * mm, v(-29.78, 11.05) * mm, v(-29.83, 11.04) * mm]});
            skFitSpline(sketch, "E978", {"points": [v(-29.83, 11.04) * mm, v(-29.9, 11.04) * mm, v(-29.94, 11.07) * mm, v(-29.97, 11.13) * mm]});
            skFitSpline(sketch, "E979", {"points": [v(-29.97, 11.13) * mm, v(-30, 11.2) * mm, v(-30, 11.28) * mm, v(-29.97, 11.35) * mm]});
            skFitSpline(sketch, "E980", {"points": [v(-29.97, 11.35) * mm, v(-29.95, 11.41) * mm, v(-29.9, 11.44) * mm, v(-29.84, 11.44) * mm]});
            skFitSpline(sketch, "E981", {"points": [v(-29.84, 11.44) * mm, v(-29.78, 11.44) * mm, v(-29.73, 11.4) * mm, v(-29.71, 11.35) * mm]});
            skFitSpline(sketch, "E982", {"points": [v(-29.71, 11.35) * mm, v(-29.7, 11.32) * mm, v(-29.7, 11.28) * mm, v(-29.7, 11.24) * mm]});
            skLineSegment(sketch, "E983", {"start": v(-24.24, 11.32) * mm, "end": v(-24.51, 11.32) * mm});
            skLineSegment(sketch, "E984", {"start": v(-24.51, 11.32) * mm, "end": v(-24.24, 11.32) * mm});
            skLineSegment(sketch, "E985", {"start": v(-44.74, 11.37) * mm, "end": v(-44.75, 19.6) * mm});
            skSolve(sketch);
        }
        {
            var Q0;
            Q0=makeQuery(id+"F10.imprint","IMPRINT",FACE,{"disambiguationData":[TD([[makeQuery(id+"F10.imprint","IMPRINT",EDGE,{"derivedFrom":sQuery(id+"F10.wireOp",EDGE,"E878")}),-1.0]])]});
            var Q1;
            Q1=makeQuery(id+"F10.imprint","IMPRINT",FACE,{"disambiguationData":[TD([[makeQuery(id+"F10.imprint","IMPRINT",EDGE,{"derivedFrom":sQuery(id+"F10.wireOp",EDGE,"E854")}),-1.0]])]});
            var Q2;
            Q2=makeQuery(id+"F10.imprint","IMPRINT",FACE,{"disambiguationData":[TD([[makeQuery(id+"F10.imprint","IMPRINT",EDGE,{"derivedFrom":sQuery(id+"F10.wireOp",EDGE,"E865")}),-1.0]])]});
            var Q3;
            Q3=makeQuery(id+"F10.imprint","IMPRINT",FACE,{"disambiguationData":[TD([[makeQuery(id+"F10.imprint","IMPRINT",EDGE,{"derivedFrom":sQuery(id+"F10.wireOp",EDGE,"E889")}),-1.0]])]});
            var Q4;
            Q4=makeQuery(id+"F10.imprint","IMPRINT",FACE,{"disambiguationData":[TD([[makeQuery(id+"F10.imprint","IMPRINT",EDGE,{"derivedFrom":sQuery(id+"F10.wireOp",EDGE,"E938")}),-1.0]])]});
            var Q5;
            Q5=makeQuery(id+"F10.imprint","IMPRINT",FACE,{"disambiguationData":[TD([[makeQuery(id+"F10.imprint","IMPRINT",EDGE,{"derivedFrom":sQuery(id+"F10.wireOp",EDGE,"E947")}),-1.0]])]});
            var Q6;
            Q6=makeQuery(id+"F10.imprint","IMPRINT",FACE,{"disambiguationData":[TD([[makeQuery(id+"F10.imprint","IMPRINT",EDGE,{"derivedFrom":sQuery(id+"F10.wireOp",EDGE,"E952")}),-1.0]])]});
            var Q7;
            Q7=makeQuery(id+"F10.imprint","IMPRINT",FACE,{"disambiguationData":[TD([[makeQuery(id+"F10.imprint","IMPRINT",EDGE,{"derivedFrom":sQuery(id+"F10.wireOp",EDGE,"E955")}),-1.0]])]});
            var Q8;
            Q8=makeQuery(id+"F10.imprint","IMPRINT",FACE,{"disambiguationData":[TD([[makeQuery(id+"F10.imprint","IMPRINT",EDGE,{"derivedFrom":sQuery(id+"F10.wireOp",EDGE,"E903")}),-1.0]])]});
            var Q9;
            Q9=makeQuery(id+"F10.imprint","IMPRINT",FACE,{"disambiguationData":[TD([[makeQuery(id+"F10.imprint","IMPRINT",EDGE,{"derivedFrom":sQuery(id+"F10.wireOp",EDGE,"E911")}),-1.0]])]});
            var Q10;
            Q10=makeQuery(id+"F10.imprint","IMPRINT",FACE,{"disambiguationData":[TD([[makeQuery(id+"F10.imprint","IMPRINT",EDGE,{"derivedFrom":sQuery(id+"F10.wireOp",EDGE,"E968")}),-1.0]])]});
            var Q11;
            Q11=makeQuery(id+"F10.imprint","IMPRINT",FACE,{"disambiguationData":[TD([[makeQuery(id+"F10.imprint","IMPRINT",EDGE,{"derivedFrom":sQuery(id+"F10.wireOp",EDGE,"E976")}),-1.0]])]});
            var Q12;
            Q12=makeQuery(id+"F10.imprint","IMPRINT",FACE,{"disambiguationData":[TD([[makeQuery(id+"F10.imprint","IMPRINT",EDGE,{"derivedFrom":sQuery(id+"F10.wireOp",EDGE,"E958")}),-1.0]])]});
            var Q13;
            Q13=makeQuery(id+"F10.imprint","IMPRINT",FACE,{"disambiguationData":[TD([[makeQuery(id+"F10.imprint","IMPRINT",EDGE,{"derivedFrom":sQuery(id+"F10.wireOp",EDGE,"E973")}),-1.0]])]});
            var Q14;
            Q14=makeQuery(id+"F10.imprint","IMPRINT",FACE,{"disambiguationData":[TD([[makeQuery(id+"F10.imprint","IMPRINT",EDGE,{"derivedFrom":sQuery(id+"F10.wireOp",EDGE,"E965")}),-1.0]])]});
            var Q15;
            Q15=makeQuery(id+"F10.imprint","IMPRINT",FACE,{"disambiguationData":[TD([[makeQuery(id+"F10.imprint","IMPRINT",EDGE,{"derivedFrom":sQuery(id+"F10.wireOp",EDGE,"E324")}),-1.0]])]});
            var Q16;
            Q16=makeQuery(id+"F10.imprint","IMPRINT",FACE,{"disambiguationData":[TD([[makeQuery(id+"F10.imprint","IMPRINT",EDGE,{"derivedFrom":sQuery(id+"F10.wireOp",EDGE,"E931")}),-1.0]])]});
            var Q17;
            Q17=makeQuery(id+"F10.imprint","IMPRINT",FACE,{"disambiguationData":[TD([[makeQuery(id+"F10.imprint","IMPRINT",EDGE,{"derivedFrom":sQuery(id+"F10.wireOp",EDGE,"E922")}),-1.0]])]});
            extrude(context, id + "F11", {"entities" : qUnion([Q0, Q1, Q2, Q3, Q4, Q5, Q6, Q7, Q8, Q9, Q10, Q11, Q12, Q13, Q14, Q15, Q16, Q17]), "operationType" : NewBodyOperationType.REMOVE, "oppositeDirection" : true, "depth" : 1 * mm});
        }
    });
